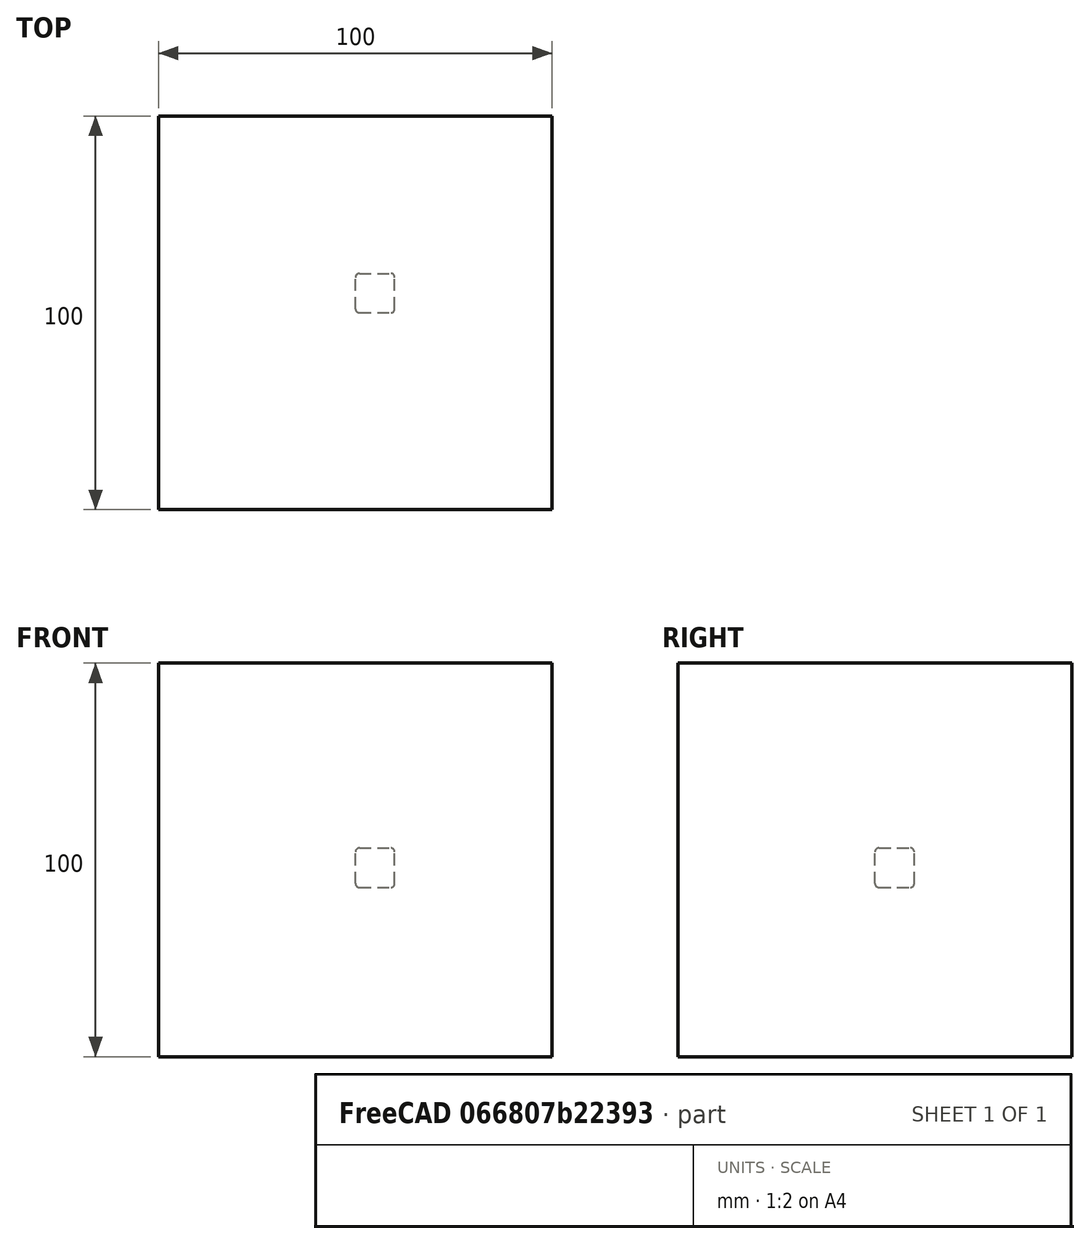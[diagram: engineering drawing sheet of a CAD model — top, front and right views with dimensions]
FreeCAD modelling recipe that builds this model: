
FCSTD DOCUMENT  (FreeCAD 0.22R36391 (Git))
Label: fillet
License: All rights reserved
objects: App::DocumentObjectGroupPython×1251, App::Part×2, Part::FeaturePython×1, Part::Box×1, Part::Fillet×1
note: 3 computed .brp shape members not serialized (recipe doc carries the construction recipe); baked Part::Feature solids carry a one-line shape summary decoded from their .brp

FEATURE [App::DocumentObjectGroupPython] HALFPI  # scripted group (container) (typed FeaturePython)
  name = HALFPI
  value = pi/2.
FEATURE [App::DocumentObjectGroupPython] PI  # scripted group (container) (typed FeaturePython)
  name = PI
  value = 1.*pi
FEATURE [App::DocumentObjectGroupPython] TWOPI  # scripted group (container) (typed FeaturePython)
  name = TWOPI
  value = 2.*pi
FEATURE [App::DocumentObjectGroupPython] Constants  # scripted group (container) (typed FeaturePython)
  Group = -> [HALFPI,PI,TWOPI]
FEATURE [App::DocumentObjectGroupPython] Variables  # scripted group (container) (typed FeaturePython)
FEATURE [App::DocumentObjectGroupPython] Quantities  # scripted group (container) (typed FeaturePython)
FEATURE [App::DocumentObjectGroupPython] Isotopes  # scripted group (container) (typed FeaturePython)
FEATURE [App::DocumentObjectGroupPython] Elements  # scripted group (container) (typed FeaturePython)
FEATURE [App::DocumentObjectGroupPython] Matrix  # scripted group (container) (typed FeaturePython)
FEATURE [App::DocumentObjectGroupPython] Surfaces  # scripted group (container) (typed FeaturePython)
FEATURE [App::DocumentObjectGroupPython] Opticals  # scripted group (container) (typed FeaturePython)
  Group = -> [Matrix,Surfaces]
FEATURE [App::DocumentObjectGroupPython] G4Isotopes  # scripted group (container) (typed FeaturePython)
FEATURE [App::DocumentObjectGroupPython] H_element  # scripted group (container) (typed FeaturePython)
  Z = 1
  atom_value = 1.008
  formula = H
  name = H_element
FEATURE [App::DocumentObjectGroupPython] He_element  # scripted group (container) (typed FeaturePython)
  Z = 2
  atom_value = 4.0026
  formula = He
  name = He_element
FEATURE [App::DocumentObjectGroupPython] Li_element  # scripted group (container) (typed FeaturePython)
  Z = 3
  atom_value = 6.94
  formula = Li
  name = Li_element
FEATURE [App::DocumentObjectGroupPython] Be_element  # scripted group (container) (typed FeaturePython)
  Z = 4
  atom_value = 9.01218
  formula = Be
  name = Be_element
FEATURE [App::DocumentObjectGroupPython] B_element  # scripted group (container) (typed FeaturePython)
  Z = 5
  atom_value = 10.81
  formula = B
  name = B_element
FEATURE [App::DocumentObjectGroupPython] C_element  # scripted group (container) (typed FeaturePython)
  Z = 6
  atom_value = 12.011
  formula = C
  name = C_element
FEATURE [App::DocumentObjectGroupPython] N_element  # scripted group (container) (typed FeaturePython)
  Z = 7
  atom_value = 14.007
  formula = N
  name = N_element
FEATURE [App::DocumentObjectGroupPython] O_element  # scripted group (container) (typed FeaturePython)
  Z = 8
  atom_value = 15.999
  formula = O
  name = O_element
FEATURE [App::DocumentObjectGroupPython] F_element  # scripted group (container) (typed FeaturePython)
  Z = 9
  atom_value = 18.9984
  formula = F
  name = F_element
FEATURE [App::DocumentObjectGroupPython] Ne_element  # scripted group (container) (typed FeaturePython)
  Z = 10
  atom_value = 20.1797
  formula = Ne
  name = Ne_element
FEATURE [App::DocumentObjectGroupPython] Na_element  # scripted group (container) (typed FeaturePython)
  Z = 11
  atom_value = 22.9898
  formula = Na
  name = Na_element
FEATURE [App::DocumentObjectGroupPython] Mg_element  # scripted group (container) (typed FeaturePython)
  Z = 12
  atom_value = 24.305
  formula = Mg
  name = Mg_element
FEATURE [App::DocumentObjectGroupPython] Al_element  # scripted group (container) (typed FeaturePython)
  Z = 13
  atom_value = 26.9815
  formula = Al
  name = Al_element
FEATURE [App::DocumentObjectGroupPython] Si_element  # scripted group (container) (typed FeaturePython)
  Z = 14
  atom_value = 28.085
  formula = Si
  name = Si_element
FEATURE [App::DocumentObjectGroupPython] P_element  # scripted group (container) (typed FeaturePython)
  Z = 15
  atom_value = 30.9738
  formula = P
  name = P_element
FEATURE [App::DocumentObjectGroupPython] S_element  # scripted group (container) (typed FeaturePython)
  Z = 16
  atom_value = 32.06
  formula = S
  name = S_element
FEATURE [App::DocumentObjectGroupPython] Cl_element  # scripted group (container) (typed FeaturePython)
  Z = 17
  atom_value = 35.45
  formula = Cl
  name = Cl_element
FEATURE [App::DocumentObjectGroupPython] Ar_element  # scripted group (container) (typed FeaturePython)
  Z = 18
  atom_value = 39.95
  formula = Ar
  name = Ar_element
FEATURE [App::DocumentObjectGroupPython] K_element  # scripted group (container) (typed FeaturePython)
  Z = 19
  atom_value = 39.0983
  formula = K
  name = K_element
FEATURE [App::DocumentObjectGroupPython] Ca_element  # scripted group (container) (typed FeaturePython)
  Z = 20
  atom_value = 40.078
  formula = Ca
  name = Ca_element
FEATURE [App::DocumentObjectGroupPython] Sc_element  # scripted group (container) (typed FeaturePython)
  Z = 21
  atom_value = 44.9559
  formula = Sc
  name = Sc_element
FEATURE [App::DocumentObjectGroupPython] Ti_element  # scripted group (container) (typed FeaturePython)
  Z = 22
  atom_value = 47.867
  formula = Ti
  name = Ti_element
FEATURE [App::DocumentObjectGroupPython] V_element  # scripted group (container) (typed FeaturePython)
  Z = 23
  atom_value = 50.9415
  formula = V
  name = V_element
FEATURE [App::DocumentObjectGroupPython] Cr_element  # scripted group (container) (typed FeaturePython)
  Z = 24
  atom_value = 51.9961
  formula = Cr
  name = Cr_element
FEATURE [App::DocumentObjectGroupPython] Mn_element  # scripted group (container) (typed FeaturePython)
  Z = 25
  atom_value = 54.938
  formula = Mn
  name = Mn_element
FEATURE [App::DocumentObjectGroupPython] Fe_element  # scripted group (container) (typed FeaturePython)
  Z = 26
  atom_value = 55.845
  formula = Fe
  name = Fe_element
FEATURE [App::DocumentObjectGroupPython] Co_element  # scripted group (container) (typed FeaturePython)
  Z = 27
  atom_value = 58.9332
  formula = Co
  name = Co_element
FEATURE [App::DocumentObjectGroupPython] Ni_element  # scripted group (container) (typed FeaturePython)
  Z = 28
  atom_value = 58.6934
  formula = Ni
  name = Ni_element
FEATURE [App::DocumentObjectGroupPython] Cu_element  # scripted group (container) (typed FeaturePython)
  Z = 29
  atom_value = 63.546
  formula = Cu
  name = Cu_element
FEATURE [App::DocumentObjectGroupPython] Zn_element  # scripted group (container) (typed FeaturePython)
  Z = 30
  atom_value = 65.38
  formula = Zn
  name = Zn_element
FEATURE [App::DocumentObjectGroupPython] Ga_element  # scripted group (container) (typed FeaturePython)
  Z = 31
  atom_value = 69.723
  formula = Ga
  name = Ga_element
FEATURE [App::DocumentObjectGroupPython] Ge_element  # scripted group (container) (typed FeaturePython)
  Z = 32
  atom_value = 72.63
  formula = Ge
  name = Ge_element
FEATURE [App::DocumentObjectGroupPython] As_element  # scripted group (container) (typed FeaturePython)
  Z = 33
  atom_value = 74.9216
  formula = As
  name = As_element
FEATURE [App::DocumentObjectGroupPython] Se_element  # scripted group (container) (typed FeaturePython)
  Z = 34
  atom_value = 78.971
  formula = Se
  name = Se_element
FEATURE [App::DocumentObjectGroupPython] Br_element  # scripted group (container) (typed FeaturePython)
  Z = 35
  atom_value = 79.904
  formula = Br
  name = Br_element
FEATURE [App::DocumentObjectGroupPython] Kr_element  # scripted group (container) (typed FeaturePython)
  Z = 36
  atom_value = 83.798
  formula = Kr
  name = Kr_element
FEATURE [App::DocumentObjectGroupPython] Rb_element  # scripted group (container) (typed FeaturePython)
  Z = 37
  atom_value = 85.4678
  formula = Rb
  name = Rb_element
FEATURE [App::DocumentObjectGroupPython] Sr_element  # scripted group (container) (typed FeaturePython)
  Z = 38
  atom_value = 87.62
  formula = Sr
  name = Sr_element
FEATURE [App::DocumentObjectGroupPython] Y_element  # scripted group (container) (typed FeaturePython)
  Z = 39
  atom_value = 88.9058
  formula = Y
  name = Y_element
FEATURE [App::DocumentObjectGroupPython] Zr_element  # scripted group (container) (typed FeaturePython)
  Z = 40
  atom_value = 91.224
  formula = Zr
  name = Zr_element
FEATURE [App::DocumentObjectGroupPython] Nb_element  # scripted group (container) (typed FeaturePython)
  Z = 41
  atom_value = 92.9064
  formula = Nb
  name = Nb_element
FEATURE [App::DocumentObjectGroupPython] Mo_element  # scripted group (container) (typed FeaturePython)
  Z = 42
  atom_value = 95.95
  formula = Mo
  name = Mo_element
FEATURE [App::DocumentObjectGroupPython] Tc_element  # scripted group (container) (typed FeaturePython)
  Z = 43
  atom_value = 97
  formula = Tc
  name = Tc_element
FEATURE [App::DocumentObjectGroupPython] Ru_element  # scripted group (container) (typed FeaturePython)
  Z = 44
  atom_value = 101.07
  formula = Ru
  name = Ru_element
FEATURE [App::DocumentObjectGroupPython] Rh_element  # scripted group (container) (typed FeaturePython)
  Z = 45
  atom_value = 102.905
  formula = Rh
  name = Rh_element
FEATURE [App::DocumentObjectGroupPython] Pd_element  # scripted group (container) (typed FeaturePython)
  Z = 46
  atom_value = 106.42
  formula = Pd
  name = Pd_element
FEATURE [App::DocumentObjectGroupPython] Ag_element  # scripted group (container) (typed FeaturePython)
  Z = 47
  atom_value = 107.868
  formula = Ag
  name = Ag_element
FEATURE [App::DocumentObjectGroupPython] Cd_element  # scripted group (container) (typed FeaturePython)
  Z = 48
  atom_value = 112.414
  formula = Cd
  name = Cd_element
FEATURE [App::DocumentObjectGroupPython] In_element  # scripted group (container) (typed FeaturePython)
  Z = 49
  atom_value = 114.818
  formula = In
  name = In_element
FEATURE [App::DocumentObjectGroupPython] Sn_element  # scripted group (container) (typed FeaturePython)
  Z = 50
  atom_value = 118.71
  formula = Sn
  name = Sn_element
FEATURE [App::DocumentObjectGroupPython] Sb_element  # scripted group (container) (typed FeaturePython)
  Z = 51
  atom_value = 121.76
  formula = Sb
  name = Sb_element
FEATURE [App::DocumentObjectGroupPython] Te_element  # scripted group (container) (typed FeaturePython)
  Z = 52
  atom_value = 127.6
  formula = Te
  name = Te_element
FEATURE [App::DocumentObjectGroupPython] I_element  # scripted group (container) (typed FeaturePython)
  Z = 53
  atom_value = 126.904
  formula = I
  name = I_element
FEATURE [App::DocumentObjectGroupPython] Xe_element  # scripted group (container) (typed FeaturePython)
  Z = 54
  atom_value = 131.293
  formula = Xe
  name = Xe_element
FEATURE [App::DocumentObjectGroupPython] Cs_element  # scripted group (container) (typed FeaturePython)
  Z = 55
  atom_value = 132.905
  formula = Cs
  name = Cs_element
FEATURE [App::DocumentObjectGroupPython] Ba_element  # scripted group (container) (typed FeaturePython)
  Z = 56
  atom_value = 137.327
  formula = Ba
  name = Ba_element
FEATURE [App::DocumentObjectGroupPython] La_element  # scripted group (container) (typed FeaturePython)
  Z = 57
  atom_value = 138.905
  formula = La
  name = La_element
FEATURE [App::DocumentObjectGroupPython] Ce_element  # scripted group (container) (typed FeaturePython)
  Z = 58
  atom_value = 140.116
  formula = Ce
  name = Ce_element
FEATURE [App::DocumentObjectGroupPython] Pr_element  # scripted group (container) (typed FeaturePython)
  Z = 59
  atom_value = 140.908
  formula = Pr
  name = Pr_element
FEATURE [App::DocumentObjectGroupPython] Nd_element  # scripted group (container) (typed FeaturePython)
  Z = 60
  atom_value = 144.242
  formula = Nd
  name = Nd_element
FEATURE [App::DocumentObjectGroupPython] Pm_element  # scripted group (container) (typed FeaturePython)
  Z = 61
  atom_value = 145
  formula = Pm
  name = Pm_element
FEATURE [App::DocumentObjectGroupPython] Sm_element  # scripted group (container) (typed FeaturePython)
  Z = 62
  atom_value = 150.36
  formula = Sm
  name = Sm_element
FEATURE [App::DocumentObjectGroupPython] Eu_element  # scripted group (container) (typed FeaturePython)
  Z = 63
  atom_value = 151.964
  formula = Eu
  name = Eu_element
FEATURE [App::DocumentObjectGroupPython] Gd_element  # scripted group (container) (typed FeaturePython)
  Z = 64
  atom_value = 157.25
  formula = Gd
  name = Gd_element
FEATURE [App::DocumentObjectGroupPython] Tb_element  # scripted group (container) (typed FeaturePython)
  Z = 65
  atom_value = 158.925
  formula = Tb
  name = Tb_element
FEATURE [App::DocumentObjectGroupPython] Dy_element  # scripted group (container) (typed FeaturePython)
  Z = 66
  atom_value = 162.5
  formula = Dy
  name = Dy_element
FEATURE [App::DocumentObjectGroupPython] Ho_element  # scripted group (container) (typed FeaturePython)
  Z = 67
  atom_value = 164.93
  formula = Ho
  name = Ho_element
FEATURE [App::DocumentObjectGroupPython] Er_element  # scripted group (container) (typed FeaturePython)
  Z = 68
  atom_value = 167.259
  formula = Er
  name = Er_element
FEATURE [App::DocumentObjectGroupPython] Tm_element  # scripted group (container) (typed FeaturePython)
  Z = 69
  atom_value = 168.934
  formula = Tm
  name = Tm_element
FEATURE [App::DocumentObjectGroupPython] Yb_element  # scripted group (container) (typed FeaturePython)
  Z = 70
  atom_value = 173.045
  formula = Yb
  name = Yb_element
FEATURE [App::DocumentObjectGroupPython] Lu_element  # scripted group (container) (typed FeaturePython)
  Z = 71
  atom_value = 174.967
  formula = Lu
  name = Lu_element
FEATURE [App::DocumentObjectGroupPython] Hf_element  # scripted group (container) (typed FeaturePython)
  Z = 72
  atom_value = 178.49
  formula = Hf
  name = Hf_element
FEATURE [App::DocumentObjectGroupPython] Ta_element  # scripted group (container) (typed FeaturePython)
  Z = 73
  atom_value = 180.948
  formula = Ta
  name = Ta_element
FEATURE [App::DocumentObjectGroupPython] W_element  # scripted group (container) (typed FeaturePython)
  Z = 74
  atom_value = 183.84
  formula = W
  name = W_element
FEATURE [App::DocumentObjectGroupPython] Re_element  # scripted group (container) (typed FeaturePython)
  Z = 75
  atom_value = 186.207
  formula = Re
  name = Re_element
FEATURE [App::DocumentObjectGroupPython] Os_element  # scripted group (container) (typed FeaturePython)
  Z = 76
  atom_value = 190.23
  formula = Os
  name = Os_element
FEATURE [App::DocumentObjectGroupPython] Ir_element  # scripted group (container) (typed FeaturePython)
  Z = 77
  atom_value = 192.217
  formula = Ir
  name = Ir_element
FEATURE [App::DocumentObjectGroupPython] Pt_element  # scripted group (container) (typed FeaturePython)
  Z = 78
  atom_value = 195.084
  formula = Pt
  name = Pt_element
FEATURE [App::DocumentObjectGroupPython] Au_element  # scripted group (container) (typed FeaturePython)
  Z = 79
  atom_value = 196.967
  formula = Au
  name = Au_element
FEATURE [App::DocumentObjectGroupPython] Hg_element  # scripted group (container) (typed FeaturePython)
  Z = 80
  atom_value = 200.592
  formula = Hg
  name = Hg_element
FEATURE [App::DocumentObjectGroupPython] Tl_element  # scripted group (container) (typed FeaturePython)
  Z = 81
  atom_value = 204.38
  formula = Tl
  name = Tl_element
FEATURE [App::DocumentObjectGroupPython] Pb_element  # scripted group (container) (typed FeaturePython)
  Z = 82
  atom_value = 207.2
  formula = Pb
  name = Pb_element
FEATURE [App::DocumentObjectGroupPython] Bi_element  # scripted group (container) (typed FeaturePython)
  Z = 83
  atom_value = 208.98
  formula = Bi
  name = Bi_element
FEATURE [App::DocumentObjectGroupPython] Po_element  # scripted group (container) (typed FeaturePython)
  Z = 84
  atom_value = 209
  formula = Po
  name = Po_element
FEATURE [App::DocumentObjectGroupPython] At_element  # scripted group (container) (typed FeaturePython)
  Z = 85
  atom_value = 210
  formula = At
  name = At_element
FEATURE [App::DocumentObjectGroupPython] Rn_element  # scripted group (container) (typed FeaturePython)
  Z = 86
  atom_value = 222
  formula = Rn
  name = Rn_element
FEATURE [App::DocumentObjectGroupPython] Fr_element  # scripted group (container) (typed FeaturePython)
  Z = 87
  atom_value = 223
  formula = Fr
  name = Fr_element
FEATURE [App::DocumentObjectGroupPython] Ra_element  # scripted group (container) (typed FeaturePython)
  Z = 88
  atom_value = 226
  formula = Ra
  name = Ra_element
FEATURE [App::DocumentObjectGroupPython] Ac_element  # scripted group (container) (typed FeaturePython)
  Z = 89
  atom_value = 227
  formula = Ac
  name = Ac_element
FEATURE [App::DocumentObjectGroupPython] Th_element  # scripted group (container) (typed FeaturePython)
  Z = 90
  atom_value = 232.038
  formula = Th
  name = Th_element
FEATURE [App::DocumentObjectGroupPython] Pa_element  # scripted group (container) (typed FeaturePython)
  Z = 91
  atom_value = 231.036
  formula = Pa
  name = Pa_element
FEATURE [App::DocumentObjectGroupPython] U_element  # scripted group (container) (typed FeaturePython)
  Z = 92
  atom_value = 238.029
  formula = U
  name = U_element
FEATURE [App::DocumentObjectGroupPython] Np_element  # scripted group (container) (typed FeaturePython)
  Z = 93
  atom_value = 237
  formula = Np
  name = Np_element
FEATURE [App::DocumentObjectGroupPython] Pu_element  # scripted group (container) (typed FeaturePython)
  Z = 94
  atom_value = 244
  formula = Pu
  name = Pu_element
FEATURE [App::DocumentObjectGroupPython] Am_element  # scripted group (container) (typed FeaturePython)
  Z = 95
  atom_value = 243
  formula = Am
  name = Am_element
FEATURE [App::DocumentObjectGroupPython] Cm_element  # scripted group (container) (typed FeaturePython)
  Z = 96
  atom_value = 247
  formula = Cm
  name = Cm_element
FEATURE [App::DocumentObjectGroupPython] Bk_element  # scripted group (container) (typed FeaturePython)
  Z = 97
  atom_value = 247
  formula = Bk
  name = Bk_element
FEATURE [App::DocumentObjectGroupPython] Cf_element  # scripted group (container) (typed FeaturePython)
  Z = 98
  atom_value = 251
  formula = Cf
  name = Cf_element
FEATURE [App::DocumentObjectGroupPython] G4Elements  # scripted group (container) (typed FeaturePython)
  Group = -> [H_element,He_element,Li_element,Be_element,B_element,C_element,N_element,O_element,F_element,Ne_element,Na_element,Mg_element,Al_element,Si_element,P_element,S_element,Cl_element,Ar_element,K_element,Ca_element,Sc_element,Ti_element,V_element,Cr_element,Mn_element,Fe_element,Co_element,Ni_element,Cu_element,Zn_element,Ga_element,Ge_element,As_element,Se_element,Br_element,Kr_element,Rb_element,+61 more]
FEATURE [App::DocumentObjectGroupPython] H_element001  label="H_element : 0.101"  # scripted group (container) (typed FeaturePython)
  n = 0.101327
FEATURE [App::DocumentObjectGroupPython] C_element001  label="C_element : 0.775"  # scripted group (container) (typed FeaturePython)
  n = 0.7755
FEATURE [App::DocumentObjectGroupPython] N_element001  label="N_element : 0.035"  # scripted group (container) (typed FeaturePython)
  n = 0.035057
FEATURE [App::DocumentObjectGroupPython] O_element001  label="O_element : 0.052"  # scripted group (container) (typed FeaturePython)
  n = 0.0523159
FEATURE [App::DocumentObjectGroupPython] F_element001  label="F_element : 0.017"  # scripted group (container) (typed FeaturePython)
  n = 0.017422
FEATURE [App::DocumentObjectGroupPython] Ca_element001  label="Ca_element : 0.018"  # scripted group (container) (typed FeaturePython)
  n = 0.018378
FEATURE [App::DocumentObjectGroupPython] G4_A_150_TISSUE  label="G4_A-150_TISSUE"  # scripted group (container) (typed FeaturePython)
  Dunit = g/cm3
  Dvalue = 1.127
  Group = -> [H_element001,C_element001,N_element001,O_element001,F_element001,Ca_element001]
  conduct = 2
  density = 1
  expand = 3
  formula = G4_A-150_TISSUE
  name = G4_A-150_TISSUE
  specific = 4
FEATURE [App::DocumentObjectGroupPython] C_element002  label="C_element : 3"  # scripted group (container) (typed FeaturePython)
  n = 3
  ref = C_element
FEATURE [App::DocumentObjectGroupPython] H_element002  label="H_element : 6"  # scripted group (container) (typed FeaturePython)
  n = 6
  ref = H_element
FEATURE [App::DocumentObjectGroupPython] O_element002  label="O_element : 1"  # scripted group (container) (typed FeaturePython)
  n = 1
  ref = O_element
FEATURE [App::DocumentObjectGroupPython] G4_ACETONE  # scripted group (container) (typed FeaturePython)
  Dunit = g/cm3
  Dvalue = 0.7899
  Group = -> [C_element002,H_element002,O_element002]
  conduct = 2
  density = 1
  expand = 3
  formula = G4_ACETONE
  name = G4_ACETONE
  specific = 4
FEATURE [App::DocumentObjectGroupPython] C_element003  label="C_element : 2"  # scripted group (container) (typed FeaturePython)
  n = 2
  ref = C_element
FEATURE [App::DocumentObjectGroupPython] H_element003  label="H_element : 2"  # scripted group (container) (typed FeaturePython)
  n = 2
  ref = H_element
FEATURE [App::DocumentObjectGroupPython] G4_ACETYLENE  # scripted group (container) (typed FeaturePython)
  Dunit = g/cm3
  Dvalue = 0.0010967
  Group = -> [C_element003,H_element003]
  conduct = 2
  density = 1
  expand = 3
  formula = G4_ACETYLENE
  name = G4_ACETYLENE
  specific = 4
FEATURE [App::DocumentObjectGroupPython] C_element004  label="C_element : 5"  # scripted group (container) (typed FeaturePython)
  n = 5
  ref = C_element
FEATURE [App::DocumentObjectGroupPython] H_element004  label="H_element : 5"  # scripted group (container) (typed FeaturePython)
  n = 5
  ref = H_element
FEATURE [App::DocumentObjectGroupPython] N_element002  label="N_element : 5"  # scripted group (container) (typed FeaturePython)
  n = 5
  ref = N_element
FEATURE [App::DocumentObjectGroupPython] G4_ADENINE  # scripted group (container) (typed FeaturePython)
  Dunit = g/cm3
  Dvalue = 1.6
  Group = -> [C_element004,H_element004,N_element002]
  conduct = 2
  density = 1
  expand = 3
  formula = G4_ADENINE
  name = G4_ADENINE
  specific = 4
FEATURE [App::DocumentObjectGroupPython] H_element005  label="H_element : 0.114"  # scripted group (container) (typed FeaturePython)
  n = 0.114
FEATURE [App::DocumentObjectGroupPython] C_element005  label="C_element : 0.598"  # scripted group (container) (typed FeaturePython)
  n = 0.598
FEATURE [App::DocumentObjectGroupPython] N_element003  label="N_element : 0.007"  # scripted group (container) (typed FeaturePython)
  n = 0.007
FEATURE [App::DocumentObjectGroupPython] O_element003  label="O_element : 0.278"  # scripted group (container) (typed FeaturePython)
  n = 0.278
FEATURE [App::DocumentObjectGroupPython] Na_element001  label="Na_element : 0.001"  # scripted group (container) (typed FeaturePython)
  n = 0.001
FEATURE [App::DocumentObjectGroupPython] S_element001  label="S_element : 0.001"  # scripted group (container) (typed FeaturePython)
  n = 0.001
FEATURE [App::DocumentObjectGroupPython] Cl_element001  label="Cl_element : 0.001"  # scripted group (container) (typed FeaturePython)
  n = 0.001
FEATURE [App::DocumentObjectGroupPython] G4_ADIPOSE_TISSUE_ICRP  # scripted group (container) (typed FeaturePython)
  Dunit = g/cm3
  Dvalue = 0.95
  Group = -> [H_element005,C_element005,N_element003,O_element003,Na_element001,S_element001,Cl_element001]
  conduct = 2
  density = 1
  expand = 3
  formula = G4_ADIPOSE_TISSUE_ICRP
  name = G4_ADIPOSE_TISSUE_ICRP
  specific = 4
FEATURE [App::DocumentObjectGroupPython] C_element006  label="C_element : 0.000"  # scripted group (container) (typed FeaturePython)
  n = 0.000124
FEATURE [App::DocumentObjectGroupPython] N_element004  label="N_element : 0.755"  # scripted group (container) (typed FeaturePython)
  n = 0.755268
FEATURE [App::DocumentObjectGroupPython] O_element004  label="O_element : 0.232"  # scripted group (container) (typed FeaturePython)
  n = 0.231781
FEATURE [App::DocumentObjectGroupPython] Ar_element001  label="Ar_element : 0.013"  # scripted group (container) (typed FeaturePython)
  n = 0.012827
FEATURE [App::DocumentObjectGroupPython] G4_AIR  # scripted group (container) (typed FeaturePython)
  Dunit = g/cm3
  Dvalue = 0.00120479
  Group = -> [C_element006,N_element004,O_element004,Ar_element001]
  conduct = 2
  density = 1
  expand = 3
  formula = G4_AIR
  name = G4_AIR
  specific = 4
FEATURE [App::DocumentObjectGroupPython] C_element007  label="C_element : 006"  # scripted group (container) (typed FeaturePython)
  n = 3
  ref = C_element
FEATURE [App::DocumentObjectGroupPython] H_element006  label="H_element : 7"  # scripted group (container) (typed FeaturePython)
  n = 7
  ref = H_element
FEATURE [App::DocumentObjectGroupPython] N_element005  label="N_element : 1"  # scripted group (container) (typed FeaturePython)
  n = 1
  ref = N_element
FEATURE [App::DocumentObjectGroupPython] O_element005  label="O_element : 2"  # scripted group (container) (typed FeaturePython)
  n = 2
  ref = O_element
FEATURE [App::DocumentObjectGroupPython] G4_ALANINE  # scripted group (container) (typed FeaturePython)
  Dunit = g/cm3
  Dvalue = 1.42
  Group = -> [C_element007,H_element006,N_element005,O_element005]
  conduct = 2
  density = 1
  expand = 3
  formula = G4_ALANINE
  name = G4_ALANINE
  specific = 4
FEATURE [App::DocumentObjectGroupPython] Al_element001  label="Al_element : 2"  # scripted group (container) (typed FeaturePython)
  n = 2
  ref = Al_element
FEATURE [App::DocumentObjectGroupPython] O_element006  label="O_element : 3"  # scripted group (container) (typed FeaturePython)
  n = 3
  ref = O_element
FEATURE [App::DocumentObjectGroupPython] G4_ALUMINUM_OXIDE  # scripted group (container) (typed FeaturePython)
  Dunit = g/cm3
  Dvalue = 3.97
  Group = -> [Al_element001,O_element006]
  conduct = 2
  density = 1
  expand = 3
  formula = G4_ALUMINUM_OXIDE
  name = G4_ALUMINUM_OXIDE
  specific = 4
FEATURE [App::DocumentObjectGroupPython] H_element007  label="H_element : 0.106"  # scripted group (container) (typed FeaturePython)
  n = 0.10593
FEATURE [App::DocumentObjectGroupPython] C_element008  label="C_element : 0.789"  # scripted group (container) (typed FeaturePython)
  n = 0.788974
FEATURE [App::DocumentObjectGroupPython] O_element007  label="O_element : 0.105"  # scripted group (container) (typed FeaturePython)
  n = 0.105096
FEATURE [App::DocumentObjectGroupPython] G4_AMBER  # scripted group (container) (typed FeaturePython)
  Dunit = g/cm3
  Dvalue = 1.1
  Group = -> [H_element007,C_element008,O_element007]
  conduct = 2
  density = 1
  expand = 3
  formula = G4_AMBER
  name = G4_AMBER
  specific = 4
FEATURE [App::DocumentObjectGroupPython] N_element006  label="N_element : 006"  # scripted group (container) (typed FeaturePython)
  n = 1
  ref = N_element
FEATURE [App::DocumentObjectGroupPython] H_element008  label="H_element : 3"  # scripted group (container) (typed FeaturePython)
  n = 3
  ref = H_element
FEATURE [App::DocumentObjectGroupPython] G4_AMMONIA  # scripted group (container) (typed FeaturePython)
  Dunit = g/cm3
  Dvalue = 0.000826019
  Group = -> [N_element006,H_element008]
  conduct = 2
  density = 1
  expand = 3
  formula = G4_AMMONIA
  name = G4_AMMONIA
  specific = 4
FEATURE [App::DocumentObjectGroupPython] C_element009  label="C_element : 6"  # scripted group (container) (typed FeaturePython)
  n = 6
  ref = C_element
FEATURE [App::DocumentObjectGroupPython] H_element009  label="H_element : 008"  # scripted group (container) (typed FeaturePython)
  n = 7
  ref = H_element
FEATURE [App::DocumentObjectGroupPython] N_element007  label="N_element : 007"  # scripted group (container) (typed FeaturePython)
  n = 1
  ref = N_element
FEATURE [App::DocumentObjectGroupPython] G4_ANILINE  # scripted group (container) (typed FeaturePython)
  Dunit = g/cm3
  Dvalue = 1.0235
  Group = -> [C_element009,H_element009,N_element007]
  conduct = 2
  density = 1
  expand = 3
  formula = G4_ANILINE
  name = G4_ANILINE
  specific = 4
FEATURE [App::DocumentObjectGroupPython] C_element010  label="C_element : 14"  # scripted group (container) (typed FeaturePython)
  n = 14
  ref = C_element
FEATURE [App::DocumentObjectGroupPython] H_element010  label="H_element : 10"  # scripted group (container) (typed FeaturePython)
  n = 10
  ref = H_element
FEATURE [App::DocumentObjectGroupPython] G4_ANTHRACENE  # scripted group (container) (typed FeaturePython)
  Dunit = g/cm3
  Dvalue = 1.283
  Group = -> [C_element010,H_element010]
  conduct = 2
  density = 1
  expand = 3
  formula = G4_ANTHRACENE
  name = G4_ANTHRACENE
  specific = 4
FEATURE [App::DocumentObjectGroupPython] H_element011  label="H_element : 0.065"  # scripted group (container) (typed FeaturePython)
  n = 0.0654709
FEATURE [App::DocumentObjectGroupPython] C_element011  label="C_element : 0.537"  # scripted group (container) (typed FeaturePython)
  n = 0.536944
FEATURE [App::DocumentObjectGroupPython] N_element008  label="N_element : 0.021"  # scripted group (container) (typed FeaturePython)
  n = 0.0215
FEATURE [App::DocumentObjectGroupPython] O_element008  label="O_element : 0.032"  # scripted group (container) (typed FeaturePython)
  n = 0.032085
FEATURE [App::DocumentObjectGroupPython] F_element002  label="F_element : 0.167"  # scripted group (container) (typed FeaturePython)
  n = 0.167411
FEATURE [App::DocumentObjectGroupPython] Ca_element002  label="Ca_element : 0.177"  # scripted group (container) (typed FeaturePython)
  n = 0.176589
FEATURE [App::DocumentObjectGroupPython] G4_B_100_BONE  label="G4_B-100_BONE"  # scripted group (container) (typed FeaturePython)
  Dunit = g/cm3
  Dvalue = 1.45
  Group = -> [H_element011,C_element011,N_element008,O_element008,F_element002,Ca_element002]
  conduct = 2
  density = 1
  expand = 3
  formula = G4_B-100_BONE
  name = G4_B-100_BONE
  specific = 4
FEATURE [App::DocumentObjectGroupPython] H_element012  label="H_element : 0.057"  # scripted group (container) (typed FeaturePython)
  n = 0.057441
FEATURE [App::DocumentObjectGroupPython] C_element012  label="C_element : 0.790"  # scripted group (container) (typed FeaturePython)
  n = 0.774591
FEATURE [App::DocumentObjectGroupPython] O_element009  label="O_element : 0.168"  # scripted group (container) (typed FeaturePython)
  n = 0.167968
FEATURE [App::DocumentObjectGroupPython] G4_BAKELITE  # scripted group (container) (typed FeaturePython)
  Dunit = g/cm3
  Dvalue = 1.25
  Group = -> [H_element012,C_element012,O_element009]
  conduct = 2
  density = 1
  expand = 3
  formula = G4_BAKELITE
  name = G4_BAKELITE
  specific = 4
FEATURE [App::DocumentObjectGroupPython] Ba_element001  label="Ba_element : 1"  # scripted group (container) (typed FeaturePython)
  n = 1
  ref = Ba_element
FEATURE [App::DocumentObjectGroupPython] F_element003  label="F_element : 2"  # scripted group (container) (typed FeaturePython)
  n = 2
  ref = F_element
FEATURE [App::DocumentObjectGroupPython] G4_BARIUM_FLUORIDE  # scripted group (container) (typed FeaturePython)
  Dunit = g/cm3
  Dvalue = 4.89
  Group = -> [Ba_element001,F_element003]
  conduct = 2
  density = 1
  expand = 3
  formula = G4_BARIUM_FLUORIDE
  name = G4_BARIUM_FLUORIDE
  specific = 4
FEATURE [App::DocumentObjectGroupPython] Ba_element002  label="Ba_element : 002"  # scripted group (container) (typed FeaturePython)
  n = 1
  ref = Ba_element
FEATURE [App::DocumentObjectGroupPython] S_element002  label="S_element : 1"  # scripted group (container) (typed FeaturePython)
  n = 1
  ref = S_element
FEATURE [App::DocumentObjectGroupPython] O_element010  label="O_element : 4"  # scripted group (container) (typed FeaturePython)
  n = 4
  ref = O_element
FEATURE [App::DocumentObjectGroupPython] G4_BARIUM_SULFATE  # scripted group (container) (typed FeaturePython)
  Dunit = g/cm3
  Dvalue = 4.5
  Group = -> [Ba_element002,S_element002,O_element010]
  conduct = 2
  density = 1
  expand = 3
  formula = G4_BARIUM_SULFATE
  name = G4_BARIUM_SULFATE
  specific = 4
FEATURE [App::DocumentObjectGroupPython] C_element013  label="C_element : 007"  # scripted group (container) (typed FeaturePython)
  n = 6
  ref = C_element
FEATURE [App::DocumentObjectGroupPython] H_element013  label="H_element : 009"  # scripted group (container) (typed FeaturePython)
  n = 6
  ref = H_element
FEATURE [App::DocumentObjectGroupPython] G4_BENZENE  # scripted group (container) (typed FeaturePython)
  Dunit = g/cm3
  Dvalue = 0.87865
  Group = -> [C_element013,H_element013]
  conduct = 2
  density = 1
  expand = 3
  formula = G4_BENZENE
  name = G4_BENZENE
  specific = 4
FEATURE [App::DocumentObjectGroupPython] Be_element001  label="Be_element : 1"  # scripted group (container) (typed FeaturePython)
  n = 1
  ref = Be_element
FEATURE [App::DocumentObjectGroupPython] O_element011  label="O_element : 005"  # scripted group (container) (typed FeaturePython)
  n = 1
  ref = O_element
FEATURE [App::DocumentObjectGroupPython] G4_BERYLLIUM_OXIDE  # scripted group (container) (typed FeaturePython)
  Dunit = g/cm3
  Dvalue = 3.01
  Group = -> [Be_element001,O_element011]
  conduct = 2
  density = 1
  expand = 3
  formula = G4_BERYLLIUM_OXIDE
  name = G4_BERYLLIUM_OXIDE
  specific = 4
FEATURE [App::DocumentObjectGroupPython] Bi_element001  label="Bi_element : 4"  # scripted group (container) (typed FeaturePython)
  n = 4
  ref = Bi_element
FEATURE [App::DocumentObjectGroupPython] Ge_element001  label="Ge_element : 3"  # scripted group (container) (typed FeaturePython)
  n = 3
  ref = Ge_element
FEATURE [App::DocumentObjectGroupPython] O_element012  label="O_element : 12"  # scripted group (container) (typed FeaturePython)
  n = 12
  ref = O_element
FEATURE [App::DocumentObjectGroupPython] G4_BGO  # scripted group (container) (typed FeaturePython)
  Dunit = g/cm3
  Dvalue = 7.13
  Group = -> [Bi_element001,Ge_element001,O_element012]
  conduct = 2
  density = 1
  expand = 3
  formula = G4_BGO
  name = G4_BGO
  specific = 4
FEATURE [App::DocumentObjectGroupPython] H_element014  label="H_element : 0.102"  # scripted group (container) (typed FeaturePython)
  n = 0.102
FEATURE [App::DocumentObjectGroupPython] C_element014  label="C_element : 0.110"  # scripted group (container) (typed FeaturePython)
  n = 0.11
FEATURE [App::DocumentObjectGroupPython] N_element009  label="N_element : 0.033"  # scripted group (container) (typed FeaturePython)
  n = 0.033
FEATURE [App::DocumentObjectGroupPython] O_element013  label="O_element : 0.745"  # scripted group (container) (typed FeaturePython)
  n = 0.745
FEATURE [App::DocumentObjectGroupPython] Na_element002  label="Na_element : 0.002"  # scripted group (container) (typed FeaturePython)
  n = 0.001
FEATURE [App::DocumentObjectGroupPython] P_element001  label="P_element : 0.001"  # scripted group (container) (typed FeaturePython)
  n = 0.001
FEATURE [App::DocumentObjectGroupPython] S_element003  label="S_element : 0.002"  # scripted group (container) (typed FeaturePython)
  n = 0.002
FEATURE [App::DocumentObjectGroupPython] Cl_element002  label="Cl_element : 0.003"  # scripted group (container) (typed FeaturePython)
  n = 0.003
FEATURE [App::DocumentObjectGroupPython] K_element001  label="K_element : 0.002"  # scripted group (container) (typed FeaturePython)
  n = 0.002
FEATURE [App::DocumentObjectGroupPython] Fe_element001  label="Fe_element : 0.001"  # scripted group (container) (typed FeaturePython)
  n = 0.001
FEATURE [App::DocumentObjectGroupPython] G4_BLOOD_ICRP  # scripted group (container) (typed FeaturePython)
  Dunit = g/cm3
  Dvalue = 1.06
  Group = -> [H_element014,C_element014,N_element009,O_element013,Na_element002,P_element001,S_element003,Cl_element002,K_element001,Fe_element001]
  conduct = 2
  density = 1
  expand = 3
  formula = G4_BLOOD_ICRP
  name = G4_BLOOD_ICRP
  specific = 4
FEATURE [App::DocumentObjectGroupPython] H_element015  label="H_element : 0.064"  # scripted group (container) (typed FeaturePython)
  n = 0.064
FEATURE [App::DocumentObjectGroupPython] C_element015  label="C_element : 0.278"  # scripted group (container) (typed FeaturePython)
  n = 0.278
FEATURE [App::DocumentObjectGroupPython] N_element010  label="N_element : 0.027"  # scripted group (container) (typed FeaturePython)
  n = 0.027
FEATURE [App::DocumentObjectGroupPython] O_element014  label="O_element : 0.410"  # scripted group (container) (typed FeaturePython)
  n = 0.41
FEATURE [App::DocumentObjectGroupPython] Mg_element001  label="Mg_element : 0.002"  # scripted group (container) (typed FeaturePython)
  n = 0.002
FEATURE [App::DocumentObjectGroupPython] P_element002  label="P_element : 0.070"  # scripted group (container) (typed FeaturePython)
  n = 0.07
FEATURE [App::DocumentObjectGroupPython] S_element004  label="S_element : 0.003"  # scripted group (container) (typed FeaturePython)
  n = 0.002
FEATURE [App::DocumentObjectGroupPython] Ca_element003  label="Ca_element : 0.147"  # scripted group (container) (typed FeaturePython)
  n = 0.147
FEATURE [App::DocumentObjectGroupPython] G4_BONE_COMPACT_ICRU  # scripted group (container) (typed FeaturePython)
  Dunit = g/cm3
  Dvalue = 1.85
  Group = -> [H_element015,C_element015,N_element010,O_element014,Mg_element001,P_element002,S_element004,Ca_element003]
  conduct = 2
  density = 1
  expand = 3
  formula = G4_BONE_COMPACT_ICRU
  name = G4_BONE_COMPACT_ICRU
  specific = 4
FEATURE [App::DocumentObjectGroupPython] H_element016  label="H_element : 0.034"  # scripted group (container) (typed FeaturePython)
  n = 0.034
FEATURE [App::DocumentObjectGroupPython] C_element016  label="C_element : 0.155"  # scripted group (container) (typed FeaturePython)
  n = 0.155
FEATURE [App::DocumentObjectGroupPython] N_element011  label="N_element : 0.042"  # scripted group (container) (typed FeaturePython)
  n = 0.042
FEATURE [App::DocumentObjectGroupPython] O_element015  label="O_element : 0.435"  # scripted group (container) (typed FeaturePython)
  n = 0.435
FEATURE [App::DocumentObjectGroupPython] Na_element003  label="Na_element : 0.003"  # scripted group (container) (typed FeaturePython)
  n = 0.001
FEATURE [App::DocumentObjectGroupPython] Mg_element002  label="Mg_element : 0.003"  # scripted group (container) (typed FeaturePython)
  n = 0.002
FEATURE [App::DocumentObjectGroupPython] P_element003  label="P_element : 0.103"  # scripted group (container) (typed FeaturePython)
  n = 0.103
FEATURE [App::DocumentObjectGroupPython] S_element005  label="S_element : 0.004"  # scripted group (container) (typed FeaturePython)
  n = 0.003
FEATURE [App::DocumentObjectGroupPython] Ca_element004  label="Ca_element : 0.225"  # scripted group (container) (typed FeaturePython)
  n = 0.225
FEATURE [App::DocumentObjectGroupPython] G4_BONE_CORTICAL_ICRP  # scripted group (container) (typed FeaturePython)
  Dunit = g/cm3
  Dvalue = 1.92
  Group = -> [H_element016,C_element016,N_element011,O_element015,Na_element003,Mg_element002,P_element003,S_element005,Ca_element004]
  conduct = 2
  density = 1
  expand = 3
  formula = G4_BONE_CORTICAL_ICRP
  name = G4_BONE_CORTICAL_ICRP
  specific = 4
FEATURE [App::DocumentObjectGroupPython] B_element001  label="B_element : 4"  # scripted group (container) (typed FeaturePython)
  n = 4
  ref = B_element
FEATURE [App::DocumentObjectGroupPython] C_element017  label="C_element : 1"  # scripted group (container) (typed FeaturePython)
  n = 1
  ref = C_element
FEATURE [App::DocumentObjectGroupPython] G4_BORON_CARBIDE  # scripted group (container) (typed FeaturePython)
  Dunit = g/cm3
  Dvalue = 2.52
  Group = -> [B_element001,C_element017]
  conduct = 2
  density = 1
  expand = 3
  formula = G4_BORON_CARBIDE
  name = G4_BORON_CARBIDE
  specific = 4
FEATURE [App::DocumentObjectGroupPython] B_element002  label="B_element : 2"  # scripted group (container) (typed FeaturePython)
  n = 2
  ref = B_element
FEATURE [App::DocumentObjectGroupPython] O_element016  label="O_element : 006"  # scripted group (container) (typed FeaturePython)
  n = 3
  ref = O_element
FEATURE [App::DocumentObjectGroupPython] G4_BORON_OXIDE  # scripted group (container) (typed FeaturePython)
  Dunit = g/cm3
  Dvalue = 1.812
  Group = -> [B_element002,O_element016]
  conduct = 2
  density = 1
  expand = 3
  formula = G4_BORON_OXIDE
  name = G4_BORON_OXIDE
  specific = 4
FEATURE [App::DocumentObjectGroupPython] H_element017  label="H_element : 0.107"  # scripted group (container) (typed FeaturePython)
  n = 0.107
FEATURE [App::DocumentObjectGroupPython] C_element018  label="C_element : 0.145"  # scripted group (container) (typed FeaturePython)
  n = 0.145
FEATURE [App::DocumentObjectGroupPython] N_element012  label="N_element : 0.022"  # scripted group (container) (typed FeaturePython)
  n = 0.022
FEATURE [App::DocumentObjectGroupPython] O_element017  label="O_element : 0.712"  # scripted group (container) (typed FeaturePython)
  n = 0.712
FEATURE [App::DocumentObjectGroupPython] Na_element004  label="Na_element : 0.004"  # scripted group (container) (typed FeaturePython)
  n = 0.002
FEATURE [App::DocumentObjectGroupPython] P_element004  label="P_element : 0.004"  # scripted group (container) (typed FeaturePython)
  n = 0.004
FEATURE [App::DocumentObjectGroupPython] S_element006  label="S_element : 0.005"  # scripted group (container) (typed FeaturePython)
  n = 0.002
FEATURE [App::DocumentObjectGroupPython] Cl_element003  label="Cl_element : 0.004"  # scripted group (container) (typed FeaturePython)
  n = 0.003
FEATURE [App::DocumentObjectGroupPython] K_element002  label="K_element : 0.003"  # scripted group (container) (typed FeaturePython)
  n = 0.003
FEATURE [App::DocumentObjectGroupPython] G4_BRAIN_ICRP  # scripted group (container) (typed FeaturePython)
  Dunit = g/cm3
  Dvalue = 1.04
  Group = -> [H_element017,C_element018,N_element012,O_element017,Na_element004,P_element004,S_element006,Cl_element003,K_element002]
  conduct = 2
  density = 1
  expand = 3
  formula = G4_BRAIN_ICRP
  name = G4_BRAIN_ICRP
  specific = 4
FEATURE [App::DocumentObjectGroupPython] C_element019  label="C_element : 4"  # scripted group (container) (typed FeaturePython)
  n = 4
  ref = C_element
FEATURE [App::DocumentObjectGroupPython] H_element018  label="H_element : 010"  # scripted group (container) (typed FeaturePython)
  n = 10
  ref = H_element
FEATURE [App::DocumentObjectGroupPython] G4_BUTANE  # scripted group (container) (typed FeaturePython)
  Dunit = g/cm3
  Dvalue = 0.00249343
  Group = -> [C_element019,H_element018]
  conduct = 2
  density = 1
  expand = 3
  formula = G4_BUTANE
  name = G4_BUTANE
  specific = 4
FEATURE [App::DocumentObjectGroupPython] C_element020  label="C_element : 008"  # scripted group (container) (typed FeaturePython)
  n = 4
  ref = C_element
FEATURE [App::DocumentObjectGroupPython] H_element019  label="H_element : 011"  # scripted group (container) (typed FeaturePython)
  n = 10
  ref = H_element
FEATURE [App::DocumentObjectGroupPython] O_element018  label="O_element : 007"  # scripted group (container) (typed FeaturePython)
  n = 1
  ref = O_element
FEATURE [App::DocumentObjectGroupPython] G4_N_BUTYL_ALCOHOL  label="G4_N-BUTYL_ALCOHOL"  # scripted group (container) (typed FeaturePython)
  Dunit = g/cm3
  Dvalue = 0.8098
  Group = -> [C_element020,H_element019,O_element018]
  conduct = 2
  density = 1
  expand = 3
  formula = G4_N-BUTYL_ALCOHOL
  name = G4_N-BUTYL_ALCOHOL
  specific = 4
FEATURE [App::DocumentObjectGroupPython] H_element020  label="H_element : 0.025"  # scripted group (container) (typed FeaturePython)
  n = 0.02468
FEATURE [App::DocumentObjectGroupPython] C_element021  label="C_element : 0.502"  # scripted group (container) (typed FeaturePython)
  n = 0.501611
FEATURE [App::DocumentObjectGroupPython] O_element019  label="O_element : 0.005"  # scripted group (container) (typed FeaturePython)
  n = 0.004527
FEATURE [App::DocumentObjectGroupPython] F_element004  label="F_element : 0.465"  # scripted group (container) (typed FeaturePython)
  n = 0.465209
FEATURE [App::DocumentObjectGroupPython] Si_element001  label="Si_element : 0.004"  # scripted group (container) (typed FeaturePython)
  n = 0.003973
FEATURE [App::DocumentObjectGroupPython] G4_C_552  label="G4_C-552"  # scripted group (container) (typed FeaturePython)
  Dunit = g/cm3
  Dvalue = 1.76
  Group = -> [H_element020,C_element021,O_element019,F_element004,Si_element001]
  conduct = 2
  density = 1
  expand = 3
  formula = G4_C-552
  name = G4_C-552
  specific = 4
FEATURE [App::DocumentObjectGroupPython] Cd_element001  label="Cd_element : 1"  # scripted group (container) (typed FeaturePython)
  n = 1
  ref = Cd_element
FEATURE [App::DocumentObjectGroupPython] Te_element001  label="Te_element : 1"  # scripted group (container) (typed FeaturePython)
  n = 1
  ref = Te_element
FEATURE [App::DocumentObjectGroupPython] G4_CADMIUM_TELLURIDE  # scripted group (container) (typed FeaturePython)
  Dunit = g/cm3
  Dvalue = 6.2
  Group = -> [Cd_element001,Te_element001]
  conduct = 2
  density = 1
  expand = 3
  formula = G4_CADMIUM_TELLURIDE
  name = G4_CADMIUM_TELLURIDE
  specific = 4
FEATURE [App::DocumentObjectGroupPython] Cd_element002  label="Cd_element : 002"  # scripted group (container) (typed FeaturePython)
  n = 1
  ref = Cd_element
FEATURE [App::DocumentObjectGroupPython] W_element001  label="W_element : 1"  # scripted group (container) (typed FeaturePython)
  n = 1
  ref = W_element
FEATURE [App::DocumentObjectGroupPython] O_element020  label="O_element : 008"  # scripted group (container) (typed FeaturePython)
  n = 4
  ref = O_element
FEATURE [App::DocumentObjectGroupPython] G4_CADMIUM_TUNGSTATE  # scripted group (container) (typed FeaturePython)
  Dunit = g/cm3
  Dvalue = 7.9
  Group = -> [Cd_element002,W_element001,O_element020]
  conduct = 2
  density = 1
  expand = 3
  formula = G4_CADMIUM_TUNGSTATE
  name = G4_CADMIUM_TUNGSTATE
  specific = 4
FEATURE [App::DocumentObjectGroupPython] Ca_element005  label="Ca_element : 1"  # scripted group (container) (typed FeaturePython)
  n = 1
  ref = Ca_element
FEATURE [App::DocumentObjectGroupPython] C_element022  label="C_element : 009"  # scripted group (container) (typed FeaturePython)
  n = 1
  ref = C_element
FEATURE [App::DocumentObjectGroupPython] O_element021  label="O_element : 009"  # scripted group (container) (typed FeaturePython)
  n = 3
  ref = O_element
FEATURE [App::DocumentObjectGroupPython] G4_CALCIUM_CARBONATE  # scripted group (container) (typed FeaturePython)
  Dunit = g/cm3
  Dvalue = 2.8
  Group = -> [Ca_element005,C_element022,O_element021]
  conduct = 2
  density = 1
  expand = 3
  formula = G4_CALCIUM_CARBONATE
  name = G4_CALCIUM_CARBONATE
  specific = 4
FEATURE [App::DocumentObjectGroupPython] Ca_element006  label="Ca_element : 002"  # scripted group (container) (typed FeaturePython)
  n = 1
  ref = Ca_element
FEATURE [App::DocumentObjectGroupPython] F_element005  label="F_element : 003"  # scripted group (container) (typed FeaturePython)
  n = 2
  ref = F_element
FEATURE [App::DocumentObjectGroupPython] G4_CALCIUM_FLUORIDE  # scripted group (container) (typed FeaturePython)
  Dunit = g/cm3
  Dvalue = 3.18
  Group = -> [Ca_element006,F_element005]
  conduct = 2
  density = 1
  expand = 3
  formula = G4_CALCIUM_FLUORIDE
  name = G4_CALCIUM_FLUORIDE
  specific = 4
FEATURE [App::DocumentObjectGroupPython] Ca_element007  label="Ca_element : 003"  # scripted group (container) (typed FeaturePython)
  n = 1
  ref = Ca_element
FEATURE [App::DocumentObjectGroupPython] O_element022  label="O_element : 010"  # scripted group (container) (typed FeaturePython)
  n = 1
  ref = O_element
FEATURE [App::DocumentObjectGroupPython] G4_CALCIUM_OXIDE  # scripted group (container) (typed FeaturePython)
  Dunit = g/cm3
  Dvalue = 3.3
  Group = -> [Ca_element007,O_element022]
  conduct = 2
  density = 1
  expand = 3
  formula = G4_CALCIUM_OXIDE
  name = G4_CALCIUM_OXIDE
  specific = 4
FEATURE [App::DocumentObjectGroupPython] Ca_element008  label="Ca_element : 004"  # scripted group (container) (typed FeaturePython)
  n = 1
  ref = Ca_element
FEATURE [App::DocumentObjectGroupPython] S_element007  label="S_element : 002"  # scripted group (container) (typed FeaturePython)
  n = 1
  ref = S_element
FEATURE [App::DocumentObjectGroupPython] O_element023  label="O_element : 011"  # scripted group (container) (typed FeaturePython)
  n = 4
  ref = O_element
FEATURE [App::DocumentObjectGroupPython] G4_CALCIUM_SULFATE  # scripted group (container) (typed FeaturePython)
  Dunit = g/cm3
  Dvalue = 2.96
  Group = -> [Ca_element008,S_element007,O_element023]
  conduct = 2
  density = 1
  expand = 3
  formula = G4_CALCIUM_SULFATE
  name = G4_CALCIUM_SULFATE
  specific = 4
FEATURE [App::DocumentObjectGroupPython] Ca_element009  label="Ca_element : 005"  # scripted group (container) (typed FeaturePython)
  n = 1
  ref = Ca_element
FEATURE [App::DocumentObjectGroupPython] W_element002  label="W_element : 002"  # scripted group (container) (typed FeaturePython)
  n = 1
  ref = W_element
FEATURE [App::DocumentObjectGroupPython] O_element024  label="O_element : 012"  # scripted group (container) (typed FeaturePython)
  n = 4
  ref = O_element
FEATURE [App::DocumentObjectGroupPython] G4_CALCIUM_TUNGSTATE  # scripted group (container) (typed FeaturePython)
  Dunit = g/cm3
  Dvalue = 6.062
  Group = -> [Ca_element009,W_element002,O_element024]
  conduct = 2
  density = 1
  expand = 3
  formula = G4_CALCIUM_TUNGSTATE
  name = G4_CALCIUM_TUNGSTATE
  specific = 4
FEATURE [App::DocumentObjectGroupPython] C_element023  label="C_element : 010"  # scripted group (container) (typed FeaturePython)
  n = 1
  ref = C_element
FEATURE [App::DocumentObjectGroupPython] O_element025  label="O_element : 013"  # scripted group (container) (typed FeaturePython)
  n = 2
  ref = O_element
FEATURE [App::DocumentObjectGroupPython] G4_CARBON_DIOXIDE  # scripted group (container) (typed FeaturePython)
  Dunit = g/cm3
  Dvalue = 0.00184212
  Group = -> [C_element023,O_element025]
  conduct = 2
  density = 1
  expand = 3
  formula = G4_CARBON_DIOXIDE
  name = G4_CARBON_DIOXIDE
  specific = 4
FEATURE [App::DocumentObjectGroupPython] C_element024  label="C_element : 011"  # scripted group (container) (typed FeaturePython)
  n = 1
  ref = C_element
FEATURE [App::DocumentObjectGroupPython] Cl_element004  label="Cl_element : 4"  # scripted group (container) (typed FeaturePython)
  n = 4
  ref = Cl_element
FEATURE [App::DocumentObjectGroupPython] G4_CARBON_TETRACHLORIDE  # scripted group (container) (typed FeaturePython)
  Dunit = g/cm3
  Dvalue = 1.594
  Group = -> [C_element024,Cl_element004]
  conduct = 2
  density = 1
  expand = 3
  formula = G4_CARBON_TETRACHLORIDE
  name = G4_CARBON_TETRACHLORIDE
  specific = 4
FEATURE [App::DocumentObjectGroupPython] C_element025  label="C_element : 012"  # scripted group (container) (typed FeaturePython)
  n = 6
  ref = C_element
FEATURE [App::DocumentObjectGroupPython] H_element021  label="H_element : 012"  # scripted group (container) (typed FeaturePython)
  n = 10
  ref = H_element
FEATURE [App::DocumentObjectGroupPython] O_element026  label="O_element : 5"  # scripted group (container) (typed FeaturePython)
  n = 5
  ref = O_element
FEATURE [App::DocumentObjectGroupPython] G4_CELLULOSE_CELLOPHANE  # scripted group (container) (typed FeaturePython)
  Dunit = g/cm3
  Dvalue = 1.42
  Group = -> [C_element025,H_element021,O_element026]
  conduct = 2
  density = 1
  expand = 3
  formula = G4_CELLULOSE_CELLOPHANE
  name = G4_CELLULOSE_CELLOPHANE
  specific = 4
FEATURE [App::DocumentObjectGroupPython] H_element022  label="H_element : 0.067"  # scripted group (container) (typed FeaturePython)
  n = 0.067125
FEATURE [App::DocumentObjectGroupPython] C_element026  label="C_element : 0.545"  # scripted group (container) (typed FeaturePython)
  n = 0.545403
FEATURE [App::DocumentObjectGroupPython] O_element027  label="O_element : 0.387"  # scripted group (container) (typed FeaturePython)
  n = 0.387472
FEATURE [App::DocumentObjectGroupPython] G4_CELLULOSE_BUTYRATE  # scripted group (container) (typed FeaturePython)
  Dunit = g/cm3
  Dvalue = 1.2
  Group = -> [H_element022,C_element026,O_element027]
  conduct = 2
  density = 1
  expand = 3
  formula = G4_CELLULOSE_BUTYRATE
  name = G4_CELLULOSE_BUTYRATE
  specific = 4
FEATURE [App::DocumentObjectGroupPython] H_element023  label="H_element : 0.029"  # scripted group (container) (typed FeaturePython)
  n = 0.029216
FEATURE [App::DocumentObjectGroupPython] C_element027  label="C_element : 0.271"  # scripted group (container) (typed FeaturePython)
  n = 0.271296
FEATURE [App::DocumentObjectGroupPython] N_element013  label="N_element : 0.121"  # scripted group (container) (typed FeaturePython)
  n = 0.121276
FEATURE [App::DocumentObjectGroupPython] O_element028  label="O_element : 0.578"  # scripted group (container) (typed FeaturePython)
  n = 0.578212
FEATURE [App::DocumentObjectGroupPython] G4_CELLULOSE_NITRATE  # scripted group (container) (typed FeaturePython)
  Dunit = g/cm3
  Dvalue = 1.49
  Group = -> [H_element023,C_element027,N_element013,O_element028]
  conduct = 2
  density = 1
  expand = 3
  formula = G4_CELLULOSE_NITRATE
  name = G4_CELLULOSE_NITRATE
  specific = 4
FEATURE [App::DocumentObjectGroupPython] H_element024  label="H_element : 0.108"  # scripted group (container) (typed FeaturePython)
  n = 0.107596
FEATURE [App::DocumentObjectGroupPython] N_element014  label="N_element : 0.001"  # scripted group (container) (typed FeaturePython)
  n = 0.0008
FEATURE [App::DocumentObjectGroupPython] O_element029  label="O_element : 0.875"  # scripted group (container) (typed FeaturePython)
  n = 0.874976
FEATURE [App::DocumentObjectGroupPython] S_element008  label="S_element : 0.015"  # scripted group (container) (typed FeaturePython)
  n = 0.014627
FEATURE [App::DocumentObjectGroupPython] Ce_element001  label="Ce_element : 0.002"  # scripted group (container) (typed FeaturePython)
  n = 0.002001
FEATURE [App::DocumentObjectGroupPython] G4_CERIC_SULFATE  # scripted group (container) (typed FeaturePython)
  Dunit = g/cm3
  Dvalue = 1.03
  Group = -> [H_element024,N_element014,O_element029,S_element008,Ce_element001]
  conduct = 2
  density = 1
  expand = 3
  formula = G4_CERIC_SULFATE
  name = G4_CERIC_SULFATE
  specific = 4
FEATURE [App::DocumentObjectGroupPython] Cs_element001  label="Cs_element : 1"  # scripted group (container) (typed FeaturePython)
  n = 1
  ref = Cs_element
FEATURE [App::DocumentObjectGroupPython] F_element006  label="F_element : 1"  # scripted group (container) (typed FeaturePython)
  n = 1
  ref = F_element
FEATURE [App::DocumentObjectGroupPython] G4_CESIUM_FLUORIDE  # scripted group (container) (typed FeaturePython)
  Dunit = g/cm3
  Dvalue = 4.115
  Group = -> [Cs_element001,F_element006]
  conduct = 2
  density = 1
  expand = 3
  formula = G4_CESIUM_FLUORIDE
  name = G4_CESIUM_FLUORIDE
  specific = 4
FEATURE [App::DocumentObjectGroupPython] Cs_element002  label="Cs_element : 002"  # scripted group (container) (typed FeaturePython)
  n = 1
  ref = Cs_element
FEATURE [App::DocumentObjectGroupPython] I_element001  label="I_element : 1"  # scripted group (container) (typed FeaturePython)
  n = 1
  ref = I_element
FEATURE [App::DocumentObjectGroupPython] G4_CESIUM_IODIDE  # scripted group (container) (typed FeaturePython)
  Dunit = g/cm3
  Dvalue = 4.51
  Group = -> [Cs_element002,I_element001]
  conduct = 2
  density = 1
  expand = 3
  formula = G4_CESIUM_IODIDE
  name = G4_CESIUM_IODIDE
  specific = 4
FEATURE [App::DocumentObjectGroupPython] C_element028  label="C_element : 013"  # scripted group (container) (typed FeaturePython)
  n = 6
  ref = C_element
FEATURE [App::DocumentObjectGroupPython] H_element025  label="H_element : 013"  # scripted group (container) (typed FeaturePython)
  n = 5
  ref = H_element
FEATURE [App::DocumentObjectGroupPython] Cl_element005  label="Cl_element : 1"  # scripted group (container) (typed FeaturePython)
  n = 1
  ref = Cl_element
FEATURE [App::DocumentObjectGroupPython] G4_CHLOROBENZENE  # scripted group (container) (typed FeaturePython)
  Dunit = g/cm3
  Dvalue = 1.1058
  Group = -> [C_element028,H_element025,Cl_element005]
  conduct = 2
  density = 1
  expand = 3
  formula = G4_CHLOROBENZENE
  name = G4_CHLOROBENZENE
  specific = 4
FEATURE [App::DocumentObjectGroupPython] C_element029  label="C_element : 014"  # scripted group (container) (typed FeaturePython)
  n = 1
  ref = C_element
FEATURE [App::DocumentObjectGroupPython] H_element026  label="H_element : 1"  # scripted group (container) (typed FeaturePython)
  n = 1
  ref = H_element
FEATURE [App::DocumentObjectGroupPython] Cl_element006  label="Cl_element : 3"  # scripted group (container) (typed FeaturePython)
  n = 3
  ref = Cl_element
FEATURE [App::DocumentObjectGroupPython] G4_CHLOROFORM  # scripted group (container) (typed FeaturePython)
  Dunit = g/cm3
  Dvalue = 1.4832
  Group = -> [C_element029,H_element026,Cl_element006]
  conduct = 2
  density = 1
  expand = 3
  formula = G4_CHLOROFORM
  name = G4_CHLOROFORM
  specific = 4
FEATURE [App::DocumentObjectGroupPython] H_element027  label="H_element : 0.010"  # scripted group (container) (typed FeaturePython)
  n = 0.01
FEATURE [App::DocumentObjectGroupPython] C_element030  label="C_element : 0.001"  # scripted group (container) (typed FeaturePython)
  n = 0.001
FEATURE [App::DocumentObjectGroupPython] O_element030  label="O_element : 0.529"  # scripted group (container) (typed FeaturePython)
  n = 0.529107
FEATURE [App::DocumentObjectGroupPython] Na_element005  label="Na_element : 0.016"  # scripted group (container) (typed FeaturePython)
  n = 0.016
FEATURE [App::DocumentObjectGroupPython] Mg_element003  label="Mg_element : 0.004"  # scripted group (container) (typed FeaturePython)
  n = 0.002
FEATURE [App::DocumentObjectGroupPython] Al_element002  label="Al_element : 0.034"  # scripted group (container) (typed FeaturePython)
  n = 0.033872
FEATURE [App::DocumentObjectGroupPython] Si_element002  label="Si_element : 0.337"  # scripted group (container) (typed FeaturePython)
  n = 0.337021
FEATURE [App::DocumentObjectGroupPython] K_element003  label="K_element : 0.013"  # scripted group (container) (typed FeaturePython)
  n = 0.013
FEATURE [App::DocumentObjectGroupPython] Ca_element010  label="Ca_element : 0.044"  # scripted group (container) (typed FeaturePython)
  n = 0.044
FEATURE [App::DocumentObjectGroupPython] Fe_element002  label="Fe_element : 0.014"  # scripted group (container) (typed FeaturePython)
  n = 0.014
FEATURE [App::DocumentObjectGroupPython] G4_CONCRETE  # scripted group (container) (typed FeaturePython)
  Dunit = g/cm3
  Dvalue = 2.3
  Group = -> [H_element027,C_element030,O_element030,Na_element005,Mg_element003,Al_element002,Si_element002,K_element003,Ca_element010,Fe_element002]
  conduct = 2
  density = 1
  expand = 3
  formula = G4_CONCRETE
  name = G4_CONCRETE
  specific = 4
FEATURE [App::DocumentObjectGroupPython] C_element031  label="C_element : 015"  # scripted group (container) (typed FeaturePython)
  n = 6
  ref = C_element
FEATURE [App::DocumentObjectGroupPython] H_element028  label="H_element : 12"  # scripted group (container) (typed FeaturePython)
  n = 12
  ref = H_element
FEATURE [App::DocumentObjectGroupPython] G4_CYCLOHEXANE  # scripted group (container) (typed FeaturePython)
  Dunit = g/cm3
  Dvalue = 0.779
  Group = -> [C_element031,H_element028]
  conduct = 2
  density = 1
  expand = 3
  formula = G4_CYCLOHEXANE
  name = G4_CYCLOHEXANE
  specific = 4
FEATURE [App::DocumentObjectGroupPython] C_element032  label="C_element : 016"  # scripted group (container) (typed FeaturePython)
  n = 6
  ref = C_element
FEATURE [App::DocumentObjectGroupPython] H_element029  label="H_element : 4"  # scripted group (container) (typed FeaturePython)
  n = 4
  ref = H_element
FEATURE [App::DocumentObjectGroupPython] Cl_element007  label="Cl_element : 2"  # scripted group (container) (typed FeaturePython)
  n = 2
  ref = Cl_element
FEATURE [App::DocumentObjectGroupPython] G4_1_2_DICHLOROBENZENE  label="G4_1.2-DICHLOROBENZENE"  # scripted group (container) (typed FeaturePython)
  Dunit = g/cm3
  Dvalue = 1.3048
  Group = -> [C_element032,H_element029,Cl_element007]
  conduct = 2
  density = 1
  expand = 3
  formula = G4_1.2-DICHLOROBENZENE
  name = G4_1.2-DICHLOROBENZENE
  specific = 4
FEATURE [App::DocumentObjectGroupPython] C_element033  label="C_element : 017"  # scripted group (container) (typed FeaturePython)
  n = 4
  ref = C_element
FEATURE [App::DocumentObjectGroupPython] H_element030  label="H_element : 8"  # scripted group (container) (typed FeaturePython)
  n = 8
  ref = H_element
FEATURE [App::DocumentObjectGroupPython] O_element031  label="O_element : 014"  # scripted group (container) (typed FeaturePython)
  n = 1
  ref = O_element
FEATURE [App::DocumentObjectGroupPython] Cl_element008  label="Cl_element : 005"  # scripted group (container) (typed FeaturePython)
  n = 2
  ref = Cl_element
FEATURE [App::DocumentObjectGroupPython] G4_DICHLORODIETHYL_ETHER  # scripted group (container) (typed FeaturePython)
  Dunit = g/cm3
  Dvalue = 1.2199
  Group = -> [C_element033,H_element030,O_element031,Cl_element008]
  conduct = 2
  density = 1
  expand = 3
  formula = G4_DICHLORODIETHYL_ETHER
  name = G4_DICHLORODIETHYL_ETHER
  specific = 4
FEATURE [App::DocumentObjectGroupPython] C_element034  label="C_element : 018"  # scripted group (container) (typed FeaturePython)
  n = 2
  ref = C_element
FEATURE [App::DocumentObjectGroupPython] H_element031  label="H_element : 014"  # scripted group (container) (typed FeaturePython)
  n = 4
  ref = H_element
FEATURE [App::DocumentObjectGroupPython] Cl_element009  label="Cl_element : 006"  # scripted group (container) (typed FeaturePython)
  n = 2
  ref = Cl_element
FEATURE [App::DocumentObjectGroupPython] G4_1_2_DICHLOROETHANE  label="G4_1.2-DICHLOROETHANE"  # scripted group (container) (typed FeaturePython)
  Dunit = g/cm3
  Dvalue = 1.2351
  Group = -> [C_element034,H_element031,Cl_element009]
  conduct = 2
  density = 1
  expand = 3
  formula = G4_1.2-DICHLOROETHANE
  name = G4_1.2-DICHLOROETHANE
  specific = 4
FEATURE [App::DocumentObjectGroupPython] C_element035  label="C_element : 019"  # scripted group (container) (typed FeaturePython)
  n = 4
  ref = C_element
FEATURE [App::DocumentObjectGroupPython] H_element032  label="H_element : 015"  # scripted group (container) (typed FeaturePython)
  n = 10
  ref = H_element
FEATURE [App::DocumentObjectGroupPython] O_element032  label="O_element : 015"  # scripted group (container) (typed FeaturePython)
  n = 1
  ref = O_element
FEATURE [App::DocumentObjectGroupPython] G4_DIETHYL_ETHER  # scripted group (container) (typed FeaturePython)
  Dunit = g/cm3
  Dvalue = 0.71378
  Group = -> [C_element035,H_element032,O_element032]
  conduct = 2
  density = 1
  expand = 3
  formula = G4_DIETHYL_ETHER
  name = G4_DIETHYL_ETHER
  specific = 4
FEATURE [App::DocumentObjectGroupPython] C_element036  label="C_element : 020"  # scripted group (container) (typed FeaturePython)
  n = 3
  ref = C_element
FEATURE [App::DocumentObjectGroupPython] H_element033  label="H_element : 016"  # scripted group (container) (typed FeaturePython)
  n = 7
  ref = H_element
FEATURE [App::DocumentObjectGroupPython] N_element015  label="N_element : 008"  # scripted group (container) (typed FeaturePython)
  n = 1
  ref = N_element
FEATURE [App::DocumentObjectGroupPython] O_element033  label="O_element : 016"  # scripted group (container) (typed FeaturePython)
  n = 1
  ref = O_element
FEATURE [App::DocumentObjectGroupPython] G4_N_N_DIMETHYL_FORMAMIDE  label="G4_N.N-DIMETHYL_FORMAMIDE"  # scripted group (container) (typed FeaturePython)
  Dunit = g/cm3
  Dvalue = 0.9487
  Group = -> [C_element036,H_element033,N_element015,O_element033]
  conduct = 2
  density = 1
  expand = 3
  formula = G4_N.N-DIMETHYL_FORMAMIDE
  name = G4_N.N-DIMETHYL_FORMAMIDE
  specific = 4
FEATURE [App::DocumentObjectGroupPython] C_element037  label="C_element : 021"  # scripted group (container) (typed FeaturePython)
  n = 2
  ref = C_element
FEATURE [App::DocumentObjectGroupPython] H_element034  label="H_element : 017"  # scripted group (container) (typed FeaturePython)
  n = 6
  ref = H_element
FEATURE [App::DocumentObjectGroupPython] O_element034  label="O_element : 017"  # scripted group (container) (typed FeaturePython)
  n = 1
  ref = O_element
FEATURE [App::DocumentObjectGroupPython] S_element009  label="S_element : 003"  # scripted group (container) (typed FeaturePython)
  n = 1
  ref = S_element
FEATURE [App::DocumentObjectGroupPython] G4_DIMETHYL_SULFOXIDE  # scripted group (container) (typed FeaturePython)
  Dunit = g/cm3
  Dvalue = 1.1014
  Group = -> [C_element037,H_element034,O_element034,S_element009]
  conduct = 2
  density = 1
  expand = 3
  formula = G4_DIMETHYL_SULFOXIDE
  name = G4_DIMETHYL_SULFOXIDE
  specific = 4
FEATURE [App::DocumentObjectGroupPython] C_element038  label="C_element : 022"  # scripted group (container) (typed FeaturePython)
  n = 2
  ref = C_element
FEATURE [App::DocumentObjectGroupPython] H_element035  label="H_element : 018"  # scripted group (container) (typed FeaturePython)
  n = 6
  ref = H_element
FEATURE [App::DocumentObjectGroupPython] G4_ETHANE  # scripted group (container) (typed FeaturePython)
  Dunit = g/cm3
  Dvalue = 0.00125324
  Group = -> [C_element038,H_element035]
  conduct = 2
  density = 1
  expand = 3
  formula = G4_ETHANE
  name = G4_ETHANE
  specific = 4
FEATURE [App::DocumentObjectGroupPython] C_element039  label="C_element : 023"  # scripted group (container) (typed FeaturePython)
  n = 2
  ref = C_element
FEATURE [App::DocumentObjectGroupPython] H_element036  label="H_element : 019"  # scripted group (container) (typed FeaturePython)
  n = 6
  ref = H_element
FEATURE [App::DocumentObjectGroupPython] O_element035  label="O_element : 018"  # scripted group (container) (typed FeaturePython)
  n = 1
  ref = O_element
FEATURE [App::DocumentObjectGroupPython] G4_ETHYL_ALCOHOL  # scripted group (container) (typed FeaturePython)
  Dunit = g/cm3
  Dvalue = 0.7893
  Group = -> [C_element039,H_element036,O_element035]
  conduct = 2
  density = 1
  expand = 3
  formula = G4_ETHYL_ALCOHOL
  name = G4_ETHYL_ALCOHOL
  specific = 4
FEATURE [App::DocumentObjectGroupPython] H_element037  label="H_element : 0.090"  # scripted group (container) (typed FeaturePython)
  n = 0.090027
FEATURE [App::DocumentObjectGroupPython] C_element040  label="C_element : 0.585"  # scripted group (container) (typed FeaturePython)
  n = 0.585182
FEATURE [App::DocumentObjectGroupPython] O_element036  label="O_element : 0.325"  # scripted group (container) (typed FeaturePython)
  n = 0.324791
FEATURE [App::DocumentObjectGroupPython] G4_ETHYL_CELLULOSE  # scripted group (container) (typed FeaturePython)
  Dunit = g/cm3
  Dvalue = 1.13
  Group = -> [H_element037,C_element040,O_element036]
  conduct = 2
  density = 1
  expand = 3
  formula = G4_ETHYL_CELLULOSE
  name = G4_ETHYL_CELLULOSE
  specific = 4
FEATURE [App::DocumentObjectGroupPython] C_element041  label="C_element : 024"  # scripted group (container) (typed FeaturePython)
  n = 2
  ref = C_element
FEATURE [App::DocumentObjectGroupPython] H_element038  label="H_element : 020"  # scripted group (container) (typed FeaturePython)
  n = 4
  ref = H_element
FEATURE [App::DocumentObjectGroupPython] G4_ETHYLENE  # scripted group (container) (typed FeaturePython)
  Dunit = g/cm3
  Dvalue = 0.00117497
  Group = -> [C_element041,H_element038]
  conduct = 2
  density = 1
  expand = 3
  formula = G4_ETHYLENE
  name = G4_ETHYLENE
  specific = 4
FEATURE [App::DocumentObjectGroupPython] H_element039  label="H_element : 0.096"  # scripted group (container) (typed FeaturePython)
  n = 0.096
FEATURE [App::DocumentObjectGroupPython] C_element042  label="C_element : 0.195"  # scripted group (container) (typed FeaturePython)
  n = 0.195
FEATURE [App::DocumentObjectGroupPython] N_element016  label="N_element : 0.057"  # scripted group (container) (typed FeaturePython)
  n = 0.057
FEATURE [App::DocumentObjectGroupPython] O_element037  label="O_element : 0.646"  # scripted group (container) (typed FeaturePython)
  n = 0.646
FEATURE [App::DocumentObjectGroupPython] Na_element006  label="Na_element : 0.017"  # scripted group (container) (typed FeaturePython)
  n = 0.001
FEATURE [App::DocumentObjectGroupPython] P_element005  label="P_element : 0.104"  # scripted group (container) (typed FeaturePython)
  n = 0.001
FEATURE [App::DocumentObjectGroupPython] S_element010  label="S_element : 0.016"  # scripted group (container) (typed FeaturePython)
  n = 0.003
FEATURE [App::DocumentObjectGroupPython] Cl_element010  label="Cl_element : 0.005"  # scripted group (container) (typed FeaturePython)
  n = 0.001
FEATURE [App::DocumentObjectGroupPython] G4_EYE_LENS_ICRP  # scripted group (container) (typed FeaturePython)
  Dunit = g/cm3
  Dvalue = 1.07
  Group = -> [H_element039,C_element042,N_element016,O_element037,Na_element006,P_element005,S_element010,Cl_element010]
  conduct = 2
  density = 1
  expand = 3
  formula = G4_EYE_LENS_ICRP
  name = G4_EYE_LENS_ICRP
  specific = 4
FEATURE [App::DocumentObjectGroupPython] Fe_element003  label="Fe_element : 2"  # scripted group (container) (typed FeaturePython)
  n = 2
  ref = Fe_element
FEATURE [App::DocumentObjectGroupPython] O_element038  label="O_element : 019"  # scripted group (container) (typed FeaturePython)
  n = 3
  ref = O_element
FEATURE [App::DocumentObjectGroupPython] G4_FERRIC_OXIDE  # scripted group (container) (typed FeaturePython)
  Dunit = g/cm3
  Dvalue = 5.2
  Group = -> [Fe_element003,O_element038]
  conduct = 2
  density = 1
  expand = 3
  formula = G4_FERRIC_OXIDE
  name = G4_FERRIC_OXIDE
  specific = 4
FEATURE [App::DocumentObjectGroupPython] Fe_element004  label="Fe_element : 1"  # scripted group (container) (typed FeaturePython)
  n = 1
  ref = Fe_element
FEATURE [App::DocumentObjectGroupPython] B_element003  label="B_element : 1"  # scripted group (container) (typed FeaturePython)
  n = 1
  ref = B_element
FEATURE [App::DocumentObjectGroupPython] G4_FERROBORIDE  # scripted group (container) (typed FeaturePython)
  Dunit = g/cm3
  Dvalue = 7.15
  Group = -> [Fe_element004,B_element003]
  conduct = 2
  density = 1
  expand = 3
  formula = G4_FERROBORIDE
  name = G4_FERROBORIDE
  specific = 4
FEATURE [App::DocumentObjectGroupPython] Fe_element005  label="Fe_element : 003"  # scripted group (container) (typed FeaturePython)
  n = 1
  ref = Fe_element
FEATURE [App::DocumentObjectGroupPython] O_element039  label="O_element : 020"  # scripted group (container) (typed FeaturePython)
  n = 1
  ref = O_element
FEATURE [App::DocumentObjectGroupPython] G4_FERROUS_OXIDE  # scripted group (container) (typed FeaturePython)
  Dunit = g/cm3
  Dvalue = 5.7
  Group = -> [Fe_element005,O_element039]
  conduct = 2
  density = 1
  expand = 3
  formula = G4_FERROUS_OXIDE
  name = G4_FERROUS_OXIDE
  specific = 4
FEATURE [App::DocumentObjectGroupPython] H_element040  label="H_element : 0.115"  # scripted group (container) (typed FeaturePython)
  n = 0.108259
FEATURE [App::DocumentObjectGroupPython] N_element017  label="N_element : 0.000"  # scripted group (container) (typed FeaturePython)
  n = 2.7e-05
FEATURE [App::DocumentObjectGroupPython] O_element040  label="O_element : 0.879"  # scripted group (container) (typed FeaturePython)
  n = 0.878636
FEATURE [App::DocumentObjectGroupPython] Na_element007  label="Na_element : 0.000"  # scripted group (container) (typed FeaturePython)
  n = 2.2e-05
FEATURE [App::DocumentObjectGroupPython] S_element011  label="S_element : 0.013"  # scripted group (container) (typed FeaturePython)
  n = 0.012968
FEATURE [App::DocumentObjectGroupPython] Cl_element011  label="Cl_element : 0.000"  # scripted group (container) (typed FeaturePython)
  n = 3.4e-05
FEATURE [App::DocumentObjectGroupPython] Fe_element006  label="Fe_element : 0.000"  # scripted group (container) (typed FeaturePython)
  n = 5.4e-05
FEATURE [App::DocumentObjectGroupPython] G4_FERROUS_SULFATE  # scripted group (container) (typed FeaturePython)
  Dunit = g/cm3
  Dvalue = 1.024
  Group = -> [H_element040,N_element017,O_element040,Na_element007,S_element011,Cl_element011,Fe_element006]
  conduct = 2
  density = 1
  expand = 3
  formula = G4_FERROUS_SULFATE
  name = G4_FERROUS_SULFATE
  specific = 4
FEATURE [App::DocumentObjectGroupPython] C_element043  label="C_element : 0.099"  # scripted group (container) (typed FeaturePython)
  n = 0.099335
FEATURE [App::DocumentObjectGroupPython] F_element007  label="F_element : 0.314"  # scripted group (container) (typed FeaturePython)
  n = 0.314247
FEATURE [App::DocumentObjectGroupPython] Cl_element012  label="Cl_element : 0.586"  # scripted group (container) (typed FeaturePython)
  n = 0.586418
FEATURE [App::DocumentObjectGroupPython] G4_FREON_12  label="G4_FREON-12"  # scripted group (container) (typed FeaturePython)
  Dunit = g/cm3
  Dvalue = 1.12
  Group = -> [C_element043,F_element007,Cl_element012]
  conduct = 2
  density = 1
  expand = 3
  formula = G4_FREON-12
  name = G4_FREON-12
  specific = 4
FEATURE [App::DocumentObjectGroupPython] C_element044  label="C_element : 0.057"  # scripted group (container) (typed FeaturePython)
  n = 0.057245
FEATURE [App::DocumentObjectGroupPython] F_element008  label="F_element : 0.181"  # scripted group (container) (typed FeaturePython)
  n = 0.181096
FEATURE [App::DocumentObjectGroupPython] Br_element001  label="Br_element : 0.762"  # scripted group (container) (typed FeaturePython)
  n = 0.761659
FEATURE [App::DocumentObjectGroupPython] G4_FREON_12B2  label="G4_FREON-12B2"  # scripted group (container) (typed FeaturePython)
  Dunit = g/cm3
  Dvalue = 1.8
  Group = -> [C_element044,F_element008,Br_element001]
  conduct = 2
  density = 1
  expand = 3
  formula = G4_FREON-12B2
  name = G4_FREON-12B2
  specific = 4
FEATURE [App::DocumentObjectGroupPython] C_element045  label="C_element : 0.115"  # scripted group (container) (typed FeaturePython)
  n = 0.114983
FEATURE [App::DocumentObjectGroupPython] F_element009  label="F_element : 0.546"  # scripted group (container) (typed FeaturePython)
  n = 0.545621
FEATURE [App::DocumentObjectGroupPython] Cl_element013  label="Cl_element : 0.339"  # scripted group (container) (typed FeaturePython)
  n = 0.339396
FEATURE [App::DocumentObjectGroupPython] G4_FREON_13  label="G4_FREON-13"  # scripted group (container) (typed FeaturePython)
  Dunit = g/cm3
  Dvalue = 0.95
  Group = -> [C_element045,F_element009,Cl_element013]
  conduct = 2
  density = 1
  expand = 3
  formula = G4_FREON-13
  name = G4_FREON-13
  specific = 4
FEATURE [App::DocumentObjectGroupPython] C_element046  label="C_element : 025"  # scripted group (container) (typed FeaturePython)
  n = 1
  ref = C_element
FEATURE [App::DocumentObjectGroupPython] F_element010  label="F_element : 3"  # scripted group (container) (typed FeaturePython)
  n = 3
  ref = F_element
FEATURE [App::DocumentObjectGroupPython] Br_element002  label="Br_element : 1"  # scripted group (container) (typed FeaturePython)
  n = 1
  ref = Br_element
FEATURE [App::DocumentObjectGroupPython] G4_FREON_13B1  label="G4_FREON-13B1"  # scripted group (container) (typed FeaturePython)
  Dunit = g/cm3
  Dvalue = 1.5
  Group = -> [C_element046,F_element010,Br_element002]
  conduct = 2
  density = 1
  expand = 3
  formula = G4_FREON-13B1
  name = G4_FREON-13B1
  specific = 4
FEATURE [App::DocumentObjectGroupPython] C_element047  label="C_element : 0.061"  # scripted group (container) (typed FeaturePython)
  n = 0.061309
FEATURE [App::DocumentObjectGroupPython] F_element011  label="F_element : 0.291"  # scripted group (container) (typed FeaturePython)
  n = 0.290924
FEATURE [App::DocumentObjectGroupPython] I_element002  label="I_element : 0.648"  # scripted group (container) (typed FeaturePython)
  n = 0.647767
FEATURE [App::DocumentObjectGroupPython] G4_FREON_13I1  label="G4_FREON-13I1"  # scripted group (container) (typed FeaturePython)
  Dunit = g/cm3
  Dvalue = 1.8
  Group = -> [C_element047,F_element011,I_element002]
  conduct = 2
  density = 1
  expand = 3
  formula = G4_FREON-13I1
  name = G4_FREON-13I1
  specific = 4
FEATURE [App::DocumentObjectGroupPython] Gd_element001  label="Gd_element : 2"  # scripted group (container) (typed FeaturePython)
  n = 2
  ref = Gd_element
FEATURE [App::DocumentObjectGroupPython] O_element041  label="O_element : 021"  # scripted group (container) (typed FeaturePython)
  n = 2
  ref = O_element
FEATURE [App::DocumentObjectGroupPython] S_element012  label="S_element : 004"  # scripted group (container) (typed FeaturePython)
  n = 1
  ref = S_element
FEATURE [App::DocumentObjectGroupPython] G4_GADOLINIUM_OXYSULFIDE  # scripted group (container) (typed FeaturePython)
  Dunit = g/cm3
  Dvalue = 7.44
  Group = -> [Gd_element001,O_element041,S_element012]
  conduct = 2
  density = 1
  expand = 3
  formula = G4_GADOLINIUM_OXYSULFIDE
  name = G4_GADOLINIUM_OXYSULFIDE
  specific = 4
FEATURE [App::DocumentObjectGroupPython] Ga_element001  label="Ga_element : 1"  # scripted group (container) (typed FeaturePython)
  n = 1
  ref = Ga_element
FEATURE [App::DocumentObjectGroupPython] As_element001  label="As_element : 1"  # scripted group (container) (typed FeaturePython)
  n = 1
  ref = As_element
FEATURE [App::DocumentObjectGroupPython] G4_GALLIUM_ARSENIDE  # scripted group (container) (typed FeaturePython)
  Dunit = g/cm3
  Dvalue = 5.31
  Group = -> [Ga_element001,As_element001]
  conduct = 2
  density = 1
  expand = 3
  formula = G4_GALLIUM_ARSENIDE
  name = G4_GALLIUM_ARSENIDE
  specific = 4
FEATURE [App::DocumentObjectGroupPython] H_element041  label="H_element : 0.081"  # scripted group (container) (typed FeaturePython)
  n = 0.08118
FEATURE [App::DocumentObjectGroupPython] C_element048  label="C_element : 0.416"  # scripted group (container) (typed FeaturePython)
  n = 0.41606
FEATURE [App::DocumentObjectGroupPython] N_element018  label="N_element : 0.111"  # scripted group (container) (typed FeaturePython)
  n = 0.11124
FEATURE [App::DocumentObjectGroupPython] O_element042  label="O_element : 0.381"  # scripted group (container) (typed FeaturePython)
  n = 0.38064
FEATURE [App::DocumentObjectGroupPython] S_element013  label="S_element : 0.011"  # scripted group (container) (typed FeaturePython)
  n = 0.01088
FEATURE [App::DocumentObjectGroupPython] G4_GEL_PHOTO_EMULSION  # scripted group (container) (typed FeaturePython)
  Dunit = g/cm3
  Dvalue = 1.2914
  Group = -> [H_element041,C_element048,N_element018,O_element042,S_element013]
  conduct = 2
  density = 1
  expand = 3
  formula = G4_GEL_PHOTO_EMULSION
  name = G4_GEL_PHOTO_EMULSION
  specific = 4
FEATURE [App::DocumentObjectGroupPython] B_element004  label="B_element : 0.040"  # scripted group (container) (typed FeaturePython)
  n = 0.0400639
FEATURE [App::DocumentObjectGroupPython] O_element043  label="O_element : 0.540"  # scripted group (container) (typed FeaturePython)
  n = 0.539561
FEATURE [App::DocumentObjectGroupPython] Na_element008  label="Na_element : 0.028"  # scripted group (container) (typed FeaturePython)
  n = 0.0281909
FEATURE [App::DocumentObjectGroupPython] Al_element003  label="Al_element : 0.012"  # scripted group (container) (typed FeaturePython)
  n = 0.011644
FEATURE [App::DocumentObjectGroupPython] Si_element003  label="Si_element : 0.377"  # scripted group (container) (typed FeaturePython)
  n = 0.377219
FEATURE [App::DocumentObjectGroupPython] K_element004  label="K_element : 0.014"  # scripted group (container) (typed FeaturePython)
  n = 0.00332099
FEATURE [App::DocumentObjectGroupPython] G4_Pyrex_Glass  # scripted group (container) (typed FeaturePython)
  Dunit = g/cm3
  Dvalue = 2.23
  Group = -> [B_element004,O_element043,Na_element008,Al_element003,Si_element003,K_element004]
  conduct = 2
  density = 1
  expand = 3
  formula = G4_Pyrex_Glass
  name = G4_Pyrex_Glass
  specific = 4
FEATURE [App::DocumentObjectGroupPython] O_element044  label="O_element : 0.156"  # scripted group (container) (typed FeaturePython)
  n = 0.156453
FEATURE [App::DocumentObjectGroupPython] Si_element004  label="Si_element : 0.081"  # scripted group (container) (typed FeaturePython)
  n = 0.080866
FEATURE [App::DocumentObjectGroupPython] Ti_element001  label="Ti_element : 0.008"  # scripted group (container) (typed FeaturePython)
  n = 0.008092
FEATURE [App::DocumentObjectGroupPython] As_element002  label="As_element : 0.003"  # scripted group (container) (typed FeaturePython)
  n = 0.002651
FEATURE [App::DocumentObjectGroupPython] Pb_element001  label="Pb_element : 0.752"  # scripted group (container) (typed FeaturePython)
  n = 0.751938
FEATURE [App::DocumentObjectGroupPython] G4_GLASS_LEAD  # scripted group (container) (typed FeaturePython)
  Dunit = g/cm3
  Dvalue = 6.22
  Group = -> [O_element044,Si_element004,Ti_element001,As_element002,Pb_element001]
  conduct = 2
  density = 1
  expand = 3
  formula = G4_GLASS_LEAD
  name = G4_GLASS_LEAD
  specific = 4
FEATURE [App::DocumentObjectGroupPython] O_element045  label="O_element : 0.460"  # scripted group (container) (typed FeaturePython)
  n = 0.4598
FEATURE [App::DocumentObjectGroupPython] Na_element009  label="Na_element : 0.096"  # scripted group (container) (typed FeaturePython)
  n = 0.0964411
FEATURE [App::DocumentObjectGroupPython] Si_element005  label="Si_element : 0.378"  # scripted group (container) (typed FeaturePython)
  n = 0.336553
FEATURE [App::DocumentObjectGroupPython] Ca_element011  label="Ca_element : 0.107"  # scripted group (container) (typed FeaturePython)
  n = 0.107205
FEATURE [App::DocumentObjectGroupPython] G4_GLASS_PLATE  # scripted group (container) (typed FeaturePython)
  Dunit = g/cm3
  Dvalue = 2.4
  Group = -> [O_element045,Na_element009,Si_element005,Ca_element011]
  conduct = 2
  density = 1
  expand = 3
  formula = G4_GLASS_PLATE
  name = G4_GLASS_PLATE
  specific = 4
FEATURE [App::DocumentObjectGroupPython] C_element049  label="C_element : 026"  # scripted group (container) (typed FeaturePython)
  n = 5
  ref = C_element
FEATURE [App::DocumentObjectGroupPython] H_element042  label="H_element : 021"  # scripted group (container) (typed FeaturePython)
  n = 10
  ref = H_element
FEATURE [App::DocumentObjectGroupPython] N_element019  label="N_element : 2"  # scripted group (container) (typed FeaturePython)
  n = 2
  ref = N_element
FEATURE [App::DocumentObjectGroupPython] O_element046  label="O_element : 022"  # scripted group (container) (typed FeaturePython)
  n = 3
  ref = O_element
FEATURE [App::DocumentObjectGroupPython] G4_GLUTAMINE  # scripted group (container) (typed FeaturePython)
  Dunit = g/cm3
  Dvalue = 1.46
  Group = -> [C_element049,H_element042,N_element019,O_element046]
  conduct = 2
  density = 1
  expand = 3
  formula = G4_GLUTAMINE
  name = G4_GLUTAMINE
  specific = 4
FEATURE [App::DocumentObjectGroupPython] C_element050  label="C_element : 027"  # scripted group (container) (typed FeaturePython)
  n = 3
  ref = C_element
FEATURE [App::DocumentObjectGroupPython] H_element043  label="H_element : 022"  # scripted group (container) (typed FeaturePython)
  n = 8
  ref = H_element
FEATURE [App::DocumentObjectGroupPython] O_element047  label="O_element : 023"  # scripted group (container) (typed FeaturePython)
  n = 3
  ref = O_element
FEATURE [App::DocumentObjectGroupPython] G4_GLYCEROL  # scripted group (container) (typed FeaturePython)
  Dunit = g/cm3
  Dvalue = 1.2613
  Group = -> [C_element050,H_element043,O_element047]
  conduct = 2
  density = 1
  expand = 3
  formula = G4_GLYCEROL
  name = G4_GLYCEROL
  specific = 4
FEATURE [App::DocumentObjectGroupPython] C_element051  label="C_element : 028"  # scripted group (container) (typed FeaturePython)
  n = 5
  ref = C_element
FEATURE [App::DocumentObjectGroupPython] H_element044  label="H_element : 023"  # scripted group (container) (typed FeaturePython)
  n = 5
  ref = H_element
FEATURE [App::DocumentObjectGroupPython] N_element020  label="N_element : 009"  # scripted group (container) (typed FeaturePython)
  n = 5
  ref = N_element
FEATURE [App::DocumentObjectGroupPython] O_element048  label="O_element : 024"  # scripted group (container) (typed FeaturePython)
  n = 1
  ref = O_element
FEATURE [App::DocumentObjectGroupPython] G4_GUANINE  # scripted group (container) (typed FeaturePython)
  Dunit = g/cm3
  Dvalue = 2.2
  Group = -> [C_element051,H_element044,N_element020,O_element048]
  conduct = 2
  density = 1
  expand = 3
  formula = G4_GUANINE
  name = G4_GUANINE
  specific = 4
FEATURE [App::DocumentObjectGroupPython] Ca_element012  label="Ca_element : 006"  # scripted group (container) (typed FeaturePython)
  n = 1
  ref = Ca_element
FEATURE [App::DocumentObjectGroupPython] S_element014  label="S_element : 005"  # scripted group (container) (typed FeaturePython)
  n = 1
  ref = S_element
FEATURE [App::DocumentObjectGroupPython] O_element049  label="O_element : 6"  # scripted group (container) (typed FeaturePython)
  n = 6
  ref = O_element
FEATURE [App::DocumentObjectGroupPython] H_element045  label="H_element : 024"  # scripted group (container) (typed FeaturePython)
  n = 4
  ref = H_element
FEATURE [App::DocumentObjectGroupPython] G4_GYPSUM  # scripted group (container) (typed FeaturePython)
  Dunit = g/cm3
  Dvalue = 2.32
  Group = -> [Ca_element012,S_element014,O_element049,H_element045]
  conduct = 2
  density = 1
  expand = 3
  formula = G4_GYPSUM
  name = G4_GYPSUM
  specific = 4
FEATURE [App::DocumentObjectGroupPython] C_element052  label="C_element : 7"  # scripted group (container) (typed FeaturePython)
  n = 7
  ref = C_element
FEATURE [App::DocumentObjectGroupPython] H_element046  label="H_element : 16"  # scripted group (container) (typed FeaturePython)
  n = 16
  ref = H_element
FEATURE [App::DocumentObjectGroupPython] G4_N_HEPTANE  label="G4_N-HEPTANE"  # scripted group (container) (typed FeaturePython)
  Dunit = g/cm3
  Dvalue = 0.68376
  Group = -> [C_element052,H_element046]
  conduct = 2
  density = 1
  expand = 3
  formula = G4_N-HEPTANE
  name = G4_N-HEPTANE
  specific = 4
FEATURE [App::DocumentObjectGroupPython] C_element053  label="C_element : 029"  # scripted group (container) (typed FeaturePython)
  n = 6
  ref = C_element
FEATURE [App::DocumentObjectGroupPython] H_element047  label="H_element : 14"  # scripted group (container) (typed FeaturePython)
  n = 14
  ref = H_element
FEATURE [App::DocumentObjectGroupPython] G4_N_HEXANE  label="G4_N-HEXANE"  # scripted group (container) (typed FeaturePython)
  Dunit = g/cm3
  Dvalue = 0.6603
  Group = -> [C_element053,H_element047]
  conduct = 2
  density = 1
  expand = 3
  formula = G4_N-HEXANE
  name = G4_N-HEXANE
  specific = 4
FEATURE [App::DocumentObjectGroupPython] C_element054  label="C_element : 22"  # scripted group (container) (typed FeaturePython)
  n = 22
  ref = C_element
FEATURE [App::DocumentObjectGroupPython] H_element048  label="H_element : 025"  # scripted group (container) (typed FeaturePython)
  n = 10
  ref = H_element
FEATURE [App::DocumentObjectGroupPython] N_element021  label="N_element : 010"  # scripted group (container) (typed FeaturePython)
  n = 2
  ref = N_element
FEATURE [App::DocumentObjectGroupPython] O_element050  label="O_element : 025"  # scripted group (container) (typed FeaturePython)
  n = 5
  ref = O_element
FEATURE [App::DocumentObjectGroupPython] G4_KAPTON  # scripted group (container) (typed FeaturePython)
  Dunit = g/cm3
  Dvalue = 1.42
  Group = -> [C_element054,H_element048,N_element021,O_element050]
  conduct = 2
  density = 1
  expand = 3
  formula = G4_KAPTON
  name = G4_KAPTON
  specific = 4
FEATURE [App::DocumentObjectGroupPython] La_element001  label="La_element : 1"  # scripted group (container) (typed FeaturePython)
  n = 1
  ref = La_element
FEATURE [App::DocumentObjectGroupPython] Br_element003  label="Br_element : 002"  # scripted group (container) (typed FeaturePython)
  n = 1
  ref = Br_element
FEATURE [App::DocumentObjectGroupPython] O_element051  label="O_element : 026"  # scripted group (container) (typed FeaturePython)
  n = 1
  ref = O_element
FEATURE [App::DocumentObjectGroupPython] G4_LANTHANUM_OXYBROMIDE  # scripted group (container) (typed FeaturePython)
  Dunit = g/cm3
  Dvalue = 6.28
  Group = -> [La_element001,Br_element003,O_element051]
  conduct = 2
  density = 1
  expand = 3
  formula = G4_LANTHANUM_OXYBROMIDE
  name = G4_LANTHANUM_OXYBROMIDE
  specific = 4
FEATURE [App::DocumentObjectGroupPython] La_element002  label="La_element : 2"  # scripted group (container) (typed FeaturePython)
  n = 2
  ref = La_element
FEATURE [App::DocumentObjectGroupPython] O_element052  label="O_element : 027"  # scripted group (container) (typed FeaturePython)
  n = 2
  ref = O_element
FEATURE [App::DocumentObjectGroupPython] S_element015  label="S_element : 006"  # scripted group (container) (typed FeaturePython)
  n = 1
  ref = S_element
FEATURE [App::DocumentObjectGroupPython] G4_LANTHANUM_OXYSULFIDE  # scripted group (container) (typed FeaturePython)
  Dunit = g/cm3
  Dvalue = 5.86
  Group = -> [La_element002,O_element052,S_element015]
  conduct = 2
  density = 1
  expand = 3
  formula = G4_LANTHANUM_OXYSULFIDE
  name = G4_LANTHANUM_OXYSULFIDE
  specific = 4
FEATURE [App::DocumentObjectGroupPython] O_element053  label="O_element : 0.072"  # scripted group (container) (typed FeaturePython)
  n = 0.071682
FEATURE [App::DocumentObjectGroupPython] Pb_element002  label="Pb_element : 0.928"  # scripted group (container) (typed FeaturePython)
  n = 0.928318
FEATURE [App::DocumentObjectGroupPython] G4_LEAD_OXIDE  # scripted group (container) (typed FeaturePython)
  Dunit = g/cm3
  Dvalue = 9.53
  Group = -> [O_element053,Pb_element002]
  conduct = 2
  density = 1
  expand = 3
  formula = G4_LEAD_OXIDE
  name = G4_LEAD_OXIDE
  specific = 4
FEATURE [App::DocumentObjectGroupPython] Li_element001  label="Li_element : 1"  # scripted group (container) (typed FeaturePython)
  n = 1
  ref = Li_element
FEATURE [App::DocumentObjectGroupPython] N_element022  label="N_element : 011"  # scripted group (container) (typed FeaturePython)
  n = 1
  ref = N_element
FEATURE [App::DocumentObjectGroupPython] H_element049  label="H_element : 026"  # scripted group (container) (typed FeaturePython)
  n = 2
  ref = H_element
FEATURE [App::DocumentObjectGroupPython] G4_LITHIUM_AMIDE  # scripted group (container) (typed FeaturePython)
  Dunit = g/cm3
  Dvalue = 1.178
  Group = -> [Li_element001,N_element022,H_element049]
  conduct = 2
  density = 1
  expand = 3
  formula = G4_LITHIUM_AMIDE
  name = G4_LITHIUM_AMIDE
  specific = 4
FEATURE [App::DocumentObjectGroupPython] Li_element002  label="Li_element : 2"  # scripted group (container) (typed FeaturePython)
  n = 2
  ref = Li_element
FEATURE [App::DocumentObjectGroupPython] C_element055  label="C_element : 030"  # scripted group (container) (typed FeaturePython)
  n = 1
  ref = C_element
FEATURE [App::DocumentObjectGroupPython] O_element054  label="O_element : 028"  # scripted group (container) (typed FeaturePython)
  n = 3
  ref = O_element
FEATURE [App::DocumentObjectGroupPython] G4_LITHIUM_CARBONATE  # scripted group (container) (typed FeaturePython)
  Dunit = g/cm3
  Dvalue = 2.11
  Group = -> [Li_element002,C_element055,O_element054]
  conduct = 2
  density = 1
  expand = 3
  formula = G4_LITHIUM_CARBONATE
  name = G4_LITHIUM_CARBONATE
  specific = 4
FEATURE [App::DocumentObjectGroupPython] Li_element003  label="Li_element : 003"  # scripted group (container) (typed FeaturePython)
  n = 1
  ref = Li_element
FEATURE [App::DocumentObjectGroupPython] F_element012  label="F_element : 004"  # scripted group (container) (typed FeaturePython)
  n = 1
  ref = F_element
FEATURE [App::DocumentObjectGroupPython] G4_LITHIUM_FLUORIDE  # scripted group (container) (typed FeaturePython)
  Dunit = g/cm3
  Dvalue = 2.635
  Group = -> [Li_element003,F_element012]
  conduct = 2
  density = 1
  expand = 3
  formula = G4_LITHIUM_FLUORIDE
  name = G4_LITHIUM_FLUORIDE
  specific = 4
FEATURE [App::DocumentObjectGroupPython] Li_element004  label="Li_element : 004"  # scripted group (container) (typed FeaturePython)
  n = 1
  ref = Li_element
FEATURE [App::DocumentObjectGroupPython] H_element050  label="H_element : 027"  # scripted group (container) (typed FeaturePython)
  n = 1
  ref = H_element
FEATURE [App::DocumentObjectGroupPython] G4_LITHIUM_HYDRIDE  # scripted group (container) (typed FeaturePython)
  Dunit = g/cm3
  Dvalue = 0.82
  Group = -> [Li_element004,H_element050]
  conduct = 2
  density = 1
  expand = 3
  formula = G4_LITHIUM_HYDRIDE
  name = G4_LITHIUM_HYDRIDE
  specific = 4
FEATURE [App::DocumentObjectGroupPython] Li_element005  label="Li_element : 005"  # scripted group (container) (typed FeaturePython)
  n = 1
  ref = Li_element
FEATURE [App::DocumentObjectGroupPython] I_element003  label="I_element : 002"  # scripted group (container) (typed FeaturePython)
  n = 1
  ref = I_element
FEATURE [App::DocumentObjectGroupPython] G4_LITHIUM_IODIDE  # scripted group (container) (typed FeaturePython)
  Dunit = g/cm3
  Dvalue = 3.494
  Group = -> [Li_element005,I_element003]
  conduct = 2
  density = 1
  expand = 3
  formula = G4_LITHIUM_IODIDE
  name = G4_LITHIUM_IODIDE
  specific = 4
FEATURE [App::DocumentObjectGroupPython] Li_element006  label="Li_element : 006"  # scripted group (container) (typed FeaturePython)
  n = 2
  ref = Li_element
FEATURE [App::DocumentObjectGroupPython] O_element055  label="O_element : 029"  # scripted group (container) (typed FeaturePython)
  n = 1
  ref = O_element
FEATURE [App::DocumentObjectGroupPython] G4_LITHIUM_OXIDE  # scripted group (container) (typed FeaturePython)
  Dunit = g/cm3
  Dvalue = 2.013
  Group = -> [Li_element006,O_element055]
  conduct = 2
  density = 1
  expand = 3
  formula = G4_LITHIUM_OXIDE
  name = G4_LITHIUM_OXIDE
  specific = 4
FEATURE [App::DocumentObjectGroupPython] Li_element007  label="Li_element : 007"  # scripted group (container) (typed FeaturePython)
  n = 2
  ref = Li_element
FEATURE [App::DocumentObjectGroupPython] B_element005  label="B_element : 005"  # scripted group (container) (typed FeaturePython)
  n = 4
  ref = B_element
FEATURE [App::DocumentObjectGroupPython] O_element056  label="O_element : 7"  # scripted group (container) (typed FeaturePython)
  n = 7
  ref = O_element
FEATURE [App::DocumentObjectGroupPython] G4_LITHIUM_TETRABORATE  # scripted group (container) (typed FeaturePython)
  Dunit = g/cm3
  Dvalue = 2.44
  Group = -> [Li_element007,B_element005,O_element056]
  conduct = 2
  density = 1
  expand = 3
  formula = G4_LITHIUM_TETRABORATE
  name = G4_LITHIUM_TETRABORATE
  specific = 4
FEATURE [App::DocumentObjectGroupPython] H_element051  label="H_element : 0.105"  # scripted group (container) (typed FeaturePython)
  n = 0.105
FEATURE [App::DocumentObjectGroupPython] C_element056  label="C_element : 0.083"  # scripted group (container) (typed FeaturePython)
  n = 0.083
FEATURE [App::DocumentObjectGroupPython] N_element023  label="N_element : 0.023"  # scripted group (container) (typed FeaturePython)
  n = 0.023
FEATURE [App::DocumentObjectGroupPython] O_element057  label="O_element : 0.779"  # scripted group (container) (typed FeaturePython)
  n = 0.779
FEATURE [App::DocumentObjectGroupPython] Na_element010  label="Na_element : 0.097"  # scripted group (container) (typed FeaturePython)
  n = 0.002
FEATURE [App::DocumentObjectGroupPython] P_element006  label="P_element : 0.105"  # scripted group (container) (typed FeaturePython)
  n = 0.001
FEATURE [App::DocumentObjectGroupPython] S_element016  label="S_element : 0.017"  # scripted group (container) (typed FeaturePython)
  n = 0.002
FEATURE [App::DocumentObjectGroupPython] Cl_element014  label="Cl_element : 0.587"  # scripted group (container) (typed FeaturePython)
  n = 0.003
FEATURE [App::DocumentObjectGroupPython] K_element005  label="K_element : 0.015"  # scripted group (container) (typed FeaturePython)
  n = 0.002
FEATURE [App::DocumentObjectGroupPython] G4_LUNG_ICRP  # scripted group (container) (typed FeaturePython)
  Dunit = g/cm3
  Dvalue = 1.04
  Group = -> [H_element051,C_element056,N_element023,O_element057,Na_element010,P_element006,S_element016,Cl_element014,K_element005]
  conduct = 2
  density = 1
  expand = 3
  formula = G4_LUNG_ICRP
  name = G4_LUNG_ICRP
  specific = 4
FEATURE [App::DocumentObjectGroupPython] H_element052  label="H_element : 0.116"  # scripted group (container) (typed FeaturePython)
  n = 0.114318
FEATURE [App::DocumentObjectGroupPython] C_element057  label="C_element : 0.656"  # scripted group (container) (typed FeaturePython)
  n = 0.655824
FEATURE [App::DocumentObjectGroupPython] O_element058  label="O_element : 0.092"  # scripted group (container) (typed FeaturePython)
  n = 0.0921831
FEATURE [App::DocumentObjectGroupPython] Mg_element004  label="Mg_element : 0.135"  # scripted group (container) (typed FeaturePython)
  n = 0.134792
FEATURE [App::DocumentObjectGroupPython] Ca_element013  label="Ca_element : 0.003"  # scripted group (container) (typed FeaturePython)
  n = 0.002883
FEATURE [App::DocumentObjectGroupPython] G4_M3_WAX  # scripted group (container) (typed FeaturePython)
  Dunit = g/cm3
  Dvalue = 1.05
  Group = -> [H_element052,C_element057,O_element058,Mg_element004,Ca_element013]
  conduct = 2
  density = 1
  expand = 3
  formula = G4_M3_WAX
  name = G4_M3_WAX
  specific = 4
FEATURE [App::DocumentObjectGroupPython] Mg_element005  label="Mg_element : 1"  # scripted group (container) (typed FeaturePython)
  n = 1
  ref = Mg_element
FEATURE [App::DocumentObjectGroupPython] C_element058  label="C_element : 031"  # scripted group (container) (typed FeaturePython)
  n = 1
  ref = C_element
FEATURE [App::DocumentObjectGroupPython] O_element059  label="O_element : 030"  # scripted group (container) (typed FeaturePython)
  n = 3
  ref = O_element
FEATURE [App::DocumentObjectGroupPython] G4_MAGNESIUM_CARBONATE  # scripted group (container) (typed FeaturePython)
  Dunit = g/cm3
  Dvalue = 2.958
  Group = -> [Mg_element005,C_element058,O_element059]
  conduct = 2
  density = 1
  expand = 3
  formula = G4_MAGNESIUM_CARBONATE
  name = G4_MAGNESIUM_CARBONATE
  specific = 4
FEATURE [App::DocumentObjectGroupPython] Mg_element006  label="Mg_element : 002"  # scripted group (container) (typed FeaturePython)
  n = 1
  ref = Mg_element
FEATURE [App::DocumentObjectGroupPython] F_element013  label="F_element : 005"  # scripted group (container) (typed FeaturePython)
  n = 2
  ref = F_element
FEATURE [App::DocumentObjectGroupPython] G4_MAGNESIUM_FLUORIDE  # scripted group (container) (typed FeaturePython)
  Dunit = g/cm3
  Dvalue = 3
  Group = -> [Mg_element006,F_element013]
  conduct = 2
  density = 1
  expand = 3
  formula = G4_MAGNESIUM_FLUORIDE
  name = G4_MAGNESIUM_FLUORIDE
  specific = 4
FEATURE [App::DocumentObjectGroupPython] Mg_element007  label="Mg_element : 003"  # scripted group (container) (typed FeaturePython)
  n = 1
  ref = Mg_element
FEATURE [App::DocumentObjectGroupPython] O_element060  label="O_element : 031"  # scripted group (container) (typed FeaturePython)
  n = 1
  ref = O_element
FEATURE [App::DocumentObjectGroupPython] G4_MAGNESIUM_OXIDE  # scripted group (container) (typed FeaturePython)
  Dunit = g/cm3
  Dvalue = 3.58
  Group = -> [Mg_element007,O_element060]
  conduct = 2
  density = 1
  expand = 3
  formula = G4_MAGNESIUM_OXIDE
  name = G4_MAGNESIUM_OXIDE
  specific = 4
FEATURE [App::DocumentObjectGroupPython] Mg_element008  label="Mg_element : 004"  # scripted group (container) (typed FeaturePython)
  n = 1
  ref = Mg_element
FEATURE [App::DocumentObjectGroupPython] B_element006  label="B_element : 006"  # scripted group (container) (typed FeaturePython)
  n = 4
  ref = B_element
FEATURE [App::DocumentObjectGroupPython] O_element061  label="O_element : 032"  # scripted group (container) (typed FeaturePython)
  n = 7
  ref = O_element
FEATURE [App::DocumentObjectGroupPython] G4_MAGNESIUM_TETRABORATE  # scripted group (container) (typed FeaturePython)
  Dunit = g/cm3
  Dvalue = 2.53
  Group = -> [Mg_element008,B_element006,O_element061]
  conduct = 2
  density = 1
  expand = 3
  formula = G4_MAGNESIUM_TETRABORATE
  name = G4_MAGNESIUM_TETRABORATE
  specific = 4
FEATURE [App::DocumentObjectGroupPython] Hg_element001  label="Hg_element : 1"  # scripted group (container) (typed FeaturePython)
  n = 1
  ref = Hg_element
FEATURE [App::DocumentObjectGroupPython] I_element004  label="I_element : 2"  # scripted group (container) (typed FeaturePython)
  n = 2
  ref = I_element
FEATURE [App::DocumentObjectGroupPython] G4_MERCURIC_IODIDE  # scripted group (container) (typed FeaturePython)
  Dunit = g/cm3
  Dvalue = 6.36
  Group = -> [Hg_element001,I_element004]
  conduct = 2
  density = 1
  expand = 3
  formula = G4_MERCURIC_IODIDE
  name = G4_MERCURIC_IODIDE
  specific = 4
FEATURE [App::DocumentObjectGroupPython] C_element059  label="C_element : 032"  # scripted group (container) (typed FeaturePython)
  n = 1
  ref = C_element
FEATURE [App::DocumentObjectGroupPython] H_element053  label="H_element : 028"  # scripted group (container) (typed FeaturePython)
  n = 4
  ref = H_element
FEATURE [App::DocumentObjectGroupPython] G4_METHANE  # scripted group (container) (typed FeaturePython)
  Dunit = g/cm3
  Dvalue = 0.000667151
  Group = -> [C_element059,H_element053]
  conduct = 2
  density = 1
  expand = 3
  formula = G4_METHANE
  name = G4_METHANE
  specific = 4
FEATURE [App::DocumentObjectGroupPython] C_element060  label="C_element : 033"  # scripted group (container) (typed FeaturePython)
  n = 1
  ref = C_element
FEATURE [App::DocumentObjectGroupPython] H_element054  label="H_element : 029"  # scripted group (container) (typed FeaturePython)
  n = 4
  ref = H_element
FEATURE [App::DocumentObjectGroupPython] O_element062  label="O_element : 033"  # scripted group (container) (typed FeaturePython)
  n = 1
  ref = O_element
FEATURE [App::DocumentObjectGroupPython] G4_METHANOL  # scripted group (container) (typed FeaturePython)
  Dunit = g/cm3
  Dvalue = 0.7914
  Group = -> [C_element060,H_element054,O_element062]
  conduct = 2
  density = 1
  expand = 3
  formula = G4_METHANOL
  name = G4_METHANOL
  specific = 4
FEATURE [App::DocumentObjectGroupPython] H_element055  label="H_element : 0.134"  # scripted group (container) (typed FeaturePython)
  n = 0.13404
FEATURE [App::DocumentObjectGroupPython] C_element061  label="C_element : 0.778"  # scripted group (container) (typed FeaturePython)
  n = 0.77796
FEATURE [App::DocumentObjectGroupPython] O_element063  label="O_element : 0.035"  # scripted group (container) (typed FeaturePython)
  n = 0.03502
FEATURE [App::DocumentObjectGroupPython] Mg_element009  label="Mg_element : 0.039"  # scripted group (container) (typed FeaturePython)
  n = 0.038594
FEATURE [App::DocumentObjectGroupPython] Ti_element002  label="Ti_element : 0.014"  # scripted group (container) (typed FeaturePython)
  n = 0.014386
FEATURE [App::DocumentObjectGroupPython] G4_MIX_D_WAX  # scripted group (container) (typed FeaturePython)
  Dunit = g/cm3
  Dvalue = 0.99
  Group = -> [H_element055,C_element061,O_element063,Mg_element009,Ti_element002]
  conduct = 2
  density = 1
  expand = 3
  formula = G4_MIX_D_WAX
  name = G4_MIX_D_WAX
  specific = 4
FEATURE [App::DocumentObjectGroupPython] H_element056  label="H_element : 0.135"  # scripted group (container) (typed FeaturePython)
  n = 0.081192
FEATURE [App::DocumentObjectGroupPython] C_element062  label="C_element : 0.583"  # scripted group (container) (typed FeaturePython)
  n = 0.583442
FEATURE [App::DocumentObjectGroupPython] N_element024  label="N_element : 0.018"  # scripted group (container) (typed FeaturePython)
  n = 0.017798
FEATURE [App::DocumentObjectGroupPython] O_element064  label="O_element : 0.186"  # scripted group (container) (typed FeaturePython)
  n = 0.186381
FEATURE [App::DocumentObjectGroupPython] Mg_element010  label="Mg_element : 0.130"  # scripted group (container) (typed FeaturePython)
  n = 0.130287
FEATURE [App::DocumentObjectGroupPython] Cl_element015  label="Cl_element : 0.588"  # scripted group (container) (typed FeaturePython)
  n = 0.0009
FEATURE [App::DocumentObjectGroupPython] G4_MS20_TISSUE  # scripted group (container) (typed FeaturePython)
  Dunit = g/cm3
  Dvalue = 1
  Group = -> [H_element056,C_element062,N_element024,O_element064,Mg_element010,Cl_element015]
  conduct = 2
  density = 1
  expand = 3
  formula = G4_MS20_TISSUE
  name = G4_MS20_TISSUE
  specific = 4
FEATURE [App::DocumentObjectGroupPython] H_element057  label="H_element : 0.136"  # scripted group (container) (typed FeaturePython)
  n = 0.102
FEATURE [App::DocumentObjectGroupPython] C_element063  label="C_element : 0.143"  # scripted group (container) (typed FeaturePython)
  n = 0.143
FEATURE [App::DocumentObjectGroupPython] N_element025  label="N_element : 0.034"  # scripted group (container) (typed FeaturePython)
  n = 0.034
FEATURE [App::DocumentObjectGroupPython] O_element065  label="O_element : 0.710"  # scripted group (container) (typed FeaturePython)
  n = 0.71
FEATURE [App::DocumentObjectGroupPython] Na_element011  label="Na_element : 0.098"  # scripted group (container) (typed FeaturePython)
  n = 0.001
FEATURE [App::DocumentObjectGroupPython] P_element007  label="P_element : 0.002"  # scripted group (container) (typed FeaturePython)
  n = 0.002
FEATURE [App::DocumentObjectGroupPython] S_element017  label="S_element : 0.018"  # scripted group (container) (typed FeaturePython)
  n = 0.003
FEATURE [App::DocumentObjectGroupPython] Cl_element016  label="Cl_element : 0.589"  # scripted group (container) (typed FeaturePython)
  n = 0.001
FEATURE [App::DocumentObjectGroupPython] K_element006  label="K_element : 0.004"  # scripted group (container) (typed FeaturePython)
  n = 0.004
FEATURE [App::DocumentObjectGroupPython] G4_MUSCLE_SKELETAL_ICRP  # scripted group (container) (typed FeaturePython)
  Dunit = g/cm3
  Dvalue = 1.05
  Group = -> [H_element057,C_element063,N_element025,O_element065,Na_element011,P_element007,S_element017,Cl_element016,K_element006]
  conduct = 2
  density = 1
  expand = 3
  formula = G4_MUSCLE_SKELETAL_ICRP
  name = G4_MUSCLE_SKELETAL_ICRP
  specific = 4
FEATURE [App::DocumentObjectGroupPython] H_element058  label="H_element : 0.137"  # scripted group (container) (typed FeaturePython)
  n = 0.102102
FEATURE [App::DocumentObjectGroupPython] C_element064  label="C_element : 0.123"  # scripted group (container) (typed FeaturePython)
  n = 0.123123
FEATURE [App::DocumentObjectGroupPython] N_element026  label="N_element : 0.756"  # scripted group (container) (typed FeaturePython)
  n = 0.035035
FEATURE [App::DocumentObjectGroupPython] O_element066  label="O_element : 0.730"  # scripted group (container) (typed FeaturePython)
  n = 0.72973
FEATURE [App::DocumentObjectGroupPython] Na_element012  label="Na_element : 0.099"  # scripted group (container) (typed FeaturePython)
  n = 0.001001
FEATURE [App::DocumentObjectGroupPython] P_element008  label="P_element : 0.106"  # scripted group (container) (typed FeaturePython)
  n = 0.002002
FEATURE [App::DocumentObjectGroupPython] S_element018  label="S_element : 0.019"  # scripted group (container) (typed FeaturePython)
  n = 0.004004
FEATURE [App::DocumentObjectGroupPython] K_element007  label="K_element : 0.016"  # scripted group (container) (typed FeaturePython)
  n = 0.003003
FEATURE [App::DocumentObjectGroupPython] G4_MUSCLE_STRIATED_ICRU  # scripted group (container) (typed FeaturePython)
  Dunit = g/cm3
  Dvalue = 1.04
  Group = -> [H_element058,C_element064,N_element026,O_element066,Na_element012,P_element008,S_element018,K_element007]
  conduct = 2
  density = 1
  expand = 3
  formula = G4_MUSCLE_STRIATED_ICRU
  name = G4_MUSCLE_STRIATED_ICRU
  specific = 4
FEATURE [App::DocumentObjectGroupPython] H_element059  label="H_element : 0.098"  # scripted group (container) (typed FeaturePython)
  n = 0.0982341
FEATURE [App::DocumentObjectGroupPython] C_element065  label="C_element : 0.156"  # scripted group (container) (typed FeaturePython)
  n = 0.156214
FEATURE [App::DocumentObjectGroupPython] N_element027  label="N_element : 0.757"  # scripted group (container) (typed FeaturePython)
  n = 0.035451
FEATURE [App::DocumentObjectGroupPython] O_element067  label="O_element : 0.880"  # scripted group (container) (typed FeaturePython)
  n = 0.710101
FEATURE [App::DocumentObjectGroupPython] G4_MUSCLE_WITH_SUCROSE  # scripted group (container) (typed FeaturePython)
  Dunit = g/cm3
  Dvalue = 1.11
  Group = -> [H_element059,C_element065,N_element027,O_element067]
  conduct = 2
  density = 1
  expand = 3
  formula = G4_MUSCLE_WITH_SUCROSE
  name = G4_MUSCLE_WITH_SUCROSE
  specific = 4
FEATURE [App::DocumentObjectGroupPython] H_element060  label="H_element : 0.138"  # scripted group (container) (typed FeaturePython)
  n = 0.101969
FEATURE [App::DocumentObjectGroupPython] C_element066  label="C_element : 0.120"  # scripted group (container) (typed FeaturePython)
  n = 0.120058
FEATURE [App::DocumentObjectGroupPython] N_element028  label="N_element : 0.758"  # scripted group (container) (typed FeaturePython)
  n = 0.035451
FEATURE [App::DocumentObjectGroupPython] O_element068  label="O_element : 0.743"  # scripted group (container) (typed FeaturePython)
  n = 0.742522
FEATURE [App::DocumentObjectGroupPython] G4_MUSCLE_WITHOUT_SUCROSE  # scripted group (container) (typed FeaturePython)
  Dunit = g/cm3
  Dvalue = 1.07
  Group = -> [H_element060,C_element066,N_element028,O_element068]
  conduct = 2
  density = 1
  expand = 3
  formula = G4_MUSCLE_WITHOUT_SUCROSE
  name = G4_MUSCLE_WITHOUT_SUCROSE
  specific = 4
FEATURE [App::DocumentObjectGroupPython] C_element067  label="C_element : 10"  # scripted group (container) (typed FeaturePython)
  n = 10
  ref = C_element
FEATURE [App::DocumentObjectGroupPython] H_element061  label="H_element : 030"  # scripted group (container) (typed FeaturePython)
  n = 8
  ref = H_element
FEATURE [App::DocumentObjectGroupPython] G4_NAPHTHALENE  # scripted group (container) (typed FeaturePython)
  Dunit = g/cm3
  Dvalue = 1.145
  Group = -> [C_element067,H_element061]
  conduct = 2
  density = 1
  expand = 3
  formula = G4_NAPHTHALENE
  name = G4_NAPHTHALENE
  specific = 4
FEATURE [App::DocumentObjectGroupPython] C_element068  label="C_element : 034"  # scripted group (container) (typed FeaturePython)
  n = 6
  ref = C_element
FEATURE [App::DocumentObjectGroupPython] H_element062  label="H_element : 031"  # scripted group (container) (typed FeaturePython)
  n = 5
  ref = H_element
FEATURE [App::DocumentObjectGroupPython] N_element029  label="N_element : 012"  # scripted group (container) (typed FeaturePython)
  n = 1
  ref = N_element
FEATURE [App::DocumentObjectGroupPython] O_element069  label="O_element : 034"  # scripted group (container) (typed FeaturePython)
  n = 2
  ref = O_element
FEATURE [App::DocumentObjectGroupPython] G4_NITROBENZENE  # scripted group (container) (typed FeaturePython)
  Dunit = g/cm3
  Dvalue = 1.19867
  Group = -> [C_element068,H_element062,N_element029,O_element069]
  conduct = 2
  density = 1
  expand = 3
  formula = G4_NITROBENZENE
  name = G4_NITROBENZENE
  specific = 4
FEATURE [App::DocumentObjectGroupPython] N_element030  label="N_element : 013"  # scripted group (container) (typed FeaturePython)
  n = 2
  ref = N_element
FEATURE [App::DocumentObjectGroupPython] O_element070  label="O_element : 035"  # scripted group (container) (typed FeaturePython)
  n = 1
  ref = O_element
FEATURE [App::DocumentObjectGroupPython] G4_NITROUS_OXIDE  # scripted group (container) (typed FeaturePython)
  Dunit = g/cm3
  Dvalue = 0.00183094
  Group = -> [N_element030,O_element070]
  conduct = 2
  density = 1
  expand = 3
  formula = G4_NITROUS_OXIDE
  name = G4_NITROUS_OXIDE
  specific = 4
FEATURE [App::DocumentObjectGroupPython] H_element063  label="H_element : 0.104"  # scripted group (container) (typed FeaturePython)
  n = 0.103509
FEATURE [App::DocumentObjectGroupPython] C_element069  label="C_element : 0.648"  # scripted group (container) (typed FeaturePython)
  n = 0.648416
FEATURE [App::DocumentObjectGroupPython] N_element031  label="N_element : 0.100"  # scripted group (container) (typed FeaturePython)
  n = 0.0995361
FEATURE [App::DocumentObjectGroupPython] O_element071  label="O_element : 0.149"  # scripted group (container) (typed FeaturePython)
  n = 0.148539
FEATURE [App::DocumentObjectGroupPython] G4_NYLON_8062  label="G4_NYLON-8062"  # scripted group (container) (typed FeaturePython)
  Dunit = g/cm3
  Dvalue = 1.08
  Group = -> [H_element063,C_element069,N_element031,O_element071]
  conduct = 2
  density = 1
  expand = 3
  formula = G4_NYLON-8062
  name = G4_NYLON-8062
  specific = 4
FEATURE [App::DocumentObjectGroupPython] C_element070  label="C_element : 035"  # scripted group (container) (typed FeaturePython)
  n = 6
  ref = C_element
FEATURE [App::DocumentObjectGroupPython] H_element064  label="H_element : 11"  # scripted group (container) (typed FeaturePython)
  n = 11
  ref = H_element
FEATURE [App::DocumentObjectGroupPython] N_element032  label="N_element : 014"  # scripted group (container) (typed FeaturePython)
  n = 1
  ref = N_element
FEATURE [App::DocumentObjectGroupPython] O_element072  label="O_element : 036"  # scripted group (container) (typed FeaturePython)
  n = 1
  ref = O_element
FEATURE [App::DocumentObjectGroupPython] G4_NYLON_6_6  label="G4_NYLON-6-6"  # scripted group (container) (typed FeaturePython)
  Dunit = g/cm3
  Dvalue = 1.14
  Group = -> [C_element070,H_element064,N_element032,O_element072]
  conduct = 2
  density = 1
  expand = 3
  formula = G4_NYLON-6-6
  name = G4_NYLON-6-6
  specific = 4
FEATURE [App::DocumentObjectGroupPython] H_element065  label="H_element : 0.139"  # scripted group (container) (typed FeaturePython)
  n = 0.107062
FEATURE [App::DocumentObjectGroupPython] C_element071  label="C_element : 0.680"  # scripted group (container) (typed FeaturePython)
  n = 0.680449
FEATURE [App::DocumentObjectGroupPython] N_element033  label="N_element : 0.099"  # scripted group (container) (typed FeaturePython)
  n = 0.099189
FEATURE [App::DocumentObjectGroupPython] O_element073  label="O_element : 0.113"  # scripted group (container) (typed FeaturePython)
  n = 0.1133
FEATURE [App::DocumentObjectGroupPython] G4_NYLON_6_10  label="G4_NYLON-6-10"  # scripted group (container) (typed FeaturePython)
  Dunit = g/cm3
  Dvalue = 1.14
  Group = -> [H_element065,C_element071,N_element033,O_element073]
  conduct = 2
  density = 1
  expand = 3
  formula = G4_NYLON-6-10
  name = G4_NYLON-6-10
  specific = 4
FEATURE [App::DocumentObjectGroupPython] H_element066  label="H_element : 0.140"  # scripted group (container) (typed FeaturePython)
  n = 0.115476
FEATURE [App::DocumentObjectGroupPython] C_element072  label="C_element : 0.721"  # scripted group (container) (typed FeaturePython)
  n = 0.720818
FEATURE [App::DocumentObjectGroupPython] N_element034  label="N_element : 0.076"  # scripted group (container) (typed FeaturePython)
  n = 0.0764169
FEATURE [App::DocumentObjectGroupPython] O_element074  label="O_element : 0.087"  # scripted group (container) (typed FeaturePython)
  n = 0.0872889
FEATURE [App::DocumentObjectGroupPython] G4_NYLON_11_RILSAN  label="G4_NYLON-11_RILSAN"  # scripted group (container) (typed FeaturePython)
  Dunit = g/cm3
  Dvalue = 1.425
  Group = -> [H_element066,C_element072,N_element034,O_element074]
  conduct = 2
  density = 1
  expand = 3
  formula = G4_NYLON-11_RILSAN
  name = G4_NYLON-11_RILSAN
  specific = 4
FEATURE [App::DocumentObjectGroupPython] C_element073  label="C_element : 8"  # scripted group (container) (typed FeaturePython)
  n = 8
  ref = C_element
FEATURE [App::DocumentObjectGroupPython] H_element067  label="H_element : 18"  # scripted group (container) (typed FeaturePython)
  n = 18
  ref = H_element
FEATURE [App::DocumentObjectGroupPython] G4_OCTANE  # scripted group (container) (typed FeaturePython)
  Dunit = g/cm3
  Dvalue = 0.7026
  Group = -> [C_element073,H_element067]
  conduct = 2
  density = 1
  expand = 3
  formula = G4_OCTANE
  name = G4_OCTANE
  specific = 4
FEATURE [App::DocumentObjectGroupPython] C_element074  label="C_element : 25"  # scripted group (container) (typed FeaturePython)
  n = 25
  ref = C_element
FEATURE [App::DocumentObjectGroupPython] H_element068  label="H_element : 52"  # scripted group (container) (typed FeaturePython)
  n = 52
  ref = H_element
FEATURE [App::DocumentObjectGroupPython] G4_PARAFFIN  # scripted group (container) (typed FeaturePython)
  Dunit = g/cm3
  Dvalue = 0.93
  Group = -> [C_element074,H_element068]
  conduct = 2
  density = 1
  expand = 3
  formula = G4_PARAFFIN
  name = G4_PARAFFIN
  specific = 4
FEATURE [App::DocumentObjectGroupPython] C_element075  label="C_element : 036"  # scripted group (container) (typed FeaturePython)
  n = 5
  ref = C_element
FEATURE [App::DocumentObjectGroupPython] H_element069  label="H_element : 032"  # scripted group (container) (typed FeaturePython)
  n = 12
  ref = H_element
FEATURE [App::DocumentObjectGroupPython] G4_N_PENTANE  label="G4_N-PENTANE"  # scripted group (container) (typed FeaturePython)
  Dunit = g/cm3
  Dvalue = 0.6262
  Group = -> [C_element075,H_element069]
  conduct = 2
  density = 1
  expand = 3
  formula = G4_N-PENTANE
  name = G4_N-PENTANE
  specific = 4
FEATURE [App::DocumentObjectGroupPython] H_element070  label="H_element : 0.014"  # scripted group (container) (typed FeaturePython)
  n = 0.0141
FEATURE [App::DocumentObjectGroupPython] C_element076  label="C_element : 0.072"  # scripted group (container) (typed FeaturePython)
  n = 0.072261
FEATURE [App::DocumentObjectGroupPython] N_element035  label="N_element : 0.019"  # scripted group (container) (typed FeaturePython)
  n = 0.01932
FEATURE [App::DocumentObjectGroupPython] O_element075  label="O_element : 0.066"  # scripted group (container) (typed FeaturePython)
  n = 0.066101
FEATURE [App::DocumentObjectGroupPython] S_element019  label="S_element : 0.020"  # scripted group (container) (typed FeaturePython)
  n = 0.00189
FEATURE [App::DocumentObjectGroupPython] Br_element004  label="Br_element : 0.349"  # scripted group (container) (typed FeaturePython)
  n = 0.349103
FEATURE [App::DocumentObjectGroupPython] Ag_element001  label="Ag_element : 0.474"  # scripted group (container) (typed FeaturePython)
  n = 0.474105
FEATURE [App::DocumentObjectGroupPython] I_element005  label="I_element : 0.003"  # scripted group (container) (typed FeaturePython)
  n = 0.00312
FEATURE [App::DocumentObjectGroupPython] G4_PHOTO_EMULSION  # scripted group (container) (typed FeaturePython)
  Dunit = g/cm3
  Dvalue = 3.815
  Group = -> [H_element070,C_element076,N_element035,O_element075,S_element019,Br_element004,Ag_element001,I_element005]
  conduct = 2
  density = 1
  expand = 3
  formula = G4_PHOTO_EMULSION
  name = G4_PHOTO_EMULSION
  specific = 4
FEATURE [App::DocumentObjectGroupPython] C_element077  label="C_element : 9"  # scripted group (container) (typed FeaturePython)
  n = 9
  ref = C_element
FEATURE [App::DocumentObjectGroupPython] H_element071  label="H_element : 033"  # scripted group (container) (typed FeaturePython)
  n = 10
  ref = H_element
FEATURE [App::DocumentObjectGroupPython] G4_PLASTIC_SC_VINYLTOLUENE  # scripted group (container) (typed FeaturePython)
  Dunit = g/cm3
  Dvalue = 1.032
  Group = -> [C_element077,H_element071]
  conduct = 2
  density = 1
  expand = 3
  formula = G4_PLASTIC_SC_VINYLTOLUENE
  name = G4_PLASTIC_SC_VINYLTOLUENE
  specific = 4
FEATURE [App::DocumentObjectGroupPython] Pu_element001  label="Pu_element : 1"  # scripted group (container) (typed FeaturePython)
  n = 1
  ref = Pu_element
FEATURE [App::DocumentObjectGroupPython] O_element076  label="O_element : 037"  # scripted group (container) (typed FeaturePython)
  n = 2
  ref = O_element
FEATURE [App::DocumentObjectGroupPython] G4_PLUTONIUM_DIOXIDE  # scripted group (container) (typed FeaturePython)
  Dunit = g/cm3
  Dvalue = 11.46
  Group = -> [Pu_element001,O_element076]
  conduct = 2
  density = 1
  expand = 3
  formula = G4_PLUTONIUM_DIOXIDE
  name = G4_PLUTONIUM_DIOXIDE
  specific = 4
FEATURE [App::DocumentObjectGroupPython] C_element078  label="C_element : 037"  # scripted group (container) (typed FeaturePython)
  n = 3
  ref = C_element
FEATURE [App::DocumentObjectGroupPython] H_element072  label="H_element : 034"  # scripted group (container) (typed FeaturePython)
  n = 3
  ref = H_element
FEATURE [App::DocumentObjectGroupPython] N_element036  label="N_element : 015"  # scripted group (container) (typed FeaturePython)
  n = 1
  ref = N_element
FEATURE [App::DocumentObjectGroupPython] G4_POLYACRYLONITRILE  # scripted group (container) (typed FeaturePython)
  Dunit = g/cm3
  Dvalue = 1.17
  Group = -> [C_element078,H_element072,N_element036]
  conduct = 2
  density = 1
  expand = 3
  formula = G4_POLYACRYLONITRILE
  name = G4_POLYACRYLONITRILE
  specific = 4
FEATURE [App::DocumentObjectGroupPython] C_element079  label="C_element : 16"  # scripted group (container) (typed FeaturePython)
  n = 16
  ref = C_element
FEATURE [App::DocumentObjectGroupPython] H_element073  label="H_element : 035"  # scripted group (container) (typed FeaturePython)
  n = 14
  ref = H_element
FEATURE [App::DocumentObjectGroupPython] O_element077  label="O_element : 038"  # scripted group (container) (typed FeaturePython)
  n = 3
  ref = O_element
FEATURE [App::DocumentObjectGroupPython] G4_POLYCARBONATE  # scripted group (container) (typed FeaturePython)
  Dunit = g/cm3
  Dvalue = 1.2
  Group = -> [C_element079,H_element073,O_element077]
  conduct = 2
  density = 1
  expand = 3
  formula = G4_POLYCARBONATE
  name = G4_POLYCARBONATE
  specific = 4
FEATURE [App::DocumentObjectGroupPython] C_element080  label="C_element : 038"  # scripted group (container) (typed FeaturePython)
  n = 8
  ref = C_element
FEATURE [App::DocumentObjectGroupPython] H_element074  label="H_element : 036"  # scripted group (container) (typed FeaturePython)
  n = 7
  ref = H_element
FEATURE [App::DocumentObjectGroupPython] Cl_element017  label="Cl_element : 007"  # scripted group (container) (typed FeaturePython)
  n = 1
  ref = Cl_element
FEATURE [App::DocumentObjectGroupPython] G4_POLYCHLOROSTYRENE  # scripted group (container) (typed FeaturePython)
  Dunit = g/cm3
  Dvalue = 1.3
  Group = -> [C_element080,H_element074,Cl_element017]
  conduct = 2
  density = 1
  expand = 3
  formula = G4_POLYCHLOROSTYRENE
  name = G4_POLYCHLOROSTYRENE
  specific = 4
FEATURE [App::DocumentObjectGroupPython] C_element081  label="C_element : 039"  # scripted group (container) (typed FeaturePython)
  n = 1
  ref = C_element
FEATURE [App::DocumentObjectGroupPython] H_element075  label="H_element : 037"  # scripted group (container) (typed FeaturePython)
  n = 2
  ref = H_element
FEATURE [App::DocumentObjectGroupPython] G4_POLYETHYLENE  # scripted group (container) (typed FeaturePython)
  Dunit = g/cm3
  Dvalue = 0.94
  Group = -> [C_element081,H_element075]
  conduct = 2
  density = 1
  expand = 3
  formula = G4_POLYETHYLENE
  name = G4_POLYETHYLENE
  specific = 4
FEATURE [App::DocumentObjectGroupPython] C_element082  label="C_element : 040"  # scripted group (container) (typed FeaturePython)
  n = 10
  ref = C_element
FEATURE [App::DocumentObjectGroupPython] H_element076  label="H_element : 038"  # scripted group (container) (typed FeaturePython)
  n = 8
  ref = H_element
FEATURE [App::DocumentObjectGroupPython] O_element078  label="O_element : 039"  # scripted group (container) (typed FeaturePython)
  n = 4
  ref = O_element
FEATURE [App::DocumentObjectGroupPython] G4_MYLAR  # scripted group (container) (typed FeaturePython)
  Dunit = g/cm3
  Dvalue = 1.4
  Group = -> [C_element082,H_element076,O_element078]
  conduct = 2
  density = 1
  expand = 3
  formula = G4_MYLAR
  name = G4_MYLAR
  specific = 4
FEATURE [App::DocumentObjectGroupPython] C_element083  label="C_element : 041"  # scripted group (container) (typed FeaturePython)
  n = 5
  ref = C_element
FEATURE [App::DocumentObjectGroupPython] H_element077  label="H_element : 039"  # scripted group (container) (typed FeaturePython)
  n = 8
  ref = H_element
FEATURE [App::DocumentObjectGroupPython] O_element079  label="O_element : 040"  # scripted group (container) (typed FeaturePython)
  n = 2
  ref = O_element
FEATURE [App::DocumentObjectGroupPython] G4_PLEXIGLASS  # scripted group (container) (typed FeaturePython)
  Dunit = g/cm3
  Dvalue = 1.19
  Group = -> [C_element083,H_element077,O_element079]
  conduct = 2
  density = 1
  expand = 3
  formula = G4_PLEXIGLASS
  name = G4_PLEXIGLASS
  specific = 4
FEATURE [App::DocumentObjectGroupPython] C_element084  label="C_element : 042"  # scripted group (container) (typed FeaturePython)
  n = 1
  ref = C_element
FEATURE [App::DocumentObjectGroupPython] H_element078  label="H_element : 040"  # scripted group (container) (typed FeaturePython)
  n = 2
  ref = H_element
FEATURE [App::DocumentObjectGroupPython] O_element080  label="O_element : 041"  # scripted group (container) (typed FeaturePython)
  n = 1
  ref = O_element
FEATURE [App::DocumentObjectGroupPython] G4_POLYOXYMETHYLENE  # scripted group (container) (typed FeaturePython)
  Dunit = g/cm3
  Dvalue = 1.425
  Group = -> [C_element084,H_element078,O_element080]
  conduct = 2
  density = 1
  expand = 3
  formula = G4_POLYOXYMETHYLENE
  name = G4_POLYOXYMETHYLENE
  specific = 4
FEATURE [App::DocumentObjectGroupPython] C_element085  label="C_element : 043"  # scripted group (container) (typed FeaturePython)
  n = 2
  ref = C_element
FEATURE [App::DocumentObjectGroupPython] H_element079  label="H_element : 041"  # scripted group (container) (typed FeaturePython)
  n = 4
  ref = H_element
FEATURE [App::DocumentObjectGroupPython] G4_POLYPROPYLENE  # scripted group (container) (typed FeaturePython)
  Dunit = g/cm3
  Dvalue = 0.9
  Group = -> [C_element085,H_element079]
  conduct = 2
  density = 1
  expand = 3
  formula = G4_POLYPROPYLENE
  name = G4_POLYPROPYLENE
  specific = 4
FEATURE [App::DocumentObjectGroupPython] C_element086  label="C_element : 044"  # scripted group (container) (typed FeaturePython)
  n = 8
  ref = C_element
FEATURE [App::DocumentObjectGroupPython] H_element080  label="H_element : 042"  # scripted group (container) (typed FeaturePython)
  n = 8
  ref = H_element
FEATURE [App::DocumentObjectGroupPython] G4_POLYSTYRENE  # scripted group (container) (typed FeaturePython)
  Dunit = g/cm3
  Dvalue = 1.06
  Group = -> [C_element086,H_element080]
  conduct = 2
  density = 1
  expand = 3
  formula = G4_POLYSTYRENE
  name = G4_POLYSTYRENE
  specific = 4
FEATURE [App::DocumentObjectGroupPython] C_element087  label="C_element : 045"  # scripted group (container) (typed FeaturePython)
  n = 2
  ref = C_element
FEATURE [App::DocumentObjectGroupPython] F_element014  label="F_element : 4"  # scripted group (container) (typed FeaturePython)
  n = 4
  ref = F_element
FEATURE [App::DocumentObjectGroupPython] G4_TEFLON  # scripted group (container) (typed FeaturePython)
  Dunit = g/cm3
  Dvalue = 2.2
  Group = -> [C_element087,F_element014]
  conduct = 2
  density = 1
  expand = 3
  formula = G4_TEFLON
  name = G4_TEFLON
  specific = 4
FEATURE [App::DocumentObjectGroupPython] C_element088  label="C_element : 046"  # scripted group (container) (typed FeaturePython)
  n = 2
  ref = C_element
FEATURE [App::DocumentObjectGroupPython] F_element015  label="F_element : 006"  # scripted group (container) (typed FeaturePython)
  n = 3
  ref = F_element
FEATURE [App::DocumentObjectGroupPython] Cl_element018  label="Cl_element : 008"  # scripted group (container) (typed FeaturePython)
  n = 1
  ref = Cl_element
FEATURE [App::DocumentObjectGroupPython] G4_POLYTRIFLUOROCHLOROETHYLENE  # scripted group (container) (typed FeaturePython)
  Dunit = g/cm3
  Dvalue = 2.1
  Group = -> [C_element088,F_element015,Cl_element018]
  conduct = 2
  density = 1
  expand = 3
  formula = G4_POLYTRIFLUOROCHLOROETHYLENE
  name = G4_POLYTRIFLUOROCHLOROETHYLENE
  specific = 4
FEATURE [App::DocumentObjectGroupPython] C_element089  label="C_element : 047"  # scripted group (container) (typed FeaturePython)
  n = 4
  ref = C_element
FEATURE [App::DocumentObjectGroupPython] H_element081  label="H_element : 043"  # scripted group (container) (typed FeaturePython)
  n = 6
  ref = H_element
FEATURE [App::DocumentObjectGroupPython] O_element081  label="O_element : 042"  # scripted group (container) (typed FeaturePython)
  n = 2
  ref = O_element
FEATURE [App::DocumentObjectGroupPython] G4_POLYVINYL_ACETATE  # scripted group (container) (typed FeaturePython)
  Dunit = g/cm3
  Dvalue = 1.19
  Group = -> [C_element089,H_element081,O_element081]
  conduct = 2
  density = 1
  expand = 3
  formula = G4_POLYVINYL_ACETATE
  name = G4_POLYVINYL_ACETATE
  specific = 4
FEATURE [App::DocumentObjectGroupPython] C_element090  label="C_element : 048"  # scripted group (container) (typed FeaturePython)
  n = 2
  ref = C_element
FEATURE [App::DocumentObjectGroupPython] H_element082  label="H_element : 044"  # scripted group (container) (typed FeaturePython)
  n = 4
  ref = H_element
FEATURE [App::DocumentObjectGroupPython] O_element082  label="O_element : 043"  # scripted group (container) (typed FeaturePython)
  n = 1
  ref = O_element
FEATURE [App::DocumentObjectGroupPython] G4_POLYVINYL_ALCOHOL  # scripted group (container) (typed FeaturePython)
  Dunit = g/cm3
  Dvalue = 1.3
  Group = -> [C_element090,H_element082,O_element082]
  conduct = 2
  density = 1
  expand = 3
  formula = G4_POLYVINYL_ALCOHOL
  name = G4_POLYVINYL_ALCOHOL
  specific = 4
FEATURE [App::DocumentObjectGroupPython] C_element091  label="C_element : 049"  # scripted group (container) (typed FeaturePython)
  n = 8
  ref = C_element
FEATURE [App::DocumentObjectGroupPython] H_element083  label="H_element : 045"  # scripted group (container) (typed FeaturePython)
  n = 14
  ref = H_element
FEATURE [App::DocumentObjectGroupPython] O_element083  label="O_element : 044"  # scripted group (container) (typed FeaturePython)
  n = 2
  ref = O_element
FEATURE [App::DocumentObjectGroupPython] G4_POLYVINYL_BUTYRAL  # scripted group (container) (typed FeaturePython)
  Dunit = g/cm3
  Dvalue = 1.12
  Group = -> [C_element091,H_element083,O_element083]
  conduct = 2
  density = 1
  expand = 3
  formula = G4_POLYVINYL_BUTYRAL
  name = G4_POLYVINYL_BUTYRAL
  specific = 4
FEATURE [App::DocumentObjectGroupPython] C_element092  label="C_element : 050"  # scripted group (container) (typed FeaturePython)
  n = 2
  ref = C_element
FEATURE [App::DocumentObjectGroupPython] H_element084  label="H_element : 046"  # scripted group (container) (typed FeaturePython)
  n = 3
  ref = H_element
FEATURE [App::DocumentObjectGroupPython] Cl_element019  label="Cl_element : 009"  # scripted group (container) (typed FeaturePython)
  n = 1
  ref = Cl_element
FEATURE [App::DocumentObjectGroupPython] G4_POLYVINYL_CHLORIDE  # scripted group (container) (typed FeaturePython)
  Dunit = g/cm3
  Dvalue = 1.3
  Group = -> [C_element092,H_element084,Cl_element019]
  conduct = 2
  density = 1
  expand = 3
  formula = G4_POLYVINYL_CHLORIDE
  name = G4_POLYVINYL_CHLORIDE
  specific = 4
FEATURE [App::DocumentObjectGroupPython] C_element093  label="C_element : 051"  # scripted group (container) (typed FeaturePython)
  n = 2
  ref = C_element
FEATURE [App::DocumentObjectGroupPython] H_element085  label="H_element : 047"  # scripted group (container) (typed FeaturePython)
  n = 2
  ref = H_element
FEATURE [App::DocumentObjectGroupPython] Cl_element020  label="Cl_element : 010"  # scripted group (container) (typed FeaturePython)
  n = 2
  ref = Cl_element
FEATURE [App::DocumentObjectGroupPython] G4_POLYVINYLIDENE_CHLORIDE  # scripted group (container) (typed FeaturePython)
  Dunit = g/cm3
  Dvalue = 1.7
  Group = -> [C_element093,H_element085,Cl_element020]
  conduct = 2
  density = 1
  expand = 3
  formula = G4_POLYVINYLIDENE_CHLORIDE
  name = G4_POLYVINYLIDENE_CHLORIDE
  specific = 4
FEATURE [App::DocumentObjectGroupPython] C_element094  label="C_element : 052"  # scripted group (container) (typed FeaturePython)
  n = 2
  ref = C_element
FEATURE [App::DocumentObjectGroupPython] H_element086  label="H_element : 048"  # scripted group (container) (typed FeaturePython)
  n = 2
  ref = H_element
FEATURE [App::DocumentObjectGroupPython] F_element016  label="F_element : 007"  # scripted group (container) (typed FeaturePython)
  n = 2
  ref = F_element
FEATURE [App::DocumentObjectGroupPython] G4_POLYVINYLIDENE_FLUORIDE  # scripted group (container) (typed FeaturePython)
  Dunit = g/cm3
  Dvalue = 1.76
  Group = -> [C_element094,H_element086,F_element016]
  conduct = 2
  density = 1
  expand = 3
  formula = G4_POLYVINYLIDENE_FLUORIDE
  name = G4_POLYVINYLIDENE_FLUORIDE
  specific = 4
FEATURE [App::DocumentObjectGroupPython] C_element095  label="C_element : 053"  # scripted group (container) (typed FeaturePython)
  n = 6
  ref = C_element
FEATURE [App::DocumentObjectGroupPython] H_element087  label="H_element : 9"  # scripted group (container) (typed FeaturePython)
  n = 9
  ref = H_element
FEATURE [App::DocumentObjectGroupPython] N_element037  label="N_element : 016"  # scripted group (container) (typed FeaturePython)
  n = 1
  ref = N_element
FEATURE [App::DocumentObjectGroupPython] O_element084  label="O_element : 045"  # scripted group (container) (typed FeaturePython)
  n = 1
  ref = O_element
FEATURE [App::DocumentObjectGroupPython] G4_POLYVINYL_PYRROLIDONE  # scripted group (container) (typed FeaturePython)
  Dunit = g/cm3
  Dvalue = 1.25
  Group = -> [C_element095,H_element087,N_element037,O_element084]
  conduct = 2
  density = 1
  expand = 3
  formula = G4_POLYVINYL_PYRROLIDONE
  name = G4_POLYVINYL_PYRROLIDONE
  specific = 4
FEATURE [App::DocumentObjectGroupPython] K_element008  label="K_element : 1"  # scripted group (container) (typed FeaturePython)
  n = 1
  ref = K_element
FEATURE [App::DocumentObjectGroupPython] I_element006  label="I_element : 003"  # scripted group (container) (typed FeaturePython)
  n = 1
  ref = I_element
FEATURE [App::DocumentObjectGroupPython] G4_POTASSIUM_IODIDE  # scripted group (container) (typed FeaturePython)
  Dunit = g/cm3
  Dvalue = 3.13
  Group = -> [K_element008,I_element006]
  conduct = 2
  density = 1
  expand = 3
  formula = G4_POTASSIUM_IODIDE
  name = G4_POTASSIUM_IODIDE
  specific = 4
FEATURE [App::DocumentObjectGroupPython] K_element009  label="K_element : 2"  # scripted group (container) (typed FeaturePython)
  n = 2
  ref = K_element
FEATURE [App::DocumentObjectGroupPython] O_element085  label="O_element : 046"  # scripted group (container) (typed FeaturePython)
  n = 1
  ref = O_element
FEATURE [App::DocumentObjectGroupPython] G4_POTASSIUM_OXIDE  # scripted group (container) (typed FeaturePython)
  Dunit = g/cm3
  Dvalue = 2.32
  Group = -> [K_element009,O_element085]
  conduct = 2
  density = 1
  expand = 3
  formula = G4_POTASSIUM_OXIDE
  name = G4_POTASSIUM_OXIDE
  specific = 4
FEATURE [App::DocumentObjectGroupPython] C_element096  label="C_element : 054"  # scripted group (container) (typed FeaturePython)
  n = 3
  ref = C_element
FEATURE [App::DocumentObjectGroupPython] H_element088  label="H_element : 049"  # scripted group (container) (typed FeaturePython)
  n = 8
  ref = H_element
FEATURE [App::DocumentObjectGroupPython] G4_PROPANE  # scripted group (container) (typed FeaturePython)
  Dunit = g/cm3
  Dvalue = 0.00187939
  Group = -> [C_element096,H_element088]
  conduct = 2
  density = 1
  expand = 3
  formula = G4_PROPANE
  name = G4_PROPANE
  specific = 4
FEATURE [App::DocumentObjectGroupPython] C_element097  label="C_element : 055"  # scripted group (container) (typed FeaturePython)
  n = 3
  ref = C_element
FEATURE [App::DocumentObjectGroupPython] H_element089  label="H_element : 050"  # scripted group (container) (typed FeaturePython)
  n = 8
  ref = H_element
FEATURE [App::DocumentObjectGroupPython] G4_lPROPANE  # scripted group (container) (typed FeaturePython)
  Dunit = g/cm3
  Dvalue = 0.43
  Group = -> [C_element097,H_element089]
  conduct = 2
  density = 1
  expand = 3
  formula = G4_lPROPANE
  name = G4_lPROPANE
  specific = 4
FEATURE [App::DocumentObjectGroupPython] C_element098  label="C_element : 056"  # scripted group (container) (typed FeaturePython)
  n = 3
  ref = C_element
FEATURE [App::DocumentObjectGroupPython] H_element090  label="H_element : 051"  # scripted group (container) (typed FeaturePython)
  n = 8
  ref = H_element
FEATURE [App::DocumentObjectGroupPython] O_element086  label="O_element : 047"  # scripted group (container) (typed FeaturePython)
  n = 1
  ref = O_element
FEATURE [App::DocumentObjectGroupPython] G4_N_PROPYL_ALCOHOL  label="G4_N-PROPYL_ALCOHOL"  # scripted group (container) (typed FeaturePython)
  Dunit = g/cm3
  Dvalue = 0.8035
  Group = -> [C_element098,H_element090,O_element086]
  conduct = 2
  density = 1
  expand = 3
  formula = G4_N-PROPYL_ALCOHOL
  name = G4_N-PROPYL_ALCOHOL
  specific = 4
FEATURE [App::DocumentObjectGroupPython] C_element099  label="C_element : 057"  # scripted group (container) (typed FeaturePython)
  n = 5
  ref = C_element
FEATURE [App::DocumentObjectGroupPython] H_element091  label="H_element : 052"  # scripted group (container) (typed FeaturePython)
  n = 5
  ref = H_element
FEATURE [App::DocumentObjectGroupPython] N_element038  label="N_element : 017"  # scripted group (container) (typed FeaturePython)
  n = 1
  ref = N_element
FEATURE [App::DocumentObjectGroupPython] G4_PYRIDINE  # scripted group (container) (typed FeaturePython)
  Dunit = g/cm3
  Dvalue = 0.9819
  Group = -> [C_element099,H_element091,N_element038]
  conduct = 2
  density = 1
  expand = 3
  formula = G4_PYRIDINE
  name = G4_PYRIDINE
  specific = 4
FEATURE [App::DocumentObjectGroupPython] H_element092  label="H_element : 0.144"  # scripted group (container) (typed FeaturePython)
  n = 0.143711
FEATURE [App::DocumentObjectGroupPython] C_element100  label="C_element : 0.856"  # scripted group (container) (typed FeaturePython)
  n = 0.856289
FEATURE [App::DocumentObjectGroupPython] G4_RUBBER_BUTYL  # scripted group (container) (typed FeaturePython)
  Dunit = g/cm3
  Dvalue = 0.92
  Group = -> [H_element092,C_element100]
  conduct = 2
  density = 1
  expand = 3
  formula = G4_RUBBER_BUTYL
  name = G4_RUBBER_BUTYL
  specific = 4
FEATURE [App::DocumentObjectGroupPython] H_element093  label="H_element : 0.118"  # scripted group (container) (typed FeaturePython)
  n = 0.118371
FEATURE [App::DocumentObjectGroupPython] C_element101  label="C_element : 0.882"  # scripted group (container) (typed FeaturePython)
  n = 0.881629
FEATURE [App::DocumentObjectGroupPython] G4_RUBBER_NATURAL  # scripted group (container) (typed FeaturePython)
  Dunit = g/cm3
  Dvalue = 0.92
  Group = -> [H_element093,C_element101]
  conduct = 2
  density = 1
  expand = 3
  formula = G4_RUBBER_NATURAL
  name = G4_RUBBER_NATURAL
  specific = 4
FEATURE [App::DocumentObjectGroupPython] H_element094  label="H_element : 0.145"  # scripted group (container) (typed FeaturePython)
  n = 0.05692
FEATURE [App::DocumentObjectGroupPython] C_element102  label="C_element : 0.543"  # scripted group (container) (typed FeaturePython)
  n = 0.542646
FEATURE [App::DocumentObjectGroupPython] Cl_element021  label="Cl_element : 0.400"  # scripted group (container) (typed FeaturePython)
  n = 0.400434
FEATURE [App::DocumentObjectGroupPython] G4_RUBBER_NEOPRENE  # scripted group (container) (typed FeaturePython)
  Dunit = g/cm3
  Dvalue = 1.23
  Group = -> [H_element094,C_element102,Cl_element021]
  conduct = 2
  density = 1
  expand = 3
  formula = G4_RUBBER_NEOPRENE
  name = G4_RUBBER_NEOPRENE
  specific = 4
FEATURE [App::DocumentObjectGroupPython] Si_element006  label="Si_element : 1"  # scripted group (container) (typed FeaturePython)
  n = 1
  ref = Si_element
FEATURE [App::DocumentObjectGroupPython] O_element087  label="O_element : 048"  # scripted group (container) (typed FeaturePython)
  n = 2
  ref = O_element
FEATURE [App::DocumentObjectGroupPython] G4_SILICON_DIOXIDE  # scripted group (container) (typed FeaturePython)
  Dunit = g/cm3
  Dvalue = 2.32
  Group = -> [Si_element006,O_element087]
  conduct = 2
  density = 1
  expand = 3
  formula = G4_SILICON_DIOXIDE
  name = G4_SILICON_DIOXIDE
  specific = 4
FEATURE [App::DocumentObjectGroupPython] Ag_element002  label="Ag_element : 1"  # scripted group (container) (typed FeaturePython)
  n = 1
  ref = Ag_element
FEATURE [App::DocumentObjectGroupPython] Br_element005  label="Br_element : 003"  # scripted group (container) (typed FeaturePython)
  n = 1
  ref = Br_element
FEATURE [App::DocumentObjectGroupPython] G4_SILVER_BROMIDE  # scripted group (container) (typed FeaturePython)
  Dunit = g/cm3
  Dvalue = 6.473
  Group = -> [Ag_element002,Br_element005]
  conduct = 2
  density = 1
  expand = 3
  formula = G4_SILVER_BROMIDE
  name = G4_SILVER_BROMIDE
  specific = 4
FEATURE [App::DocumentObjectGroupPython] Ag_element003  label="Ag_element : 002"  # scripted group (container) (typed FeaturePython)
  n = 1
  ref = Ag_element
FEATURE [App::DocumentObjectGroupPython] Cl_element022  label="Cl_element : 011"  # scripted group (container) (typed FeaturePython)
  n = 1
  ref = Cl_element
FEATURE [App::DocumentObjectGroupPython] G4_SILVER_CHLORIDE  # scripted group (container) (typed FeaturePython)
  Dunit = g/cm3
  Dvalue = 5.56
  Group = -> [Ag_element003,Cl_element022]
  conduct = 2
  density = 1
  expand = 3
  formula = G4_SILVER_CHLORIDE
  name = G4_SILVER_CHLORIDE
  specific = 4
FEATURE [App::DocumentObjectGroupPython] Br_element006  label="Br_element : 0.423"  # scripted group (container) (typed FeaturePython)
  n = 0.422895
FEATURE [App::DocumentObjectGroupPython] Ag_element004  label="Ag_element : 0.574"  # scripted group (container) (typed FeaturePython)
  n = 0.573748
FEATURE [App::DocumentObjectGroupPython] I_element007  label="I_element : 0.649"  # scripted group (container) (typed FeaturePython)
  n = 0.003357
FEATURE [App::DocumentObjectGroupPython] G4_SILVER_HALIDES  # scripted group (container) (typed FeaturePython)
  Dunit = g/cm3
  Dvalue = 6.47
  Group = -> [Br_element006,Ag_element004,I_element007]
  conduct = 2
  density = 1
  expand = 3
  formula = G4_SILVER_HALIDES
  name = G4_SILVER_HALIDES
  specific = 4
FEATURE [App::DocumentObjectGroupPython] Ag_element005  label="Ag_element : 003"  # scripted group (container) (typed FeaturePython)
  n = 1
  ref = Ag_element
FEATURE [App::DocumentObjectGroupPython] I_element008  label="I_element : 004"  # scripted group (container) (typed FeaturePython)
  n = 1
  ref = I_element
FEATURE [App::DocumentObjectGroupPython] G4_SILVER_IODIDE  # scripted group (container) (typed FeaturePython)
  Dunit = g/cm3
  Dvalue = 6.01
  Group = -> [Ag_element005,I_element008]
  conduct = 2
  density = 1
  expand = 3
  formula = G4_SILVER_IODIDE
  name = G4_SILVER_IODIDE
  specific = 4
FEATURE [App::DocumentObjectGroupPython] H_element095  label="H_element : 0.100"  # scripted group (container) (typed FeaturePython)
  n = 0.1
FEATURE [App::DocumentObjectGroupPython] C_element103  label="C_element : 0.204"  # scripted group (container) (typed FeaturePython)
  n = 0.204
FEATURE [App::DocumentObjectGroupPython] N_element039  label="N_element : 0.759"  # scripted group (container) (typed FeaturePython)
  n = 0.042
FEATURE [App::DocumentObjectGroupPython] O_element088  label="O_element : 0.645"  # scripted group (container) (typed FeaturePython)
  n = 0.645
FEATURE [App::DocumentObjectGroupPython] Na_element013  label="Na_element : 0.100"  # scripted group (container) (typed FeaturePython)
  n = 0.002
FEATURE [App::DocumentObjectGroupPython] P_element009  label="P_element : 0.107"  # scripted group (container) (typed FeaturePython)
  n = 0.001
FEATURE [App::DocumentObjectGroupPython] S_element020  label="S_element : 0.021"  # scripted group (container) (typed FeaturePython)
  n = 0.002
FEATURE [App::DocumentObjectGroupPython] Cl_element023  label="Cl_element : 0.590"  # scripted group (container) (typed FeaturePython)
  n = 0.003
FEATURE [App::DocumentObjectGroupPython] K_element010  label="K_element : 0.001"  # scripted group (container) (typed FeaturePython)
  n = 0.001
FEATURE [App::DocumentObjectGroupPython] G4_SKIN_ICRP  # scripted group (container) (typed FeaturePython)
  Dunit = g/cm3
  Dvalue = 1.09
  Group = -> [H_element095,C_element103,N_element039,O_element088,Na_element013,P_element009,S_element020,Cl_element023,K_element010]
  conduct = 2
  density = 1
  expand = 3
  formula = G4_SKIN_ICRP
  name = G4_SKIN_ICRP
  specific = 4
FEATURE [App::DocumentObjectGroupPython] Na_element014  label="Na_element : 2"  # scripted group (container) (typed FeaturePython)
  n = 2
  ref = Na_element
FEATURE [App::DocumentObjectGroupPython] C_element104  label="C_element : 058"  # scripted group (container) (typed FeaturePython)
  n = 1
  ref = C_element
FEATURE [App::DocumentObjectGroupPython] O_element089  label="O_element : 049"  # scripted group (container) (typed FeaturePython)
  n = 3
  ref = O_element
FEATURE [App::DocumentObjectGroupPython] G4_SODIUM_CARBONATE  # scripted group (container) (typed FeaturePython)
  Dunit = g/cm3
  Dvalue = 2.532
  Group = -> [Na_element014,C_element104,O_element089]
  conduct = 2
  density = 1
  expand = 3
  formula = G4_SODIUM_CARBONATE
  name = G4_SODIUM_CARBONATE
  specific = 4
FEATURE [App::DocumentObjectGroupPython] Na_element015  label="Na_element : 1"  # scripted group (container) (typed FeaturePython)
  n = 1
  ref = Na_element
FEATURE [App::DocumentObjectGroupPython] I_element009  label="I_element : 005"  # scripted group (container) (typed FeaturePython)
  n = 1
  ref = I_element
FEATURE [App::DocumentObjectGroupPython] G4_SODIUM_IODIDE  # scripted group (container) (typed FeaturePython)
  Dunit = g/cm3
  Dvalue = 3.667
  Group = -> [Na_element015,I_element009]
  conduct = 2
  density = 1
  expand = 3
  formula = G4_SODIUM_IODIDE
  name = G4_SODIUM_IODIDE
  specific = 4
FEATURE [App::DocumentObjectGroupPython] Na_element016  label="Na_element : 003"  # scripted group (container) (typed FeaturePython)
  n = 2
  ref = Na_element
FEATURE [App::DocumentObjectGroupPython] O_element090  label="O_element : 050"  # scripted group (container) (typed FeaturePython)
  n = 1
  ref = O_element
FEATURE [App::DocumentObjectGroupPython] G4_SODIUM_MONOXIDE  # scripted group (container) (typed FeaturePython)
  Dunit = g/cm3
  Dvalue = 2.27
  Group = -> [Na_element016,O_element090]
  conduct = 2
  density = 1
  expand = 3
  formula = G4_SODIUM_MONOXIDE
  name = G4_SODIUM_MONOXIDE
  specific = 4
FEATURE [App::DocumentObjectGroupPython] Na_element017  label="Na_element : 004"  # scripted group (container) (typed FeaturePython)
  n = 1
  ref = Na_element
FEATURE [App::DocumentObjectGroupPython] N_element040  label="N_element : 018"  # scripted group (container) (typed FeaturePython)
  n = 1
  ref = N_element
FEATURE [App::DocumentObjectGroupPython] O_element091  label="O_element : 051"  # scripted group (container) (typed FeaturePython)
  n = 3
  ref = O_element
FEATURE [App::DocumentObjectGroupPython] G4_SODIUM_NITRATE  # scripted group (container) (typed FeaturePython)
  Dunit = g/cm3
  Dvalue = 2.261
  Group = -> [Na_element017,N_element040,O_element091]
  conduct = 2
  density = 1
  expand = 3
  formula = G4_SODIUM_NITRATE
  name = G4_SODIUM_NITRATE
  specific = 4
FEATURE [App::DocumentObjectGroupPython] C_element105  label="C_element : 059"  # scripted group (container) (typed FeaturePython)
  n = 14
  ref = C_element
FEATURE [App::DocumentObjectGroupPython] H_element096  label="H_element : 053"  # scripted group (container) (typed FeaturePython)
  n = 12
  ref = H_element
FEATURE [App::DocumentObjectGroupPython] G4_STILBENE  # scripted group (container) (typed FeaturePython)
  Dunit = g/cm3
  Dvalue = 0.9707
  Group = -> [C_element105,H_element096]
  conduct = 2
  density = 1
  expand = 3
  formula = G4_STILBENE
  name = G4_STILBENE
  specific = 4
FEATURE [App::DocumentObjectGroupPython] C_element106  label="C_element : 12"  # scripted group (container) (typed FeaturePython)
  n = 12
  ref = C_element
FEATURE [App::DocumentObjectGroupPython] H_element097  label="H_element : 22"  # scripted group (container) (typed FeaturePython)
  n = 22
  ref = H_element
FEATURE [App::DocumentObjectGroupPython] O_element092  label="O_element : 11"  # scripted group (container) (typed FeaturePython)
  n = 11
  ref = O_element
FEATURE [App::DocumentObjectGroupPython] G4_SUCROSE  # scripted group (container) (typed FeaturePython)
  Dunit = g/cm3
  Dvalue = 1.5805
  Group = -> [C_element106,H_element097,O_element092]
  conduct = 2
  density = 1
  expand = 3
  formula = G4_SUCROSE
  name = G4_SUCROSE
  specific = 4
FEATURE [App::DocumentObjectGroupPython] C_element107  label="C_element : 18"  # scripted group (container) (typed FeaturePython)
  n = 18
  ref = C_element
FEATURE [App::DocumentObjectGroupPython] H_element098  label="H_element : 054"  # scripted group (container) (typed FeaturePython)
  n = 14
  ref = H_element
FEATURE [App::DocumentObjectGroupPython] G4_TERPHENYL  # scripted group (container) (typed FeaturePython)
  Dunit = g/cm3
  Dvalue = 1.24
  Group = -> [C_element107,H_element098]
  conduct = 2
  density = 1
  expand = 3
  formula = G4_TERPHENYL
  name = G4_TERPHENYL
  specific = 4
FEATURE [App::DocumentObjectGroupPython] H_element099  label="H_element : 0.146"  # scripted group (container) (typed FeaturePython)
  n = 0.106
FEATURE [App::DocumentObjectGroupPython] C_element108  label="C_element : 0.883"  # scripted group (container) (typed FeaturePython)
  n = 0.099
FEATURE [App::DocumentObjectGroupPython] N_element041  label="N_element : 0.020"  # scripted group (container) (typed FeaturePython)
  n = 0.02
FEATURE [App::DocumentObjectGroupPython] O_element093  label="O_element : 0.766"  # scripted group (container) (typed FeaturePython)
  n = 0.766
FEATURE [App::DocumentObjectGroupPython] Na_element018  label="Na_element : 0.101"  # scripted group (container) (typed FeaturePython)
  n = 0.002
FEATURE [App::DocumentObjectGroupPython] P_element010  label="P_element : 0.108"  # scripted group (container) (typed FeaturePython)
  n = 0.001
FEATURE [App::DocumentObjectGroupPython] S_element021  label="S_element : 0.022"  # scripted group (container) (typed FeaturePython)
  n = 0.002
FEATURE [App::DocumentObjectGroupPython] Cl_element024  label="Cl_element : 0.002"  # scripted group (container) (typed FeaturePython)
  n = 0.002
FEATURE [App::DocumentObjectGroupPython] K_element011  label="K_element : 0.017"  # scripted group (container) (typed FeaturePython)
  n = 0.002
FEATURE [App::DocumentObjectGroupPython] G4_TESTIS_ICRP  # scripted group (container) (typed FeaturePython)
  Dunit = g/cm3
  Dvalue = 1.04
  Group = -> [H_element099,C_element108,N_element041,O_element093,Na_element018,P_element010,S_element021,Cl_element024,K_element011]
  conduct = 2
  density = 1
  expand = 3
  formula = G4_TESTIS_ICRP
  name = G4_TESTIS_ICRP
  specific = 4
FEATURE [App::DocumentObjectGroupPython] C_element109  label="C_element : 060"  # scripted group (container) (typed FeaturePython)
  n = 2
  ref = C_element
FEATURE [App::DocumentObjectGroupPython] Cl_element025  label="Cl_element : 012"  # scripted group (container) (typed FeaturePython)
  n = 4
  ref = Cl_element
FEATURE [App::DocumentObjectGroupPython] G4_TETRACHLOROETHYLENE  # scripted group (container) (typed FeaturePython)
  Dunit = g/cm3
  Dvalue = 1.625
  Group = -> [C_element109,Cl_element025]
  conduct = 2
  density = 1
  expand = 3
  formula = G4_TETRACHLOROETHYLENE
  name = G4_TETRACHLOROETHYLENE
  specific = 4
FEATURE [App::DocumentObjectGroupPython] Tl_element001  label="Tl_element : 1"  # scripted group (container) (typed FeaturePython)
  n = 1
  ref = Tl_element
FEATURE [App::DocumentObjectGroupPython] Cl_element026  label="Cl_element : 013"  # scripted group (container) (typed FeaturePython)
  n = 1
  ref = Cl_element
FEATURE [App::DocumentObjectGroupPython] G4_THALLIUM_CHLORIDE  # scripted group (container) (typed FeaturePython)
  Dunit = g/cm3
  Dvalue = 7.004
  Group = -> [Tl_element001,Cl_element026]
  conduct = 2
  density = 1
  expand = 3
  formula = G4_THALLIUM_CHLORIDE
  name = G4_THALLIUM_CHLORIDE
  specific = 4
FEATURE [App::DocumentObjectGroupPython] H_element100  label="H_element : 0.147"  # scripted group (container) (typed FeaturePython)
  n = 0.105
FEATURE [App::DocumentObjectGroupPython] C_element110  label="C_element : 0.256"  # scripted group (container) (typed FeaturePython)
  n = 0.256
FEATURE [App::DocumentObjectGroupPython] N_element042  label="N_element : 0.760"  # scripted group (container) (typed FeaturePython)
  n = 0.027
FEATURE [App::DocumentObjectGroupPython] O_element094  label="O_element : 0.602"  # scripted group (container) (typed FeaturePython)
  n = 0.602
FEATURE [App::DocumentObjectGroupPython] Na_element019  label="Na_element : 0.102"  # scripted group (container) (typed FeaturePython)
  n = 0.001
FEATURE [App::DocumentObjectGroupPython] P_element011  label="P_element : 0.109"  # scripted group (container) (typed FeaturePython)
  n = 0.002
FEATURE [App::DocumentObjectGroupPython] S_element022  label="S_element : 0.023"  # scripted group (container) (typed FeaturePython)
  n = 0.003
FEATURE [App::DocumentObjectGroupPython] Cl_element027  label="Cl_element : 0.591"  # scripted group (container) (typed FeaturePython)
  n = 0.002
FEATURE [App::DocumentObjectGroupPython] K_element012  label="K_element : 0.018"  # scripted group (container) (typed FeaturePython)
  n = 0.002
FEATURE [App::DocumentObjectGroupPython] G4_TISSUE_SOFT_ICRP  # scripted group (container) (typed FeaturePython)
  Dunit = g/cm3
  Dvalue = 1.03
  Group = -> [H_element100,C_element110,N_element042,O_element094,Na_element019,P_element011,S_element022,Cl_element027,K_element012]
  conduct = 2
  density = 1
  expand = 3
  formula = G4_TISSUE_SOFT_ICRP
  name = G4_TISSUE_SOFT_ICRP
  specific = 4
FEATURE [App::DocumentObjectGroupPython] H_element101  label="H_element : 0.148"  # scripted group (container) (typed FeaturePython)
  n = 0.101
FEATURE [App::DocumentObjectGroupPython] C_element111  label="C_element : 0.111"  # scripted group (container) (typed FeaturePython)
  n = 0.111
FEATURE [App::DocumentObjectGroupPython] N_element043  label="N_element : 0.026"  # scripted group (container) (typed FeaturePython)
  n = 0.026
FEATURE [App::DocumentObjectGroupPython] O_element095  label="O_element : 0.762"  # scripted group (container) (typed FeaturePython)
  n = 0.762
FEATURE [App::DocumentObjectGroupPython] G4_TISSUE_SOFT_ICRU_4  label="G4_TISSUE_SOFT_ICRU-4"  # scripted group (container) (typed FeaturePython)
  Dunit = g/cm3
  Dvalue = 1
  Group = -> [H_element101,C_element111,N_element043,O_element095]
  conduct = 2
  density = 1
  expand = 3
  formula = G4_TISSUE_SOFT_ICRU-4
  name = G4_TISSUE_SOFT_ICRU-4
  specific = 4
FEATURE [App::DocumentObjectGroupPython] H_element102  label="H_element : 0.149"  # scripted group (container) (typed FeaturePython)
  n = 0.101869
FEATURE [App::DocumentObjectGroupPython] C_element112  label="C_element : 0.456"  # scripted group (container) (typed FeaturePython)
  n = 0.456179
FEATURE [App::DocumentObjectGroupPython] N_element044  label="N_element : 0.761"  # scripted group (container) (typed FeaturePython)
  n = 0.035172
FEATURE [App::DocumentObjectGroupPython] O_element096  label="O_element : 0.407"  # scripted group (container) (typed FeaturePython)
  n = 0.40678
FEATURE [App::DocumentObjectGroupPython] G4_TISSUE_METHANE  label="G4_TISSUE-METHANE"  # scripted group (container) (typed FeaturePython)
  Dunit = g/cm3
  Dvalue = 0.00106409
  Group = -> [H_element102,C_element112,N_element044,O_element096]
  conduct = 2
  density = 1
  expand = 3
  formula = G4_TISSUE-METHANE
  name = G4_TISSUE-METHANE
  specific = 4
FEATURE [App::DocumentObjectGroupPython] H_element103  label="H_element : 0.103"  # scripted group (container) (typed FeaturePython)
  n = 0.102672
FEATURE [App::DocumentObjectGroupPython] C_element113  label="C_element : 0.569"  # scripted group (container) (typed FeaturePython)
  n = 0.56894
FEATURE [App::DocumentObjectGroupPython] N_element045  label="N_element : 0.762"  # scripted group (container) (typed FeaturePython)
  n = 0.035022
FEATURE [App::DocumentObjectGroupPython] O_element097  label="O_element : 0.293"  # scripted group (container) (typed FeaturePython)
  n = 0.293366
FEATURE [App::DocumentObjectGroupPython] G4_TISSUE_PROPANE  label="G4_TISSUE-PROPANE"  # scripted group (container) (typed FeaturePython)
  Dunit = g/cm3
  Dvalue = 0.00182628
  Group = -> [H_element103,C_element113,N_element045,O_element097]
  conduct = 2
  density = 1
  expand = 3
  formula = G4_TISSUE-PROPANE
  name = G4_TISSUE-PROPANE
  specific = 4
FEATURE [App::DocumentObjectGroupPython] Ti_element003  label="Ti_element : 1"  # scripted group (container) (typed FeaturePython)
  n = 1
  ref = Ti_element
FEATURE [App::DocumentObjectGroupPython] O_element098  label="O_element : 052"  # scripted group (container) (typed FeaturePython)
  n = 2
  ref = O_element
FEATURE [App::DocumentObjectGroupPython] G4_TITANIUM_DIOXIDE  # scripted group (container) (typed FeaturePython)
  Dunit = g/cm3
  Dvalue = 4.26
  Group = -> [Ti_element003,O_element098]
  conduct = 2
  density = 1
  expand = 3
  formula = G4_TITANIUM_DIOXIDE
  name = G4_TITANIUM_DIOXIDE
  specific = 4
FEATURE [App::DocumentObjectGroupPython] C_element114  label="C_element : 061"  # scripted group (container) (typed FeaturePython)
  n = 7
  ref = C_element
FEATURE [App::DocumentObjectGroupPython] H_element104  label="H_element : 055"  # scripted group (container) (typed FeaturePython)
  n = 8
  ref = H_element
FEATURE [App::DocumentObjectGroupPython] G4_TOLUENE  # scripted group (container) (typed FeaturePython)
  Dunit = g/cm3
  Dvalue = 0.8669
  Group = -> [C_element114,H_element104]
  conduct = 2
  density = 1
  expand = 3
  formula = G4_TOLUENE
  name = G4_TOLUENE
  specific = 4
FEATURE [App::DocumentObjectGroupPython] C_element115  label="C_element : 062"  # scripted group (container) (typed FeaturePython)
  n = 2
  ref = C_element
FEATURE [App::DocumentObjectGroupPython] H_element105  label="H_element : 056"  # scripted group (container) (typed FeaturePython)
  n = 1
  ref = H_element
FEATURE [App::DocumentObjectGroupPython] Cl_element028  label="Cl_element : 014"  # scripted group (container) (typed FeaturePython)
  n = 3
  ref = Cl_element
FEATURE [App::DocumentObjectGroupPython] G4_TRICHLOROETHYLENE  # scripted group (container) (typed FeaturePython)
  Dunit = g/cm3
  Dvalue = 1.46
  Group = -> [C_element115,H_element105,Cl_element028]
  conduct = 2
  density = 1
  expand = 3
  formula = G4_TRICHLOROETHYLENE
  name = G4_TRICHLOROETHYLENE
  specific = 4
FEATURE [App::DocumentObjectGroupPython] C_element116  label="C_element : 063"  # scripted group (container) (typed FeaturePython)
  n = 6
  ref = C_element
FEATURE [App::DocumentObjectGroupPython] H_element106  label="H_element : 15"  # scripted group (container) (typed FeaturePython)
  n = 15
  ref = H_element
FEATURE [App::DocumentObjectGroupPython] O_element099  label="O_element : 053"  # scripted group (container) (typed FeaturePython)
  n = 4
  ref = O_element
FEATURE [App::DocumentObjectGroupPython] P_element012  label="P_element : 1"  # scripted group (container) (typed FeaturePython)
  n = 1
  ref = P_element
FEATURE [App::DocumentObjectGroupPython] G4_TRIETHYL_PHOSPHATE  # scripted group (container) (typed FeaturePython)
  Dunit = g/cm3
  Dvalue = 1.07
  Group = -> [C_element116,H_element106,O_element099,P_element012]
  conduct = 2
  density = 1
  expand = 3
  formula = G4_TRIETHYL_PHOSPHATE
  name = G4_TRIETHYL_PHOSPHATE
  specific = 4
FEATURE [App::DocumentObjectGroupPython] W_element003  label="W_element : 003"  # scripted group (container) (typed FeaturePython)
  n = 1
  ref = W_element
FEATURE [App::DocumentObjectGroupPython] F_element017  label="F_element : 6"  # scripted group (container) (typed FeaturePython)
  n = 6
  ref = F_element
FEATURE [App::DocumentObjectGroupPython] G4_TUNGSTEN_HEXAFLUORIDE  # scripted group (container) (typed FeaturePython)
  Dunit = g/cm3
  Dvalue = 2.4
  Group = -> [W_element003,F_element017]
  conduct = 2
  density = 1
  expand = 3
  formula = G4_TUNGSTEN_HEXAFLUORIDE
  name = G4_TUNGSTEN_HEXAFLUORIDE
  specific = 4
FEATURE [App::DocumentObjectGroupPython] U_element001  label="U_element : 1"  # scripted group (container) (typed FeaturePython)
  n = 1
  ref = U_element
FEATURE [App::DocumentObjectGroupPython] C_element117  label="C_element : 064"  # scripted group (container) (typed FeaturePython)
  n = 2
  ref = C_element
FEATURE [App::DocumentObjectGroupPython] G4_URANIUM_DICARBIDE  # scripted group (container) (typed FeaturePython)
  Dunit = g/cm3
  Dvalue = 11.28
  Group = -> [U_element001,C_element117]
  conduct = 2
  density = 1
  expand = 3
  formula = G4_URANIUM_DICARBIDE
  name = G4_URANIUM_DICARBIDE
  specific = 4
FEATURE [App::DocumentObjectGroupPython] U_element002  label="U_element : 002"  # scripted group (container) (typed FeaturePython)
  n = 1
  ref = U_element
FEATURE [App::DocumentObjectGroupPython] C_element118  label="C_element : 065"  # scripted group (container) (typed FeaturePython)
  n = 1
  ref = C_element
FEATURE [App::DocumentObjectGroupPython] G4_URANIUM_MONOCARBIDE  # scripted group (container) (typed FeaturePython)
  Dunit = g/cm3
  Dvalue = 13.63
  Group = -> [U_element002,C_element118]
  conduct = 2
  density = 1
  expand = 3
  formula = G4_URANIUM_MONOCARBIDE
  name = G4_URANIUM_MONOCARBIDE
  specific = 4
FEATURE [App::DocumentObjectGroupPython] U_element003  label="U_element : 003"  # scripted group (container) (typed FeaturePython)
  n = 1
  ref = U_element
FEATURE [App::DocumentObjectGroupPython] O_element100  label="O_element : 054"  # scripted group (container) (typed FeaturePython)
  n = 2
  ref = O_element
FEATURE [App::DocumentObjectGroupPython] G4_URANIUM_OXIDE  # scripted group (container) (typed FeaturePython)
  Dunit = g/cm3
  Dvalue = 10.96
  Group = -> [U_element003,O_element100]
  conduct = 2
  density = 1
  expand = 3
  formula = G4_URANIUM_OXIDE
  name = G4_URANIUM_OXIDE
  specific = 4
FEATURE [App::DocumentObjectGroupPython] C_element119  label="C_element : 066"  # scripted group (container) (typed FeaturePython)
  n = 1
  ref = C_element
FEATURE [App::DocumentObjectGroupPython] H_element107  label="H_element : 057"  # scripted group (container) (typed FeaturePython)
  n = 4
  ref = H_element
FEATURE [App::DocumentObjectGroupPython] N_element046  label="N_element : 019"  # scripted group (container) (typed FeaturePython)
  n = 2
  ref = N_element
FEATURE [App::DocumentObjectGroupPython] O_element101  label="O_element : 055"  # scripted group (container) (typed FeaturePython)
  n = 1
  ref = O_element
FEATURE [App::DocumentObjectGroupPython] G4_UREA  # scripted group (container) (typed FeaturePython)
  Dunit = g/cm3
  Dvalue = 1.323
  Group = -> [C_element119,H_element107,N_element046,O_element101]
  conduct = 2
  density = 1
  expand = 3
  formula = G4_UREA
  name = G4_UREA
  specific = 4
FEATURE [App::DocumentObjectGroupPython] C_element120  label="C_element : 067"  # scripted group (container) (typed FeaturePython)
  n = 5
  ref = C_element
FEATURE [App::DocumentObjectGroupPython] H_element108  label="H_element : 058"  # scripted group (container) (typed FeaturePython)
  n = 11
  ref = H_element
FEATURE [App::DocumentObjectGroupPython] N_element047  label="N_element : 020"  # scripted group (container) (typed FeaturePython)
  n = 1
  ref = N_element
FEATURE [App::DocumentObjectGroupPython] O_element102  label="O_element : 056"  # scripted group (container) (typed FeaturePython)
  n = 2
  ref = O_element
FEATURE [App::DocumentObjectGroupPython] G4_VALINE  # scripted group (container) (typed FeaturePython)
  Dunit = g/cm3
  Dvalue = 1.23
  Group = -> [C_element120,H_element108,N_element047,O_element102]
  conduct = 2
  density = 1
  expand = 3
  formula = G4_VALINE
  name = G4_VALINE
  specific = 4
FEATURE [App::DocumentObjectGroupPython] H_element109  label="H_element : 0.009"  # scripted group (container) (typed FeaturePython)
  n = 0.009417
FEATURE [App::DocumentObjectGroupPython] C_element121  label="C_element : 0.281"  # scripted group (container) (typed FeaturePython)
  n = 0.280555
FEATURE [App::DocumentObjectGroupPython] F_element018  label="F_element : 0.710"  # scripted group (container) (typed FeaturePython)
  n = 0.710028
FEATURE [App::DocumentObjectGroupPython] G4_VITON  # scripted group (container) (typed FeaturePython)
  Dunit = g/cm3
  Dvalue = 1.8
  Group = -> [H_element109,C_element121,F_element018]
  conduct = 2
  density = 1
  expand = 3
  formula = G4_VITON
  name = G4_VITON
  specific = 4
FEATURE [App::DocumentObjectGroupPython] H_element110  label="H_element : 059"  # scripted group (container) (typed FeaturePython)
  n = 2
  ref = H_element
FEATURE [App::DocumentObjectGroupPython] O_element103  label="O_element : 057"  # scripted group (container) (typed FeaturePython)
  n = 1
  ref = O_element
FEATURE [App::DocumentObjectGroupPython] G4_WATER  # scripted group (container) (typed FeaturePython)
  Dunit = g/cm3
  Dvalue = 1
  Group = -> [H_element110,O_element103]
  conduct = 2
  density = 1
  expand = 3
  formula = G4_WATER
  name = G4_WATER
  specific = 4
FEATURE [App::DocumentObjectGroupPython] H_element111  label="H_element : 060"  # scripted group (container) (typed FeaturePython)
  n = 2
  ref = H_element
FEATURE [App::DocumentObjectGroupPython] O_element104  label="O_element : 058"  # scripted group (container) (typed FeaturePython)
  n = 1
  ref = O_element
FEATURE [App::DocumentObjectGroupPython] G4_WATER_VAPOR  # scripted group (container) (typed FeaturePython)
  Dunit = g/cm3
  Dvalue = 0.000756182
  Group = -> [H_element111,O_element104]
  conduct = 2
  density = 1
  expand = 3
  formula = G4_WATER_VAPOR
  name = G4_WATER_VAPOR
  specific = 4
FEATURE [App::DocumentObjectGroupPython] C_element122  label="C_element : 068"  # scripted group (container) (typed FeaturePython)
  n = 8
  ref = C_element
FEATURE [App::DocumentObjectGroupPython] H_element112  label="H_element : 061"  # scripted group (container) (typed FeaturePython)
  n = 10
  ref = H_element
FEATURE [App::DocumentObjectGroupPython] G4_XYLENE  # scripted group (container) (typed FeaturePython)
  Dunit = g/cm3
  Dvalue = 0.87
  Group = -> [C_element122,H_element112]
  conduct = 2
  density = 1
  expand = 3
  formula = G4_XYLENE
  name = G4_XYLENE
  specific = 4
FEATURE [App::DocumentObjectGroupPython] C_element123  label="C_element : 069"  # scripted group (container) (typed FeaturePython)
  n = 1
  ref = C_element
FEATURE [App::DocumentObjectGroupPython] G4_GRAPHITE  # scripted group (container) (typed FeaturePython)
  Dunit = g/cm3
  Dvalue = 2.21
  Group = -> [C_element123]
  conduct = 2
  density = 1
  expand = 3
  formula = G4_GRAPHITE
  name = G4_GRAPHITE
  specific = 4
FEATURE [App::DocumentObjectGroupPython] NIST  # scripted group (container) (typed FeaturePython)
  Group = -> [G4_A_150_TISSUE,G4_ACETONE,G4_ACETYLENE,G4_ADENINE,G4_ADIPOSE_TISSUE_ICRP,G4_AIR,G4_ALANINE,G4_ALUMINUM_OXIDE,G4_AMBER,G4_AMMONIA,G4_ANILINE,G4_ANTHRACENE,G4_B_100_BONE,G4_BAKELITE,G4_BARIUM_FLUORIDE,G4_BARIUM_SULFATE,G4_BENZENE,G4_BERYLLIUM_OXIDE,G4_BGO,G4_BLOOD_ICRP,G4_BONE_COMPACT_ICRU,G4_BONE_CORTICAL_ICRP,G4_BORON_CARBIDE,G4_BORON_OXIDE,G4_BRAIN_ICRP,G4_BUTANE,G4_N_BUTYL_ALCOHOL,G4_C_552,+152 more]
FEATURE [App::DocumentObjectGroupPython] H_element113  label="H_element : 062"  # scripted group (container) (typed FeaturePython)
  n = 1
  ref = H_element
FEATURE [App::DocumentObjectGroupPython] G4_H  # scripted group (container) (typed FeaturePython)
  Dunit = g/cm3
  Dvalue = 8.3748e-05
  Group = -> [H_element113]
  conduct = 2
  density = 1
  expand = 3
  formula = H
  name = G4_H
  specific = 4
FEATURE [App::DocumentObjectGroupPython] He_element001  label="He_element : 1"  # scripted group (container) (typed FeaturePython)
  n = 1
  ref = He_element
FEATURE [App::DocumentObjectGroupPython] G4_He  # scripted group (container) (typed FeaturePython)
  Dunit = g/cm3
  Dvalue = 0.000166322
  Group = -> [He_element001]
  conduct = 2
  density = 1
  expand = 3
  formula = He
  name = G4_He
  specific = 4
FEATURE [App::DocumentObjectGroupPython] Li_element008  label="Li_element : 008"  # scripted group (container) (typed FeaturePython)
  n = 1
  ref = Li_element
FEATURE [App::DocumentObjectGroupPython] G4_Li  # scripted group (container) (typed FeaturePython)
  Dunit = g/cm3
  Dvalue = 0.534
  Group = -> [Li_element008]
  conduct = 2
  density = 1
  expand = 3
  formula = Li
  name = G4_Li
  specific = 4
FEATURE [App::DocumentObjectGroupPython] Be_element002  label="Be_element : 002"  # scripted group (container) (typed FeaturePython)
  n = 1
  ref = Be_element
FEATURE [App::DocumentObjectGroupPython] G4_Be  # scripted group (container) (typed FeaturePython)
  Dunit = g/cm3
  Dvalue = 1.848
  Group = -> [Be_element002]
  conduct = 2
  density = 1
  expand = 3
  formula = Be
  name = G4_Be
  specific = 4
FEATURE [App::DocumentObjectGroupPython] B_element007  label="B_element : 007"  # scripted group (container) (typed FeaturePython)
  n = 1
  ref = B_element
FEATURE [App::DocumentObjectGroupPython] G4_B  # scripted group (container) (typed FeaturePython)
  Dunit = g/cm3
  Dvalue = 2.37
  Group = -> [B_element007]
  conduct = 2
  density = 1
  expand = 3
  formula = B
  name = G4_B
  specific = 4
FEATURE [App::DocumentObjectGroupPython] C_element124  label="C_element : 070"  # scripted group (container) (typed FeaturePython)
  n = 1
  ref = C_element
FEATURE [App::DocumentObjectGroupPython] G4_C  # scripted group (container) (typed FeaturePython)
  Dunit = g/cm3
  Dvalue = 2
  Group = -> [C_element124]
  conduct = 2
  density = 1
  expand = 3
  formula = C
  name = G4_C
  specific = 4
FEATURE [App::DocumentObjectGroupPython] N_element048  label="N_element : 021"  # scripted group (container) (typed FeaturePython)
  n = 1
  ref = N_element
FEATURE [App::DocumentObjectGroupPython] G4_N  # scripted group (container) (typed FeaturePython)
  Dunit = g/cm3
  Dvalue = 0.0011652
  Group = -> [N_element048]
  conduct = 2
  density = 1
  expand = 3
  formula = N
  name = G4_N
  specific = 4
FEATURE [App::DocumentObjectGroupPython] O_element105  label="O_element : 059"  # scripted group (container) (typed FeaturePython)
  n = 1
  ref = O_element
FEATURE [App::DocumentObjectGroupPython] G4_O  # scripted group (container) (typed FeaturePython)
  Dunit = g/cm3
  Dvalue = 0.00133151
  Group = -> [O_element105]
  conduct = 2
  density = 1
  expand = 3
  formula = O
  name = G4_O
  specific = 4
FEATURE [App::DocumentObjectGroupPython] F_element019  label="F_element : 008"  # scripted group (container) (typed FeaturePython)
  n = 1
  ref = F_element
FEATURE [App::DocumentObjectGroupPython] G4_F  # scripted group (container) (typed FeaturePython)
  Dunit = g/cm3
  Dvalue = 0.00158029
  Group = -> [F_element019]
  conduct = 2
  density = 1
  expand = 3
  formula = F
  name = G4_F
  specific = 4
FEATURE [App::DocumentObjectGroupPython] Ne_element001  label="Ne_element : 1"  # scripted group (container) (typed FeaturePython)
  n = 1
  ref = Ne_element
FEATURE [App::DocumentObjectGroupPython] G4_Ne  # scripted group (container) (typed FeaturePython)
  Dunit = g/cm3
  Dvalue = 0.000838505
  Group = -> [Ne_element001]
  conduct = 2
  density = 1
  expand = 3
  formula = Ne
  name = G4_Ne
  specific = 4
FEATURE [App::DocumentObjectGroupPython] Na_element020  label="Na_element : 005"  # scripted group (container) (typed FeaturePython)
  n = 1
  ref = Na_element
FEATURE [App::DocumentObjectGroupPython] G4_Na  # scripted group (container) (typed FeaturePython)
  Dunit = g/cm3
  Dvalue = 0.971
  Group = -> [Na_element020]
  conduct = 2
  density = 1
  expand = 3
  formula = Na
  name = G4_Na
  specific = 4
FEATURE [App::DocumentObjectGroupPython] Mg_element011  label="Mg_element : 005"  # scripted group (container) (typed FeaturePython)
  n = 1
  ref = Mg_element
FEATURE [App::DocumentObjectGroupPython] G4_Mg  # scripted group (container) (typed FeaturePython)
  Dunit = g/cm3
  Dvalue = 1.74
  Group = -> [Mg_element011]
  conduct = 2
  density = 1
  expand = 3
  formula = Mg
  name = G4_Mg
  specific = 4
FEATURE [App::DocumentObjectGroupPython] Al_element004  label="Al_element : 1"  # scripted group (container) (typed FeaturePython)
  n = 1
  ref = Al_element
FEATURE [App::DocumentObjectGroupPython] G4_Al  # scripted group (container) (typed FeaturePython)
  Dunit = g/cm3
  Dvalue = 2.699
  Group = -> [Al_element004]
  conduct = 2
  density = 1
  expand = 3
  formula = Al
  name = G4_Al
  specific = 4
FEATURE [App::DocumentObjectGroupPython] Si_element007  label="Si_element : 002"  # scripted group (container) (typed FeaturePython)
  n = 1
  ref = Si_element
FEATURE [App::DocumentObjectGroupPython] G4_Si  # scripted group (container) (typed FeaturePython)
  Dunit = g/cm3
  Dvalue = 2.33
  Group = -> [Si_element007]
  conduct = 2
  density = 1
  expand = 3
  formula = Si
  name = G4_Si
  specific = 4
FEATURE [App::DocumentObjectGroupPython] P_element013  label="P_element : 002"  # scripted group (container) (typed FeaturePython)
  n = 1
  ref = P_element
FEATURE [App::DocumentObjectGroupPython] G4_P  # scripted group (container) (typed FeaturePython)
  Dunit = g/cm3
  Dvalue = 2.2
  Group = -> [P_element013]
  conduct = 2
  density = 1
  expand = 3
  formula = P
  name = G4_P
  specific = 4
FEATURE [App::DocumentObjectGroupPython] S_element023  label="S_element : 007"  # scripted group (container) (typed FeaturePython)
  n = 1
  ref = S_element
FEATURE [App::DocumentObjectGroupPython] G4_S  # scripted group (container) (typed FeaturePython)
  Dunit = g/cm3
  Dvalue = 2
  Group = -> [S_element023]
  conduct = 2
  density = 1
  expand = 3
  formula = S
  name = G4_S
  specific = 4
FEATURE [App::DocumentObjectGroupPython] Cl_element029  label="Cl_element : 015"  # scripted group (container) (typed FeaturePython)
  n = 1
  ref = Cl_element
FEATURE [App::DocumentObjectGroupPython] G4_Cl  # scripted group (container) (typed FeaturePython)
  Dunit = g/cm3
  Dvalue = 0.00299473
  Group = -> [Cl_element029]
  conduct = 2
  density = 1
  expand = 3
  formula = Cl
  name = G4_Cl
  specific = 4
FEATURE [App::DocumentObjectGroupPython] Ar_element002  label="Ar_element : 1"  # scripted group (container) (typed FeaturePython)
  n = 1
  ref = Ar_element
FEATURE [App::DocumentObjectGroupPython] G4_Ar  # scripted group (container) (typed FeaturePython)
  Dunit = g/cm3
  Dvalue = 0.00166201
  Group = -> [Ar_element002]
  conduct = 2
  density = 1
  expand = 3
  formula = Ar
  name = G4_Ar
  specific = 4
FEATURE [App::DocumentObjectGroupPython] K_element013  label="K_element : 003"  # scripted group (container) (typed FeaturePython)
  n = 1
  ref = K_element
FEATURE [App::DocumentObjectGroupPython] G4_K  # scripted group (container) (typed FeaturePython)
  Dunit = g/cm3
  Dvalue = 0.862
  Group = -> [K_element013]
  conduct = 2
  density = 1
  expand = 3
  formula = K
  name = G4_K
  specific = 4
FEATURE [App::DocumentObjectGroupPython] Ca_element014  label="Ca_element : 007"  # scripted group (container) (typed FeaturePython)
  n = 1
  ref = Ca_element
FEATURE [App::DocumentObjectGroupPython] G4_Ca  # scripted group (container) (typed FeaturePython)
  Dunit = g/cm3
  Dvalue = 1.55
  Group = -> [Ca_element014]
  conduct = 2
  density = 1
  expand = 3
  formula = Ca
  name = G4_Ca
  specific = 4
FEATURE [App::DocumentObjectGroupPython] Sc_element001  label="Sc_element : 1"  # scripted group (container) (typed FeaturePython)
  n = 1
  ref = Sc_element
FEATURE [App::DocumentObjectGroupPython] G4_Sc  # scripted group (container) (typed FeaturePython)
  Dunit = g/cm3
  Dvalue = 2.989
  Group = -> [Sc_element001]
  conduct = 2
  density = 1
  expand = 3
  formula = Sc
  name = G4_Sc
  specific = 4
FEATURE [App::DocumentObjectGroupPython] Ti_element004  label="Ti_element : 002"  # scripted group (container) (typed FeaturePython)
  n = 1
  ref = Ti_element
FEATURE [App::DocumentObjectGroupPython] G4_Ti  # scripted group (container) (typed FeaturePython)
  Dunit = g/cm3
  Dvalue = 4.54
  Group = -> [Ti_element004]
  conduct = 2
  density = 1
  expand = 3
  formula = Ti
  name = G4_Ti
  specific = 4
FEATURE [App::DocumentObjectGroupPython] V_element001  label="V_element : 1"  # scripted group (container) (typed FeaturePython)
  n = 1
  ref = V_element
FEATURE [App::DocumentObjectGroupPython] G4_V  # scripted group (container) (typed FeaturePython)
  Dunit = g/cm3
  Dvalue = 6.11
  Group = -> [V_element001]
  conduct = 2
  density = 1
  expand = 3
  formula = V
  name = G4_V
  specific = 4
FEATURE [App::DocumentObjectGroupPython] Cr_element001  label="Cr_element : 1"  # scripted group (container) (typed FeaturePython)
  n = 1
  ref = Cr_element
FEATURE [App::DocumentObjectGroupPython] G4_Cr  # scripted group (container) (typed FeaturePython)
  Dunit = g/cm3
  Dvalue = 7.18
  Group = -> [Cr_element001]
  conduct = 2
  density = 1
  expand = 3
  formula = Cr
  name = G4_Cr
  specific = 4
FEATURE [App::DocumentObjectGroupPython] Mn_element001  label="Mn_element : 1"  # scripted group (container) (typed FeaturePython)
  n = 1
  ref = Mn_element
FEATURE [App::DocumentObjectGroupPython] G4_Mn  # scripted group (container) (typed FeaturePython)
  Dunit = g/cm3
  Dvalue = 7.44
  Group = -> [Mn_element001]
  conduct = 2
  density = 1
  expand = 3
  formula = Mn
  name = G4_Mn
  specific = 4
FEATURE [App::DocumentObjectGroupPython] Fe_element007  label="Fe_element : 004"  # scripted group (container) (typed FeaturePython)
  n = 1
  ref = Fe_element
FEATURE [App::DocumentObjectGroupPython] G4_Fe  # scripted group (container) (typed FeaturePython)
  Dunit = g/cm3
  Dvalue = 7.874
  Group = -> [Fe_element007]
  conduct = 2
  density = 1
  expand = 3
  formula = Fe
  name = G4_Fe
  specific = 4
FEATURE [App::DocumentObjectGroupPython] Co_element001  label="Co_element : 1"  # scripted group (container) (typed FeaturePython)
  n = 1
  ref = Co_element
FEATURE [App::DocumentObjectGroupPython] G4_Co  # scripted group (container) (typed FeaturePython)
  Dunit = g/cm3
  Dvalue = 8.9
  Group = -> [Co_element001]
  conduct = 2
  density = 1
  expand = 3
  formula = Co
  name = G4_Co
  specific = 4
FEATURE [App::DocumentObjectGroupPython] Ni_element001  label="Ni_element : 1"  # scripted group (container) (typed FeaturePython)
  n = 1
  ref = Ni_element
FEATURE [App::DocumentObjectGroupPython] G4_Ni  # scripted group (container) (typed FeaturePython)
  Dunit = g/cm3
  Dvalue = 8.902
  Group = -> [Ni_element001]
  conduct = 2
  density = 1
  expand = 3
  formula = Ni
  name = G4_Ni
  specific = 4
FEATURE [App::DocumentObjectGroupPython] Cu_element001  label="Cu_element : 1"  # scripted group (container) (typed FeaturePython)
  n = 1
  ref = Cu_element
FEATURE [App::DocumentObjectGroupPython] G4_Cu  # scripted group (container) (typed FeaturePython)
  Dunit = g/cm3
  Dvalue = 8.96
  Group = -> [Cu_element001]
  conduct = 2
  density = 1
  expand = 3
  formula = Cu
  name = G4_Cu
  specific = 4
FEATURE [App::DocumentObjectGroupPython] Zn_element001  label="Zn_element : 1"  # scripted group (container) (typed FeaturePython)
  n = 1
  ref = Zn_element
FEATURE [App::DocumentObjectGroupPython] G4_Zn  # scripted group (container) (typed FeaturePython)
  Dunit = g/cm3
  Dvalue = 7.133
  Group = -> [Zn_element001]
  conduct = 2
  density = 1
  expand = 3
  formula = Zn
  name = G4_Zn
  specific = 4
FEATURE [App::DocumentObjectGroupPython] Ga_element002  label="Ga_element : 002"  # scripted group (container) (typed FeaturePython)
  n = 1
  ref = Ga_element
FEATURE [App::DocumentObjectGroupPython] G4_Ga  # scripted group (container) (typed FeaturePython)
  Dunit = g/cm3
  Dvalue = 5.904
  Group = -> [Ga_element002]
  conduct = 2
  density = 1
  expand = 3
  formula = Ga
  name = G4_Ga
  specific = 4
FEATURE [App::DocumentObjectGroupPython] Ge_element002  label="Ge_element : 1"  # scripted group (container) (typed FeaturePython)
  n = 1
  ref = Ge_element
FEATURE [App::DocumentObjectGroupPython] G4_Ge  # scripted group (container) (typed FeaturePython)
  Dunit = g/cm3
  Dvalue = 5.323
  Group = -> [Ge_element002]
  conduct = 2
  density = 1
  expand = 3
  formula = Ge
  name = G4_Ge
  specific = 4
FEATURE [App::DocumentObjectGroupPython] As_element003  label="As_element : 002"  # scripted group (container) (typed FeaturePython)
  n = 1
  ref = As_element
FEATURE [App::DocumentObjectGroupPython] G4_As  # scripted group (container) (typed FeaturePython)
  Dunit = g/cm3
  Dvalue = 5.73
  Group = -> [As_element003]
  conduct = 2
  density = 1
  expand = 3
  formula = As
  name = G4_As
  specific = 4
FEATURE [App::DocumentObjectGroupPython] Se_element001  label="Se_element : 1"  # scripted group (container) (typed FeaturePython)
  n = 1
  ref = Se_element
FEATURE [App::DocumentObjectGroupPython] G4_Se  # scripted group (container) (typed FeaturePython)
  Dunit = g/cm3
  Dvalue = 4.5
  Group = -> [Se_element001]
  conduct = 2
  density = 1
  expand = 3
  formula = Se
  name = G4_Se
  specific = 4
FEATURE [App::DocumentObjectGroupPython] Br_element007  label="Br_element : 004"  # scripted group (container) (typed FeaturePython)
  n = 1
  ref = Br_element
FEATURE [App::DocumentObjectGroupPython] G4_Br  # scripted group (container) (typed FeaturePython)
  Dunit = g/cm3
  Dvalue = 0.0070721
  Group = -> [Br_element007]
  conduct = 2
  density = 1
  expand = 3
  formula = Br
  name = G4_Br
  specific = 4
FEATURE [App::DocumentObjectGroupPython] Kr_element001  label="Kr_element : 1"  # scripted group (container) (typed FeaturePython)
  n = 1
  ref = Kr_element
FEATURE [App::DocumentObjectGroupPython] G4_Kr  # scripted group (container) (typed FeaturePython)
  Dunit = g/cm3
  Dvalue = 0.00347832
  Group = -> [Kr_element001]
  conduct = 2
  density = 1
  expand = 3
  formula = Kr
  name = G4_Kr
  specific = 4
FEATURE [App::DocumentObjectGroupPython] Rb_element001  label="Rb_element : 1"  # scripted group (container) (typed FeaturePython)
  n = 1
  ref = Rb_element
FEATURE [App::DocumentObjectGroupPython] G4_Rb  # scripted group (container) (typed FeaturePython)
  Dunit = g/cm3
  Dvalue = 1.532
  Group = -> [Rb_element001]
  conduct = 2
  density = 1
  expand = 3
  formula = Rb
  name = G4_Rb
  specific = 4
FEATURE [App::DocumentObjectGroupPython] Sr_element001  label="Sr_element : 1"  # scripted group (container) (typed FeaturePython)
  n = 1
  ref = Sr_element
FEATURE [App::DocumentObjectGroupPython] G4_Sr  # scripted group (container) (typed FeaturePython)
  Dunit = g/cm3
  Dvalue = 2.54
  Group = -> [Sr_element001]
  conduct = 2
  density = 1
  expand = 3
  formula = Sr
  name = G4_Sr
  specific = 4
FEATURE [App::DocumentObjectGroupPython] Y_element001  label="Y_element : 1"  # scripted group (container) (typed FeaturePython)
  n = 1
  ref = Y_element
FEATURE [App::DocumentObjectGroupPython] G4_Y  # scripted group (container) (typed FeaturePython)
  Dunit = g/cm3
  Dvalue = 4.469
  Group = -> [Y_element001]
  conduct = 2
  density = 1
  expand = 3
  formula = Y
  name = G4_Y
  specific = 4
FEATURE [App::DocumentObjectGroupPython] Zr_element001  label="Zr_element : 1"  # scripted group (container) (typed FeaturePython)
  n = 1
  ref = Zr_element
FEATURE [App::DocumentObjectGroupPython] G4_Zr  # scripted group (container) (typed FeaturePython)
  Dunit = g/cm3
  Dvalue = 6.506
  Group = -> [Zr_element001]
  conduct = 2
  density = 1
  expand = 3
  formula = Zr
  name = G4_Zr
  specific = 4
FEATURE [App::DocumentObjectGroupPython] Nb_element001  label="Nb_element : 1"  # scripted group (container) (typed FeaturePython)
  n = 1
  ref = Nb_element
FEATURE [App::DocumentObjectGroupPython] G4_Nb  # scripted group (container) (typed FeaturePython)
  Dunit = g/cm3
  Dvalue = 8.57
  Group = -> [Nb_element001]
  conduct = 2
  density = 1
  expand = 3
  formula = Nb
  name = G4_Nb
  specific = 4
FEATURE [App::DocumentObjectGroupPython] Mo_element001  label="Mo_element : 1"  # scripted group (container) (typed FeaturePython)
  n = 1
  ref = Mo_element
FEATURE [App::DocumentObjectGroupPython] G4_Mo  # scripted group (container) (typed FeaturePython)
  Dunit = g/cm3
  Dvalue = 10.22
  Group = -> [Mo_element001]
  conduct = 2
  density = 1
  expand = 3
  formula = Mo
  name = G4_Mo
  specific = 4
FEATURE [App::DocumentObjectGroupPython] Tc_element001  label="Tc_element : 1"  # scripted group (container) (typed FeaturePython)
  n = 1
  ref = Tc_element
FEATURE [App::DocumentObjectGroupPython] G4_Tc  # scripted group (container) (typed FeaturePython)
  Dunit = g/cm3
  Dvalue = 11.5
  Group = -> [Tc_element001]
  conduct = 2
  density = 1
  expand = 3
  formula = Tc
  name = G4_Tc
  specific = 4
FEATURE [App::DocumentObjectGroupPython] Ru_element001  label="Ru_element : 1"  # scripted group (container) (typed FeaturePython)
  n = 1
  ref = Ru_element
FEATURE [App::DocumentObjectGroupPython] G4_Ru  # scripted group (container) (typed FeaturePython)
  Dunit = g/cm3
  Dvalue = 12.41
  Group = -> [Ru_element001]
  conduct = 2
  density = 1
  expand = 3
  formula = Ru
  name = G4_Ru
  specific = 4
FEATURE [App::DocumentObjectGroupPython] Rh_element001  label="Rh_element : 1"  # scripted group (container) (typed FeaturePython)
  n = 1
  ref = Rh_element
FEATURE [App::DocumentObjectGroupPython] G4_Rh  # scripted group (container) (typed FeaturePython)
  Dunit = g/cm3
  Dvalue = 12.41
  Group = -> [Rh_element001]
  conduct = 2
  density = 1
  expand = 3
  formula = Rh
  name = G4_Rh
  specific = 4
FEATURE [App::DocumentObjectGroupPython] Pd_element001  label="Pd_element : 1"  # scripted group (container) (typed FeaturePython)
  n = 1
  ref = Pd_element
FEATURE [App::DocumentObjectGroupPython] G4_Pd  # scripted group (container) (typed FeaturePython)
  Dunit = g/cm3
  Dvalue = 12.02
  Group = -> [Pd_element001]
  conduct = 2
  density = 1
  expand = 3
  formula = Pd
  name = G4_Pd
  specific = 4
FEATURE [App::DocumentObjectGroupPython] Ag_element006  label="Ag_element : 004"  # scripted group (container) (typed FeaturePython)
  n = 1
  ref = Ag_element
FEATURE [App::DocumentObjectGroupPython] G4_Ag  # scripted group (container) (typed FeaturePython)
  Dunit = g/cm3
  Dvalue = 10.5
  Group = -> [Ag_element006]
  conduct = 2
  density = 1
  expand = 3
  formula = Ag
  name = G4_Ag
  specific = 4
FEATURE [App::DocumentObjectGroupPython] Cd_element003  label="Cd_element : 003"  # scripted group (container) (typed FeaturePython)
  n = 1
  ref = Cd_element
FEATURE [App::DocumentObjectGroupPython] G4_Cd  # scripted group (container) (typed FeaturePython)
  Dunit = g/cm3
  Dvalue = 8.65
  Group = -> [Cd_element003]
  conduct = 2
  density = 1
  expand = 3
  formula = Cd
  name = G4_Cd
  specific = 4
FEATURE [App::DocumentObjectGroupPython] In_element001  label="In_element : 1"  # scripted group (container) (typed FeaturePython)
  n = 1
  ref = In_element
FEATURE [App::DocumentObjectGroupPython] G4_In  # scripted group (container) (typed FeaturePython)
  Dunit = g/cm3
  Dvalue = 7.31
  Group = -> [In_element001]
  conduct = 2
  density = 1
  expand = 3
  formula = In
  name = G4_In
  specific = 4
FEATURE [App::DocumentObjectGroupPython] Sn_element001  label="Sn_element : 1"  # scripted group (container) (typed FeaturePython)
  n = 1
  ref = Sn_element
FEATURE [App::DocumentObjectGroupPython] G4_Sn  # scripted group (container) (typed FeaturePython)
  Dunit = g/cm3
  Dvalue = 7.31
  Group = -> [Sn_element001]
  conduct = 2
  density = 1
  expand = 3
  formula = Sn
  name = G4_Sn
  specific = 4
FEATURE [App::DocumentObjectGroupPython] Sb_element001  label="Sb_element : 1"  # scripted group (container) (typed FeaturePython)
  n = 1
  ref = Sb_element
FEATURE [App::DocumentObjectGroupPython] G4_Sb  # scripted group (container) (typed FeaturePython)
  Dunit = g/cm3
  Dvalue = 6.691
  Group = -> [Sb_element001]
  conduct = 2
  density = 1
  expand = 3
  formula = Sb
  name = G4_Sb
  specific = 4
FEATURE [App::DocumentObjectGroupPython] Te_element002  label="Te_element : 002"  # scripted group (container) (typed FeaturePython)
  n = 1
  ref = Te_element
FEATURE [App::DocumentObjectGroupPython] G4_Te  # scripted group (container) (typed FeaturePython)
  Dunit = g/cm3
  Dvalue = 6.24
  Group = -> [Te_element002]
  conduct = 2
  density = 1
  expand = 3
  formula = Te
  name = G4_Te
  specific = 4
FEATURE [App::DocumentObjectGroupPython] I_element010  label="I_element : 006"  # scripted group (container) (typed FeaturePython)
  n = 1
  ref = I_element
FEATURE [App::DocumentObjectGroupPython] G4_I  # scripted group (container) (typed FeaturePython)
  Dunit = g/cm3
  Dvalue = 4.93
  Group = -> [I_element010]
  conduct = 2
  density = 1
  expand = 3
  formula = I
  name = G4_I
  specific = 4
FEATURE [App::DocumentObjectGroupPython] Xe_element001  label="Xe_element : 1"  # scripted group (container) (typed FeaturePython)
  n = 1
  ref = Xe_element
FEATURE [App::DocumentObjectGroupPython] G4_Xe  # scripted group (container) (typed FeaturePython)
  Dunit = g/cm3
  Dvalue = 0.00548536
  Group = -> [Xe_element001]
  conduct = 2
  density = 1
  expand = 3
  formula = Xe
  name = G4_Xe
  specific = 4
FEATURE [App::DocumentObjectGroupPython] Cs_element003  label="Cs_element : 003"  # scripted group (container) (typed FeaturePython)
  n = 1
  ref = Cs_element
FEATURE [App::DocumentObjectGroupPython] G4_Cs  # scripted group (container) (typed FeaturePython)
  Dunit = g/cm3
  Dvalue = 1.873
  Group = -> [Cs_element003]
  conduct = 2
  density = 1
  expand = 3
  formula = Cs
  name = G4_Cs
  specific = 4
FEATURE [App::DocumentObjectGroupPython] Ba_element003  label="Ba_element : 003"  # scripted group (container) (typed FeaturePython)
  n = 1
  ref = Ba_element
FEATURE [App::DocumentObjectGroupPython] G4_Ba  # scripted group (container) (typed FeaturePython)
  Dunit = g/cm3
  Dvalue = 3.5
  Group = -> [Ba_element003]
  conduct = 2
  density = 1
  expand = 3
  formula = Ba
  name = G4_Ba
  specific = 4
FEATURE [App::DocumentObjectGroupPython] La_element003  label="La_element : 003"  # scripted group (container) (typed FeaturePython)
  n = 1
  ref = La_element
FEATURE [App::DocumentObjectGroupPython] G4_La  # scripted group (container) (typed FeaturePython)
  Dunit = g/cm3
  Dvalue = 6.154
  Group = -> [La_element003]
  conduct = 2
  density = 1
  expand = 3
  formula = La
  name = G4_La
  specific = 4
FEATURE [App::DocumentObjectGroupPython] Ce_element002  label="Ce_element : 1"  # scripted group (container) (typed FeaturePython)
  n = 1
  ref = Ce_element
FEATURE [App::DocumentObjectGroupPython] G4_Ce  # scripted group (container) (typed FeaturePython)
  Dunit = g/cm3
  Dvalue = 6.657
  Group = -> [Ce_element002]
  conduct = 2
  density = 1
  expand = 3
  formula = Ce
  name = G4_Ce
  specific = 4
FEATURE [App::DocumentObjectGroupPython] Pr_element001  label="Pr_element : 1"  # scripted group (container) (typed FeaturePython)
  n = 1
  ref = Pr_element
FEATURE [App::DocumentObjectGroupPython] G4_Pr  # scripted group (container) (typed FeaturePython)
  Dunit = g/cm3
  Dvalue = 6.71
  Group = -> [Pr_element001]
  conduct = 2
  density = 1
  expand = 3
  formula = Pr
  name = G4_Pr
  specific = 4
FEATURE [App::DocumentObjectGroupPython] Nd_element001  label="Nd_element : 1"  # scripted group (container) (typed FeaturePython)
  n = 1
  ref = Nd_element
FEATURE [App::DocumentObjectGroupPython] G4_Nd  # scripted group (container) (typed FeaturePython)
  Dunit = g/cm3
  Dvalue = 6.9
  Group = -> [Nd_element001]
  conduct = 2
  density = 1
  expand = 3
  formula = Nd
  name = G4_Nd
  specific = 4
FEATURE [App::DocumentObjectGroupPython] Pm_element001  label="Pm_element : 1"  # scripted group (container) (typed FeaturePython)
  n = 1
  ref = Pm_element
FEATURE [App::DocumentObjectGroupPython] G4_Pm  # scripted group (container) (typed FeaturePython)
  Dunit = g/cm3
  Dvalue = 7.22
  Group = -> [Pm_element001]
  conduct = 2
  density = 1
  expand = 3
  formula = Pm
  name = G4_Pm
  specific = 4
FEATURE [App::DocumentObjectGroupPython] Sm_element001  label="Sm_element : 1"  # scripted group (container) (typed FeaturePython)
  n = 1
  ref = Sm_element
FEATURE [App::DocumentObjectGroupPython] G4_Sm  # scripted group (container) (typed FeaturePython)
  Dunit = g/cm3
  Dvalue = 7.46
  Group = -> [Sm_element001]
  conduct = 2
  density = 1
  expand = 3
  formula = Sm
  name = G4_Sm
  specific = 4
FEATURE [App::DocumentObjectGroupPython] Eu_element001  label="Eu_element : 1"  # scripted group (container) (typed FeaturePython)
  n = 1
  ref = Eu_element
FEATURE [App::DocumentObjectGroupPython] G4_Eu  # scripted group (container) (typed FeaturePython)
  Dunit = g/cm3
  Dvalue = 5.243
  Group = -> [Eu_element001]
  conduct = 2
  density = 1
  expand = 3
  formula = Eu
  name = G4_Eu
  specific = 4
FEATURE [App::DocumentObjectGroupPython] Gd_element002  label="Gd_element : 1"  # scripted group (container) (typed FeaturePython)
  n = 1
  ref = Gd_element
FEATURE [App::DocumentObjectGroupPython] G4_Gd  # scripted group (container) (typed FeaturePython)
  Dunit = g/cm3
  Dvalue = 7.9004
  Group = -> [Gd_element002]
  conduct = 2
  density = 1
  expand = 3
  formula = Gd
  name = G4_Gd
  specific = 4
FEATURE [App::DocumentObjectGroupPython] Tb_element001  label="Tb_element : 1"  # scripted group (container) (typed FeaturePython)
  n = 1
  ref = Tb_element
FEATURE [App::DocumentObjectGroupPython] G4_Tb  # scripted group (container) (typed FeaturePython)
  Dunit = g/cm3
  Dvalue = 8.229
  Group = -> [Tb_element001]
  conduct = 2
  density = 1
  expand = 3
  formula = Tb
  name = G4_Tb
  specific = 4
FEATURE [App::DocumentObjectGroupPython] Dy_element001  label="Dy_element : 1"  # scripted group (container) (typed FeaturePython)
  n = 1
  ref = Dy_element
FEATURE [App::DocumentObjectGroupPython] G4_Dy  # scripted group (container) (typed FeaturePython)
  Dunit = g/cm3
  Dvalue = 8.55
  Group = -> [Dy_element001]
  conduct = 2
  density = 1
  expand = 3
  formula = Dy
  name = G4_Dy
  specific = 4
FEATURE [App::DocumentObjectGroupPython] Ho_element001  label="Ho_element : 1"  # scripted group (container) (typed FeaturePython)
  n = 1
  ref = Ho_element
FEATURE [App::DocumentObjectGroupPython] G4_Ho  # scripted group (container) (typed FeaturePython)
  Dunit = g/cm3
  Dvalue = 8.795
  Group = -> [Ho_element001]
  conduct = 2
  density = 1
  expand = 3
  formula = Ho
  name = G4_Ho
  specific = 4
FEATURE [App::DocumentObjectGroupPython] Er_element001  label="Er_element : 1"  # scripted group (container) (typed FeaturePython)
  n = 1
  ref = Er_element
FEATURE [App::DocumentObjectGroupPython] G4_Er  # scripted group (container) (typed FeaturePython)
  Dunit = g/cm3
  Dvalue = 9.066
  Group = -> [Er_element001]
  conduct = 2
  density = 1
  expand = 3
  formula = Er
  name = G4_Er
  specific = 4
FEATURE [App::DocumentObjectGroupPython] Tm_element001  label="Tm_element : 1"  # scripted group (container) (typed FeaturePython)
  n = 1
  ref = Tm_element
FEATURE [App::DocumentObjectGroupPython] G4_Tm  # scripted group (container) (typed FeaturePython)
  Dunit = g/cm3
  Dvalue = 9.321
  Group = -> [Tm_element001]
  conduct = 2
  density = 1
  expand = 3
  formula = Tm
  name = G4_Tm
  specific = 4
FEATURE [App::DocumentObjectGroupPython] Yb_element001  label="Yb_element : 1"  # scripted group (container) (typed FeaturePython)
  n = 1
  ref = Yb_element
FEATURE [App::DocumentObjectGroupPython] G4_Yb  # scripted group (container) (typed FeaturePython)
  Dunit = g/cm3
  Dvalue = 6.73
  Group = -> [Yb_element001]
  conduct = 2
  density = 1
  expand = 3
  formula = Yb
  name = G4_Yb
  specific = 4
FEATURE [App::DocumentObjectGroupPython] Lu_element001  label="Lu_element : 1"  # scripted group (container) (typed FeaturePython)
  n = 1
  ref = Lu_element
FEATURE [App::DocumentObjectGroupPython] G4_Lu  # scripted group (container) (typed FeaturePython)
  Dunit = g/cm3
  Dvalue = 9.84
  Group = -> [Lu_element001]
  conduct = 2
  density = 1
  expand = 3
  formula = Lu
  name = G4_Lu
  specific = 4
FEATURE [App::DocumentObjectGroupPython] Hf_element001  label="Hf_element : 1"  # scripted group (container) (typed FeaturePython)
  n = 1
  ref = Hf_element
FEATURE [App::DocumentObjectGroupPython] G4_Hf  # scripted group (container) (typed FeaturePython)
  Dunit = g/cm3
  Dvalue = 13.31
  Group = -> [Hf_element001]
  conduct = 2
  density = 1
  expand = 3
  formula = Hf
  name = G4_Hf
  specific = 4
FEATURE [App::DocumentObjectGroupPython] Ta_element001  label="Ta_element : 1"  # scripted group (container) (typed FeaturePython)
  n = 1
  ref = Ta_element
FEATURE [App::DocumentObjectGroupPython] G4_Ta  # scripted group (container) (typed FeaturePython)
  Dunit = g/cm3
  Dvalue = 16.654
  Group = -> [Ta_element001]
  conduct = 2
  density = 1
  expand = 3
  formula = Ta
  name = G4_Ta
  specific = 4
FEATURE [App::DocumentObjectGroupPython] W_element004  label="W_element : 004"  # scripted group (container) (typed FeaturePython)
  n = 1
  ref = W_element
FEATURE [App::DocumentObjectGroupPython] G4_W  # scripted group (container) (typed FeaturePython)
  Dunit = g/cm3
  Dvalue = 19.3
  Group = -> [W_element004]
  conduct = 2
  density = 1
  expand = 3
  formula = W
  name = G4_W
  specific = 4
FEATURE [App::DocumentObjectGroupPython] Re_element001  label="Re_element : 1"  # scripted group (container) (typed FeaturePython)
  n = 1
  ref = Re_element
FEATURE [App::DocumentObjectGroupPython] G4_Re  # scripted group (container) (typed FeaturePython)
  Dunit = g/cm3
  Dvalue = 21.02
  Group = -> [Re_element001]
  conduct = 2
  density = 1
  expand = 3
  formula = Re
  name = G4_Re
  specific = 4
FEATURE [App::DocumentObjectGroupPython] Os_element001  label="Os_element : 1"  # scripted group (container) (typed FeaturePython)
  n = 1
  ref = Os_element
FEATURE [App::DocumentObjectGroupPython] G4_Os  # scripted group (container) (typed FeaturePython)
  Dunit = g/cm3
  Dvalue = 22.57
  Group = -> [Os_element001]
  conduct = 2
  density = 1
  expand = 3
  formula = Os
  name = G4_Os
  specific = 4
FEATURE [App::DocumentObjectGroupPython] Ir_element001  label="Ir_element : 1"  # scripted group (container) (typed FeaturePython)
  n = 1
  ref = Ir_element
FEATURE [App::DocumentObjectGroupPython] G4_Ir  # scripted group (container) (typed FeaturePython)
  Dunit = g/cm3
  Dvalue = 22.42
  Group = -> [Ir_element001]
  conduct = 2
  density = 1
  expand = 3
  formula = Ir
  name = G4_Ir
  specific = 4
FEATURE [App::DocumentObjectGroupPython] Pt_element001  label="Pt_element : 1"  # scripted group (container) (typed FeaturePython)
  n = 1
  ref = Pt_element
FEATURE [App::DocumentObjectGroupPython] G4_Pt  # scripted group (container) (typed FeaturePython)
  Dunit = g/cm3
  Dvalue = 21.45
  Group = -> [Pt_element001]
  conduct = 2
  density = 1
  expand = 3
  formula = Pt
  name = G4_Pt
  specific = 4
FEATURE [App::DocumentObjectGroupPython] Au_element001  label="Au_element : 1"  # scripted group (container) (typed FeaturePython)
  n = 1
  ref = Au_element
FEATURE [App::DocumentObjectGroupPython] G4_Au  # scripted group (container) (typed FeaturePython)
  Dunit = g/cm3
  Dvalue = 19.32
  Group = -> [Au_element001]
  conduct = 2
  density = 1
  expand = 3
  formula = Au
  name = G4_Au
  specific = 4
FEATURE [App::DocumentObjectGroupPython] Hg_element002  label="Hg_element : 002"  # scripted group (container) (typed FeaturePython)
  n = 1
  ref = Hg_element
FEATURE [App::DocumentObjectGroupPython] G4_Hg  # scripted group (container) (typed FeaturePython)
  Dunit = g/cm3
  Dvalue = 13.546
  Group = -> [Hg_element002]
  conduct = 2
  density = 1
  expand = 3
  formula = Hg
  name = G4_Hg
  specific = 4
FEATURE [App::DocumentObjectGroupPython] Tl_element002  label="Tl_element : 002"  # scripted group (container) (typed FeaturePython)
  n = 1
  ref = Tl_element
FEATURE [App::DocumentObjectGroupPython] G4_Tl  # scripted group (container) (typed FeaturePython)
  Dunit = g/cm3
  Dvalue = 11.72
  Group = -> [Tl_element002]
  conduct = 2
  density = 1
  expand = 3
  formula = Tl
  name = G4_Tl
  specific = 4
FEATURE [App::DocumentObjectGroupPython] Pb_element003  label="Pb_element : 1"  # scripted group (container) (typed FeaturePython)
  n = 1
  ref = Pb_element
FEATURE [App::DocumentObjectGroupPython] G4_Pb  # scripted group (container) (typed FeaturePython)
  Dunit = g/cm3
  Dvalue = 11.35
  Group = -> [Pb_element003]
  conduct = 2
  density = 1
  expand = 3
  formula = Pb
  name = G4_Pb
  specific = 4
FEATURE [App::DocumentObjectGroupPython] Bi_element002  label="Bi_element : 1"  # scripted group (container) (typed FeaturePython)
  n = 1
  ref = Bi_element
FEATURE [App::DocumentObjectGroupPython] G4_Bi  # scripted group (container) (typed FeaturePython)
  Dunit = g/cm3
  Dvalue = 9.747
  Group = -> [Bi_element002]
  conduct = 2
  density = 1
  expand = 3
  formula = Bi
  name = G4_Bi
  specific = 4
FEATURE [App::DocumentObjectGroupPython] Po_element001  label="Po_element : 1"  # scripted group (container) (typed FeaturePython)
  n = 1
  ref = Po_element
FEATURE [App::DocumentObjectGroupPython] G4_Po  # scripted group (container) (typed FeaturePython)
  Dunit = g/cm3
  Dvalue = 9.32
  Group = -> [Po_element001]
  conduct = 2
  density = 1
  expand = 3
  formula = Po
  name = G4_Po
  specific = 4
FEATURE [App::DocumentObjectGroupPython] At_element001  label="At_element : 1"  # scripted group (container) (typed FeaturePython)
  n = 1
  ref = At_element
FEATURE [App::DocumentObjectGroupPython] G4_At  # scripted group (container) (typed FeaturePython)
  Dunit = g/cm3
  Dvalue = 9.32
  Group = -> [At_element001]
  conduct = 2
  density = 1
  expand = 3
  formula = At
  name = G4_At
  specific = 4
FEATURE [App::DocumentObjectGroupPython] Rn_element001  label="Rn_element : 1"  # scripted group (container) (typed FeaturePython)
  n = 1
  ref = Rn_element
FEATURE [App::DocumentObjectGroupPython] G4_Rn  # scripted group (container) (typed FeaturePython)
  Dunit = g/cm3
  Dvalue = 0.00900662
  Group = -> [Rn_element001]
  conduct = 2
  density = 1
  expand = 3
  formula = Rn
  name = G4_Rn
  specific = 4
FEATURE [App::DocumentObjectGroupPython] Fr_element001  label="Fr_element : 1"  # scripted group (container) (typed FeaturePython)
  n = 1
  ref = Fr_element
FEATURE [App::DocumentObjectGroupPython] G4_Fr  # scripted group (container) (typed FeaturePython)
  Dunit = g/cm3
  Dvalue = 1
  Group = -> [Fr_element001]
  conduct = 2
  density = 1
  expand = 3
  formula = Fr
  name = G4_Fr
  specific = 4
FEATURE [App::DocumentObjectGroupPython] Ra_element001  label="Ra_element : 1"  # scripted group (container) (typed FeaturePython)
  n = 1
  ref = Ra_element
FEATURE [App::DocumentObjectGroupPython] G4_Ra  # scripted group (container) (typed FeaturePython)
  Dunit = g/cm3
  Dvalue = 5
  Group = -> [Ra_element001]
  conduct = 2
  density = 1
  expand = 3
  formula = Ra
  name = G4_Ra
  specific = 4
FEATURE [App::DocumentObjectGroupPython] Ac_element001  label="Ac_element : 1"  # scripted group (container) (typed FeaturePython)
  n = 1
  ref = Ac_element
FEATURE [App::DocumentObjectGroupPython] G4_Ac  # scripted group (container) (typed FeaturePython)
  Dunit = g/cm3
  Dvalue = 10.07
  Group = -> [Ac_element001]
  conduct = 2
  density = 1
  expand = 3
  formula = Ac
  name = G4_Ac
  specific = 4
FEATURE [App::DocumentObjectGroupPython] Th_element001  label="Th_element : 1"  # scripted group (container) (typed FeaturePython)
  n = 1
  ref = Th_element
FEATURE [App::DocumentObjectGroupPython] G4_Th  # scripted group (container) (typed FeaturePython)
  Dunit = g/cm3
  Dvalue = 11.72
  Group = -> [Th_element001]
  conduct = 2
  density = 1
  expand = 3
  formula = Th
  name = G4_Th
  specific = 4
FEATURE [App::DocumentObjectGroupPython] Pa_element001  label="Pa_element : 1"  # scripted group (container) (typed FeaturePython)
  n = 1
  ref = Pa_element
FEATURE [App::DocumentObjectGroupPython] G4_Pa  # scripted group (container) (typed FeaturePython)
  Dunit = g/cm3
  Dvalue = 15.37
  Group = -> [Pa_element001]
  conduct = 2
  density = 1
  expand = 3
  formula = Pa
  name = G4_Pa
  specific = 4
FEATURE [App::DocumentObjectGroupPython] U_element004  label="U_element : 004"  # scripted group (container) (typed FeaturePython)
  n = 1
  ref = U_element
FEATURE [App::DocumentObjectGroupPython] G4_U  # scripted group (container) (typed FeaturePython)
  Dunit = g/cm3
  Dvalue = 18.95
  Group = -> [U_element004]
  conduct = 2
  density = 1
  expand = 3
  formula = U
  name = G4_U
  specific = 4
FEATURE [App::DocumentObjectGroupPython] Np_element001  label="Np_element : 1"  # scripted group (container) (typed FeaturePython)
  n = 1
  ref = Np_element
FEATURE [App::DocumentObjectGroupPython] G4_Np  # scripted group (container) (typed FeaturePython)
  Dunit = g/cm3
  Dvalue = 20.25
  Group = -> [Np_element001]
  conduct = 2
  density = 1
  expand = 3
  formula = Np
  name = G4_Np
  specific = 4
FEATURE [App::DocumentObjectGroupPython] Pu_element002  label="Pu_element : 002"  # scripted group (container) (typed FeaturePython)
  n = 1
  ref = Pu_element
FEATURE [App::DocumentObjectGroupPython] G4_Pu  # scripted group (container) (typed FeaturePython)
  Dunit = g/cm3
  Dvalue = 19.84
  Group = -> [Pu_element002]
  conduct = 2
  density = 1
  expand = 3
  formula = Pu
  name = G4_Pu
  specific = 4
FEATURE [App::DocumentObjectGroupPython] Am_element001  label="Am_element : 1"  # scripted group (container) (typed FeaturePython)
  n = 1
  ref = Am_element
FEATURE [App::DocumentObjectGroupPython] G4_Am  # scripted group (container) (typed FeaturePython)
  Dunit = g/cm3
  Dvalue = 13.67
  Group = -> [Am_element001]
  conduct = 2
  density = 1
  expand = 3
  formula = Am
  name = G4_Am
  specific = 4
FEATURE [App::DocumentObjectGroupPython] Cm_element001  label="Cm_element : 1"  # scripted group (container) (typed FeaturePython)
  n = 1
  ref = Cm_element
FEATURE [App::DocumentObjectGroupPython] G4_Cm  # scripted group (container) (typed FeaturePython)
  Dunit = g/cm3
  Dvalue = 13.51
  Group = -> [Cm_element001]
  conduct = 2
  density = 1
  expand = 3
  formula = Cm
  name = G4_Cm
  specific = 4
FEATURE [App::DocumentObjectGroupPython] Bk_element001  label="Bk_element : 1"  # scripted group (container) (typed FeaturePython)
  n = 1
  ref = Bk_element
FEATURE [App::DocumentObjectGroupPython] G4_Bk  # scripted group (container) (typed FeaturePython)
  Dunit = g/cm3
  Dvalue = 14
  Group = -> [Bk_element001]
  conduct = 2
  density = 1
  expand = 3
  formula = Bk
  name = G4_Bk
  specific = 4
FEATURE [App::DocumentObjectGroupPython] Cf_element001  label="Cf_element : 1"  # scripted group (container) (typed FeaturePython)
  n = 1
  ref = Cf_element
FEATURE [App::DocumentObjectGroupPython] G4_Cf  # scripted group (container) (typed FeaturePython)
  Dunit = g/cm3
  Dvalue = 10
  Group = -> [Cf_element001]
  conduct = 2
  density = 1
  expand = 3
  formula = Cf
  name = G4_Cf
  specific = 4
FEATURE [App::DocumentObjectGroupPython] Element  # scripted group (container) (typed FeaturePython)
  Group = -> [G4_H,G4_He,G4_Li,G4_Be,G4_B,G4_C,G4_N,G4_O,G4_F,G4_Ne,G4_Na,G4_Mg,G4_Al,G4_Si,G4_P,G4_S,G4_Cl,G4_Ar,G4_K,G4_Ca,G4_Sc,G4_Ti,G4_V,G4_Cr,G4_Mn,G4_Fe,G4_Co,G4_Ni,G4_Cu,G4_Zn,G4_Ga,G4_Ge,G4_As,G4_Se,G4_Br,G4_Kr,G4_Rb,G4_Sr,G4_Y,G4_Zr,G4_Nb,G4_Mo,G4_Tc,G4_Ru,G4_Rh,G4_Pd,G4_Ag,G4_Cd,G4_In,G4_Sn,G4_Sb,G4_Te,G4_I,G4_Xe,G4_Cs,G4_Ba,G4_La,G4_Ce,G4_Pr,G4_Nd,G4_Pm,G4_Sm,G4_Eu,G4_Gd,G4_Tb,G4_Dy,G4_Ho,G4_Er,+30 more]
FEATURE [App::DocumentObjectGroupPython] H_element114  label="H_element : 063"  # scripted group (container) (typed FeaturePython)
  n = 2
  ref = H_element
FEATURE [App::DocumentObjectGroupPython] G4_lH2  # scripted group (container) (typed FeaturePython)
  Dunit = g/cm3
  Dvalue = 0.0708
  Group = -> [H_element114]
  conduct = 2
  density = 1
  expand = 3
  formula = G4_lH2
  name = G4_lH2
  specific = 4
FEATURE [App::DocumentObjectGroupPython] N_element049  label="N_element : 022"  # scripted group (container) (typed FeaturePython)
  n = 2
  ref = N_element
FEATURE [App::DocumentObjectGroupPython] G4_lN2  # scripted group (container) (typed FeaturePython)
  Dunit = g/cm3
  Dvalue = 0.807
  Group = -> [N_element049]
  conduct = 2
  density = 1
  expand = 3
  formula = G4_lN2
  name = G4_lN2
  specific = 4
FEATURE [App::DocumentObjectGroupPython] O_element106  label="O_element : 060"  # scripted group (container) (typed FeaturePython)
  n = 2
  ref = O_element
FEATURE [App::DocumentObjectGroupPython] G4_lO2  # scripted group (container) (typed FeaturePython)
  Dunit = g/cm3
  Dvalue = 1.141
  Group = -> [O_element106]
  conduct = 2
  density = 1
  expand = 3
  formula = G4_lO2
  name = G4_lO2
  specific = 4
FEATURE [App::DocumentObjectGroupPython] Ar_element003  label="Ar_element : 002"  # scripted group (container) (typed FeaturePython)
  n = 1
  ref = Ar_element
FEATURE [App::DocumentObjectGroupPython] G4_lAr  # scripted group (container) (typed FeaturePython)
  Dunit = g/cm3
  Dvalue = 1.396
  Group = -> [Ar_element003]
  conduct = 2
  density = 1
  expand = 3
  formula = G4_lAr
  name = G4_lAr
  specific = 4
FEATURE [App::DocumentObjectGroupPython] Br_element008  label="Br_element : 005"  # scripted group (container) (typed FeaturePython)
  n = 1
  ref = Br_element
FEATURE [App::DocumentObjectGroupPython] G4_lBr  # scripted group (container) (typed FeaturePython)
  Dunit = g/cm3
  Dvalue = 3.1028
  Group = -> [Br_element008]
  conduct = 2
  density = 1
  expand = 3
  formula = G4_lBr
  name = G4_lBr
  specific = 4
FEATURE [App::DocumentObjectGroupPython] Kr_element002  label="Kr_element : 002"  # scripted group (container) (typed FeaturePython)
  n = 1
  ref = Kr_element
FEATURE [App::DocumentObjectGroupPython] G4_lKr  # scripted group (container) (typed FeaturePython)
  Dunit = g/cm3
  Dvalue = 2.418
  Group = -> [Kr_element002]
  conduct = 2
  density = 1
  expand = 3
  formula = G4_lKr
  name = G4_lKr
  specific = 4
FEATURE [App::DocumentObjectGroupPython] Xe_element002  label="Xe_element : 002"  # scripted group (container) (typed FeaturePython)
  n = 1
  ref = Xe_element
FEATURE [App::DocumentObjectGroupPython] G4_lXe  # scripted group (container) (typed FeaturePython)
  Dunit = g/cm3
  Dvalue = 2.953
  Group = -> [Xe_element002]
  conduct = 2
  density = 1
  expand = 3
  formula = G4_lXe
  name = G4_lXe
  specific = 4
FEATURE [App::DocumentObjectGroupPython] O_element107  label="O_element : 061"  # scripted group (container) (typed FeaturePython)
  n = 4
  ref = O_element
FEATURE [App::DocumentObjectGroupPython] Pb_element004  label="Pb_element : 002"  # scripted group (container) (typed FeaturePython)
  n = 1
  ref = Pb_element
FEATURE [App::DocumentObjectGroupPython] W_element005  label="W_element : 005"  # scripted group (container) (typed FeaturePython)
  n = 1
  ref = W_element
FEATURE [App::DocumentObjectGroupPython] G4_PbWO4  # scripted group (container) (typed FeaturePython)
  Dunit = g/cm3
  Dvalue = 8.28
  Group = -> [O_element107,Pb_element004,W_element005]
  conduct = 2
  density = 1
  expand = 3
  formula = G4_PbWO4
  name = G4_PbWO4
  specific = 4
FEATURE [App::DocumentObjectGroupPython] H_element115  label="H_element : 064"  # scripted group (container) (typed FeaturePython)
  n = 1
  ref = H_element
FEATURE [App::DocumentObjectGroupPython] G4_Galactic  # scripted group (container) (typed FeaturePython)
  Dunit = g/cm3
  Dvalue = 0
  Group = -> [H_element115]
  conduct = 2
  density = 1
  expand = 3
  formula = G4_Galactic
  name = G4_Galactic
  specific = 4
FEATURE [App::DocumentObjectGroupPython] C_element125  label="C_element : 071"  # scripted group (container) (typed FeaturePython)
  n = 1
  ref = C_element
FEATURE [App::DocumentObjectGroupPython] G4_GRAPHITE_POROUS  # scripted group (container) (typed FeaturePython)
  Dunit = g/cm3
  Dvalue = 1.7
  Group = -> [C_element125]
  conduct = 2
  density = 1
  expand = 3
  formula = G4_GRAPHITE_POROUS
  name = G4_GRAPHITE_POROUS
  specific = 4
FEATURE [App::DocumentObjectGroupPython] H_element116  label="H_element : 0.150"  # scripted group (container) (typed FeaturePython)
  n = 0.080538
FEATURE [App::DocumentObjectGroupPython] C_element126  label="C_element : 0.600"  # scripted group (container) (typed FeaturePython)
  n = 0.599848
FEATURE [App::DocumentObjectGroupPython] O_element108  label="O_element : 0.320"  # scripted group (container) (typed FeaturePython)
  n = 0.319614
FEATURE [App::DocumentObjectGroupPython] G4_LUCITE  # scripted group (container) (typed FeaturePython)
  Dunit = g/cm3
  Dvalue = 1.19
  Group = -> [H_element116,C_element126,O_element108]
  conduct = 2
  density = 1
  expand = 3
  formula = G4_LUCITE
  name = G4_LUCITE
  specific = 4
FEATURE [App::DocumentObjectGroupPython] Cu_element002  label="Cu_element : 62"  # scripted group (container) (typed FeaturePython)
  n = 62
  ref = Cu_element
FEATURE [App::DocumentObjectGroupPython] Zn_element002  label="Zn_element : 35"  # scripted group (container) (typed FeaturePython)
  n = 35
  ref = Zn_element
FEATURE [App::DocumentObjectGroupPython] Pb_element005  label="Pb_element : 3"  # scripted group (container) (typed FeaturePython)
  n = 3
  ref = Pb_element
FEATURE [App::DocumentObjectGroupPython] G4_BRASS  # scripted group (container) (typed FeaturePython)
  Dunit = g/cm3
  Dvalue = 8.52
  Group = -> [Cu_element002,Zn_element002,Pb_element005]
  conduct = 2
  density = 1
  expand = 3
  formula = G4_BRASS
  name = G4_BRASS
  specific = 4
FEATURE [App::DocumentObjectGroupPython] Cu_element003  label="Cu_element : 89"  # scripted group (container) (typed FeaturePython)
  n = 89
  ref = Cu_element
FEATURE [App::DocumentObjectGroupPython] Zn_element003  label="Zn_element : 9"  # scripted group (container) (typed FeaturePython)
  n = 9
  ref = Zn_element
FEATURE [App::DocumentObjectGroupPython] Pb_element006  label="Pb_element : 2"  # scripted group (container) (typed FeaturePython)
  n = 2
  ref = Pb_element
FEATURE [App::DocumentObjectGroupPython] G4_BRONZE  # scripted group (container) (typed FeaturePython)
  Dunit = g/cm3
  Dvalue = 8.82
  Group = -> [Cu_element003,Zn_element003,Pb_element006]
  conduct = 2
  density = 1
  expand = 3
  formula = G4_BRONZE
  name = G4_BRONZE
  specific = 4
FEATURE [App::DocumentObjectGroupPython] Fe_element008  label="Fe_element : 74"  # scripted group (container) (typed FeaturePython)
  n = 74
  ref = Fe_element
FEATURE [App::DocumentObjectGroupPython] Cr_element002  label="Cr_element : 18"  # scripted group (container) (typed FeaturePython)
  n = 18
  ref = Cr_element
FEATURE [App::DocumentObjectGroupPython] Ni_element002  label="Ni_element : 8"  # scripted group (container) (typed FeaturePython)
  n = 8
  ref = Ni_element
FEATURE [App::DocumentObjectGroupPython] G4_STAINLESS_STEEL  label="G4_STAINLESS-STEEL"  # scripted group (container) (typed FeaturePython)
  Dunit = g/cm3
  Dvalue = 8
  Group = -> [Fe_element008,Cr_element002,Ni_element002]
  conduct = 2
  density = 1
  expand = 3
  formula = G4_STAINLESS-STEEL
  name = G4_STAINLESS-STEEL
  specific = 4
FEATURE [App::DocumentObjectGroupPython] H_element117  label="H_element : 065"  # scripted group (container) (typed FeaturePython)
  n = 18
  ref = H_element
FEATURE [App::DocumentObjectGroupPython] C_element127  label="C_element : 072"  # scripted group (container) (typed FeaturePython)
  n = 12
  ref = C_element
FEATURE [App::DocumentObjectGroupPython] O_element109  label="O_element : 062"  # scripted group (container) (typed FeaturePython)
  n = 7
  ref = O_element
FEATURE [App::DocumentObjectGroupPython] G4_CR39  # scripted group (container) (typed FeaturePython)
  Dunit = g/cm3
  Dvalue = 1.32
  Group = -> [H_element117,C_element127,O_element109]
  conduct = 2
  density = 1
  expand = 3
  formula = G4_CR39
  name = G4_CR39
  specific = 4
FEATURE [App::DocumentObjectGroupPython] H_element118  label="H_element : 38"  # scripted group (container) (typed FeaturePython)
  n = 38
  ref = H_element
FEATURE [App::DocumentObjectGroupPython] C_element128  label="C_element : 073"  # scripted group (container) (typed FeaturePython)
  n = 18
  ref = C_element
FEATURE [App::DocumentObjectGroupPython] O_element110  label="O_element : 063"  # scripted group (container) (typed FeaturePython)
  n = 1
  ref = O_element
FEATURE [App::DocumentObjectGroupPython] G4_OCTADECANOL  # scripted group (container) (typed FeaturePython)
  Dunit = g/cm3
  Dvalue = 0.812
  Group = -> [H_element118,C_element128,O_element110]
  conduct = 2
  density = 1
  expand = 3
  formula = G4_OCTADECANOL
  name = G4_OCTADECANOL
  specific = 4
FEATURE [App::DocumentObjectGroupPython] HEP  # scripted group (container) (typed FeaturePython)
  Group = -> [G4_lH2,G4_lN2,G4_lO2,G4_lAr,G4_lBr,G4_lKr,G4_lXe,G4_PbWO4,G4_Galactic,G4_GRAPHITE_POROUS,G4_LUCITE,G4_BRASS,G4_BRONZE,G4_STAINLESS_STEEL,G4_CR39,G4_OCTADECANOL]
FEATURE [App::DocumentObjectGroupPython] C_element129  label="C_element : 074"  # scripted group (container) (typed FeaturePython)
  n = 14
  ref = C_element
FEATURE [App::DocumentObjectGroupPython] H_element119  label="H_element : 066"  # scripted group (container) (typed FeaturePython)
  n = 10
  ref = H_element
FEATURE [App::DocumentObjectGroupPython] O_element111  label="O_element : 064"  # scripted group (container) (typed FeaturePython)
  n = 2
  ref = O_element
FEATURE [App::DocumentObjectGroupPython] N_element050  label="N_element : 023"  # scripted group (container) (typed FeaturePython)
  n = 2
  ref = N_element
FEATURE [App::DocumentObjectGroupPython] G4_KEVLAR  # scripted group (container) (typed FeaturePython)
  Dunit = g/cm3
  Dvalue = 1.44
  Group = -> [C_element129,H_element119,O_element111,N_element050]
  conduct = 2
  density = 1
  expand = 3
  formula = G4_KEVLAR
  name = G4_KEVLAR
  specific = 4
FEATURE [App::DocumentObjectGroupPython] C_element130  label="C_element : 075"  # scripted group (container) (typed FeaturePython)
  n = 10
  ref = C_element
FEATURE [App::DocumentObjectGroupPython] H_element120  label="H_element : 067"  # scripted group (container) (typed FeaturePython)
  n = 8
  ref = H_element
FEATURE [App::DocumentObjectGroupPython] O_element112  label="O_element : 065"  # scripted group (container) (typed FeaturePython)
  n = 4
  ref = O_element
FEATURE [App::DocumentObjectGroupPython] G4_DACRON  # scripted group (container) (typed FeaturePython)
  Dunit = g/cm3
  Dvalue = 1.4
  Group = -> [C_element130,H_element120,O_element112]
  conduct = 2
  density = 1
  expand = 3
  formula = G4_DACRON
  name = G4_DACRON
  specific = 4
FEATURE [App::DocumentObjectGroupPython] C_element131  label="C_element : 076"  # scripted group (container) (typed FeaturePython)
  n = 4
  ref = C_element
FEATURE [App::DocumentObjectGroupPython] H_element121  label="H_element : 068"  # scripted group (container) (typed FeaturePython)
  n = 5
  ref = H_element
FEATURE [App::DocumentObjectGroupPython] Cl_element030  label="Cl_element : 016"  # scripted group (container) (typed FeaturePython)
  n = 1
  ref = Cl_element
FEATURE [App::DocumentObjectGroupPython] G4_NEOPRENE  # scripted group (container) (typed FeaturePython)
  Dunit = g/cm3
  Dvalue = 1.23
  Group = -> [C_element131,H_element121,Cl_element030]
  conduct = 2
  density = 1
  expand = 3
  formula = G4_NEOPRENE
  name = G4_NEOPRENE
  specific = 4
FEATURE [App::DocumentObjectGroupPython] Space  # scripted group (container) (typed FeaturePython)
  Group = -> [G4_KEVLAR,G4_DACRON,G4_NEOPRENE]
FEATURE [App::DocumentObjectGroupPython] H_element122  label="H_element : 069"  # scripted group (container) (typed FeaturePython)
  n = 5
  ref = H_element
FEATURE [App::DocumentObjectGroupPython] C_element132  label="C_element : 077"  # scripted group (container) (typed FeaturePython)
  n = 4
  ref = C_element
FEATURE [App::DocumentObjectGroupPython] N_element051  label="N_element : 3"  # scripted group (container) (typed FeaturePython)
  n = 3
  ref = N_element
FEATURE [App::DocumentObjectGroupPython] O_element113  label="O_element : 066"  # scripted group (container) (typed FeaturePython)
  n = 1
  ref = O_element
FEATURE [App::DocumentObjectGroupPython] G4_CYTOSINE  # scripted group (container) (typed FeaturePython)
  Dunit = g/cm3
  Dvalue = 1.55
  Group = -> [H_element122,C_element132,N_element051,O_element113]
  conduct = 2
  density = 1
  expand = 3
  formula = G4_CYTOSINE
  name = G4_CYTOSINE
  specific = 4
FEATURE [App::DocumentObjectGroupPython] H_element123  label="H_element : 070"  # scripted group (container) (typed FeaturePython)
  n = 6
  ref = H_element
FEATURE [App::DocumentObjectGroupPython] C_element133  label="C_element : 078"  # scripted group (container) (typed FeaturePython)
  n = 5
  ref = C_element
FEATURE [App::DocumentObjectGroupPython] N_element052  label="N_element : 024"  # scripted group (container) (typed FeaturePython)
  n = 2
  ref = N_element
FEATURE [App::DocumentObjectGroupPython] O_element114  label="O_element : 067"  # scripted group (container) (typed FeaturePython)
  n = 2
  ref = O_element
FEATURE [App::DocumentObjectGroupPython] G4_THYMINE  # scripted group (container) (typed FeaturePython)
  Dunit = g/cm3
  Dvalue = 1.23
  Group = -> [H_element123,C_element133,N_element052,O_element114]
  conduct = 2
  density = 1
  expand = 3
  formula = G4_THYMINE
  name = G4_THYMINE
  specific = 4
FEATURE [App::DocumentObjectGroupPython] H_element124  label="H_element : 071"  # scripted group (container) (typed FeaturePython)
  n = 4
  ref = H_element
FEATURE [App::DocumentObjectGroupPython] C_element134  label="C_element : 079"  # scripted group (container) (typed FeaturePython)
  n = 4
  ref = C_element
FEATURE [App::DocumentObjectGroupPython] N_element053  label="N_element : 025"  # scripted group (container) (typed FeaturePython)
  n = 2
  ref = N_element
FEATURE [App::DocumentObjectGroupPython] O_element115  label="O_element : 068"  # scripted group (container) (typed FeaturePython)
  n = 2
  ref = O_element
FEATURE [App::DocumentObjectGroupPython] G4_URACIL  # scripted group (container) (typed FeaturePython)
  Dunit = g/cm3
  Dvalue = 1.32
  Group = -> [H_element124,C_element134,N_element053,O_element115]
  conduct = 2
  density = 1
  expand = 3
  formula = G4_URACIL
  name = G4_URACIL
  specific = 4
FEATURE [App::DocumentObjectGroupPython] H_element125  label="H_element : 072"  # scripted group (container) (typed FeaturePython)
  n = 4
  ref = H_element
FEATURE [App::DocumentObjectGroupPython] C_element135  label="C_element : 080"  # scripted group (container) (typed FeaturePython)
  n = 5
  ref = C_element
FEATURE [App::DocumentObjectGroupPython] N_element054  label="N_element : 026"  # scripted group (container) (typed FeaturePython)
  n = 5
  ref = N_element
FEATURE [App::DocumentObjectGroupPython] G4_DNA_ADENINE  # scripted group (container) (typed FeaturePython)
  Dunit = g/cm3
  Dvalue = 1
  Group = -> [H_element125,C_element135,N_element054]
  conduct = 2
  density = 1
  expand = 3
  formula = G4_DNA_ADENINE
  name = G4_DNA_ADENINE
  specific = 4
FEATURE [App::DocumentObjectGroupPython] H_element126  label="H_element : 073"  # scripted group (container) (typed FeaturePython)
  n = 4
  ref = H_element
FEATURE [App::DocumentObjectGroupPython] C_element136  label="C_element : 081"  # scripted group (container) (typed FeaturePython)
  n = 5
  ref = C_element
FEATURE [App::DocumentObjectGroupPython] N_element055  label="N_element : 027"  # scripted group (container) (typed FeaturePython)
  n = 5
  ref = N_element
FEATURE [App::DocumentObjectGroupPython] O_element116  label="O_element : 069"  # scripted group (container) (typed FeaturePython)
  n = 1
  ref = O_element
FEATURE [App::DocumentObjectGroupPython] G4_DNA_GUANINE  # scripted group (container) (typed FeaturePython)
  Dunit = g/cm3
  Dvalue = 1
  Group = -> [H_element126,C_element136,N_element055,O_element116]
  conduct = 2
  density = 1
  expand = 3
  formula = G4_DNA_GUANINE
  name = G4_DNA_GUANINE
  specific = 4
FEATURE [App::DocumentObjectGroupPython] H_element127  label="H_element : 074"  # scripted group (container) (typed FeaturePython)
  n = 4
  ref = H_element
FEATURE [App::DocumentObjectGroupPython] C_element137  label="C_element : 082"  # scripted group (container) (typed FeaturePython)
  n = 4
  ref = C_element
FEATURE [App::DocumentObjectGroupPython] N_element056  label="N_element : 028"  # scripted group (container) (typed FeaturePython)
  n = 3
  ref = N_element
FEATURE [App::DocumentObjectGroupPython] O_element117  label="O_element : 070"  # scripted group (container) (typed FeaturePython)
  n = 1
  ref = O_element
FEATURE [App::DocumentObjectGroupPython] G4_DNA_CYTOSINE  # scripted group (container) (typed FeaturePython)
  Dunit = g/cm3
  Dvalue = 1
  Group = -> [H_element127,C_element137,N_element056,O_element117]
  conduct = 2
  density = 1
  expand = 3
  formula = G4_DNA_CYTOSINE
  name = G4_DNA_CYTOSINE
  specific = 4
FEATURE [App::DocumentObjectGroupPython] H_element128  label="H_element : 075"  # scripted group (container) (typed FeaturePython)
  n = 5
  ref = H_element
FEATURE [App::DocumentObjectGroupPython] C_element138  label="C_element : 083"  # scripted group (container) (typed FeaturePython)
  n = 5
  ref = C_element
FEATURE [App::DocumentObjectGroupPython] N_element057  label="N_element : 029"  # scripted group (container) (typed FeaturePython)
  n = 2
  ref = N_element
FEATURE [App::DocumentObjectGroupPython] O_element118  label="O_element : 071"  # scripted group (container) (typed FeaturePython)
  n = 2
  ref = O_element
FEATURE [App::DocumentObjectGroupPython] G4_DNA_THYMINE  # scripted group (container) (typed FeaturePython)
  Dunit = g/cm3
  Dvalue = 1
  Group = -> [H_element128,C_element138,N_element057,O_element118]
  conduct = 2
  density = 1
  expand = 3
  formula = G4_DNA_THYMINE
  name = G4_DNA_THYMINE
  specific = 4
FEATURE [App::DocumentObjectGroupPython] H_element129  label="H_element : 076"  # scripted group (container) (typed FeaturePython)
  n = 3
  ref = H_element
FEATURE [App::DocumentObjectGroupPython] C_element139  label="C_element : 084"  # scripted group (container) (typed FeaturePython)
  n = 4
  ref = C_element
FEATURE [App::DocumentObjectGroupPython] N_element058  label="N_element : 030"  # scripted group (container) (typed FeaturePython)
  n = 2
  ref = N_element
FEATURE [App::DocumentObjectGroupPython] O_element119  label="O_element : 072"  # scripted group (container) (typed FeaturePython)
  n = 2
  ref = O_element
FEATURE [App::DocumentObjectGroupPython] G4_DNA_URACIL  # scripted group (container) (typed FeaturePython)
  Dunit = g/cm3
  Dvalue = 1
  Group = -> [H_element129,C_element139,N_element058,O_element119]
  conduct = 2
  density = 1
  expand = 3
  formula = G4_DNA_URACIL
  name = G4_DNA_URACIL
  specific = 4
FEATURE [App::DocumentObjectGroupPython] H_element130  label="H_element : 077"  # scripted group (container) (typed FeaturePython)
  n = 10
  ref = H_element
FEATURE [App::DocumentObjectGroupPython] C_element140  label="C_element : 085"  # scripted group (container) (typed FeaturePython)
  n = 10
  ref = C_element
FEATURE [App::DocumentObjectGroupPython] N_element059  label="N_element : 031"  # scripted group (container) (typed FeaturePython)
  n = 5
  ref = N_element
FEATURE [App::DocumentObjectGroupPython] O_element120  label="O_element : 073"  # scripted group (container) (typed FeaturePython)
  n = 4
  ref = O_element
FEATURE [App::DocumentObjectGroupPython] G4_DNA_ADENOSINE  # scripted group (container) (typed FeaturePython)
  Dunit = g/cm3
  Dvalue = 1
  Group = -> [H_element130,C_element140,N_element059,O_element120]
  conduct = 2
  density = 1
  expand = 3
  formula = G4_DNA_ADENOSINE
  name = G4_DNA_ADENOSINE
  specific = 4
FEATURE [App::DocumentObjectGroupPython] H_element131  label="H_element : 078"  # scripted group (container) (typed FeaturePython)
  n = 10
  ref = H_element
FEATURE [App::DocumentObjectGroupPython] C_element141  label="C_element : 086"  # scripted group (container) (typed FeaturePython)
  n = 10
  ref = C_element
FEATURE [App::DocumentObjectGroupPython] N_element060  label="N_element : 032"  # scripted group (container) (typed FeaturePython)
  n = 5
  ref = N_element
FEATURE [App::DocumentObjectGroupPython] O_element121  label="O_element : 074"  # scripted group (container) (typed FeaturePython)
  n = 5
  ref = O_element
FEATURE [App::DocumentObjectGroupPython] G4_DNA_GUANOSINE  # scripted group (container) (typed FeaturePython)
  Dunit = g/cm3
  Dvalue = 1
  Group = -> [H_element131,C_element141,N_element060,O_element121]
  conduct = 2
  density = 1
  expand = 3
  formula = G4_DNA_GUANOSINE
  name = G4_DNA_GUANOSINE
  specific = 4
FEATURE [App::DocumentObjectGroupPython] H_element132  label="H_element : 079"  # scripted group (container) (typed FeaturePython)
  n = 10
  ref = H_element
FEATURE [App::DocumentObjectGroupPython] C_element142  label="C_element : 087"  # scripted group (container) (typed FeaturePython)
  n = 9
  ref = C_element
FEATURE [App::DocumentObjectGroupPython] N_element061  label="N_element : 033"  # scripted group (container) (typed FeaturePython)
  n = 3
  ref = N_element
FEATURE [App::DocumentObjectGroupPython] O_element122  label="O_element : 075"  # scripted group (container) (typed FeaturePython)
  n = 5
  ref = O_element
FEATURE [App::DocumentObjectGroupPython] G4_DNA_CYTIDINE  # scripted group (container) (typed FeaturePython)
  Dunit = g/cm3
  Dvalue = 1
  Group = -> [H_element132,C_element142,N_element061,O_element122]
  conduct = 2
  density = 1
  expand = 3
  formula = G4_DNA_CYTIDINE
  name = G4_DNA_CYTIDINE
  specific = 4
FEATURE [App::DocumentObjectGroupPython] H_element133  label="H_element : 080"  # scripted group (container) (typed FeaturePython)
  n = 9
  ref = H_element
FEATURE [App::DocumentObjectGroupPython] C_element143  label="C_element : 088"  # scripted group (container) (typed FeaturePython)
  n = 9
  ref = C_element
FEATURE [App::DocumentObjectGroupPython] N_element062  label="N_element : 034"  # scripted group (container) (typed FeaturePython)
  n = 2
  ref = N_element
FEATURE [App::DocumentObjectGroupPython] O_element123  label="O_element : 076"  # scripted group (container) (typed FeaturePython)
  n = 6
  ref = O_element
FEATURE [App::DocumentObjectGroupPython] G4_DNA_URIDINE  # scripted group (container) (typed FeaturePython)
  Dunit = g/cm3
  Dvalue = 1
  Group = -> [H_element133,C_element143,N_element062,O_element123]
  conduct = 2
  density = 1
  expand = 3
  formula = G4_DNA_URIDINE
  name = G4_DNA_URIDINE
  specific = 4
FEATURE [App::DocumentObjectGroupPython] H_element134  label="H_element : 081"  # scripted group (container) (typed FeaturePython)
  n = 11
  ref = H_element
FEATURE [App::DocumentObjectGroupPython] C_element144  label="C_element : 089"  # scripted group (container) (typed FeaturePython)
  n = 10
  ref = C_element
FEATURE [App::DocumentObjectGroupPython] N_element063  label="N_element : 035"  # scripted group (container) (typed FeaturePython)
  n = 2
  ref = N_element
FEATURE [App::DocumentObjectGroupPython] O_element124  label="O_element : 077"  # scripted group (container) (typed FeaturePython)
  n = 6
  ref = O_element
FEATURE [App::DocumentObjectGroupPython] G4_DNA_METHYLURIDINE  # scripted group (container) (typed FeaturePython)
  Dunit = g/cm3
  Dvalue = 1
  Group = -> [H_element134,C_element144,N_element063,O_element124]
  conduct = 2
  density = 1
  expand = 3
  formula = G4_DNA_METHYLURIDINE
  name = G4_DNA_METHYLURIDINE
  specific = 4
FEATURE [App::DocumentObjectGroupPython] P_element014  label="P_element : 003"  # scripted group (container) (typed FeaturePython)
  n = 1
  ref = P_element
FEATURE [App::DocumentObjectGroupPython] O_element125  label="O_element : 078"  # scripted group (container) (typed FeaturePython)
  n = 3
  ref = O_element
FEATURE [App::DocumentObjectGroupPython] G4_DNA_MONOPHOSPHATE  # scripted group (container) (typed FeaturePython)
  Dunit = g/cm3
  Dvalue = 1
  Group = -> [P_element014,O_element125]
  conduct = 2
  density = 1
  expand = 3
  formula = G4_DNA_MONOPHOSPHATE
  name = G4_DNA_MONOPHOSPHATE
  specific = 4
FEATURE [App::DocumentObjectGroupPython] H_element135  label="H_element : 082"  # scripted group (container) (typed FeaturePython)
  n = 10
  ref = H_element
FEATURE [App::DocumentObjectGroupPython] C_element145  label="C_element : 090"  # scripted group (container) (typed FeaturePython)
  n = 10
  ref = C_element
FEATURE [App::DocumentObjectGroupPython] N_element064  label="N_element : 036"  # scripted group (container) (typed FeaturePython)
  n = 5
  ref = N_element
FEATURE [App::DocumentObjectGroupPython] O_element126  label="O_element : 079"  # scripted group (container) (typed FeaturePython)
  n = 7
  ref = O_element
FEATURE [App::DocumentObjectGroupPython] P_element015  label="P_element : 004"  # scripted group (container) (typed FeaturePython)
  n = 1
  ref = P_element
FEATURE [App::DocumentObjectGroupPython] G4_DNA_A  # scripted group (container) (typed FeaturePython)
  Dunit = g/cm3
  Dvalue = 1
  Group = -> [H_element135,C_element145,N_element064,O_element126,P_element015]
  conduct = 2
  density = 1
  expand = 3
  formula = G4_DNA_A
  name = G4_DNA_A
  specific = 4
FEATURE [App::DocumentObjectGroupPython] H_element136  label="H_element : 083"  # scripted group (container) (typed FeaturePython)
  n = 10
  ref = H_element
FEATURE [App::DocumentObjectGroupPython] C_element146  label="C_element : 091"  # scripted group (container) (typed FeaturePython)
  n = 10
  ref = C_element
FEATURE [App::DocumentObjectGroupPython] N_element065  label="N_element : 037"  # scripted group (container) (typed FeaturePython)
  n = 5
  ref = N_element
FEATURE [App::DocumentObjectGroupPython] O_element127  label="O_element : 8"  # scripted group (container) (typed FeaturePython)
  n = 8
  ref = O_element
FEATURE [App::DocumentObjectGroupPython] P_element016  label="P_element : 005"  # scripted group (container) (typed FeaturePython)
  n = 1
  ref = P_element
FEATURE [App::DocumentObjectGroupPython] G4_DNA_G  # scripted group (container) (typed FeaturePython)
  Dunit = g/cm3
  Dvalue = 1
  Group = -> [H_element136,C_element146,N_element065,O_element127,P_element016]
  conduct = 2
  density = 1
  expand = 3
  formula = G4_DNA_G
  name = G4_DNA_G
  specific = 4
FEATURE [App::DocumentObjectGroupPython] H_element137  label="H_element : 084"  # scripted group (container) (typed FeaturePython)
  n = 10
  ref = H_element
FEATURE [App::DocumentObjectGroupPython] C_element147  label="C_element : 092"  # scripted group (container) (typed FeaturePython)
  n = 9
  ref = C_element
FEATURE [App::DocumentObjectGroupPython] N_element066  label="N_element : 038"  # scripted group (container) (typed FeaturePython)
  n = 3
  ref = N_element
FEATURE [App::DocumentObjectGroupPython] O_element128  label="O_element : 080"  # scripted group (container) (typed FeaturePython)
  n = 8
  ref = O_element
FEATURE [App::DocumentObjectGroupPython] P_element017  label="P_element : 006"  # scripted group (container) (typed FeaturePython)
  n = 1
  ref = P_element
FEATURE [App::DocumentObjectGroupPython] G4_DNA_C  # scripted group (container) (typed FeaturePython)
  Dunit = g/cm3
  Dvalue = 1
  Group = -> [H_element137,C_element147,N_element066,O_element128,P_element017]
  conduct = 2
  density = 1
  expand = 3
  formula = G4_DNA_C
  name = G4_DNA_C
  specific = 4
FEATURE [App::DocumentObjectGroupPython] H_element138  label="H_element : 085"  # scripted group (container) (typed FeaturePython)
  n = 9
  ref = H_element
FEATURE [App::DocumentObjectGroupPython] C_element148  label="C_element : 093"  # scripted group (container) (typed FeaturePython)
  n = 9
  ref = C_element
FEATURE [App::DocumentObjectGroupPython] N_element067  label="N_element : 039"  # scripted group (container) (typed FeaturePython)
  n = 2
  ref = N_element
FEATURE [App::DocumentObjectGroupPython] O_element129  label="O_element : 9"  # scripted group (container) (typed FeaturePython)
  n = 9
  ref = O_element
FEATURE [App::DocumentObjectGroupPython] P_element018  label="P_element : 007"  # scripted group (container) (typed FeaturePython)
  n = 1
  ref = P_element
FEATURE [App::DocumentObjectGroupPython] G4_DNA_U  # scripted group (container) (typed FeaturePython)
  Dunit = g/cm3
  Dvalue = 1
  Group = -> [H_element138,C_element148,N_element067,O_element129,P_element018]
  conduct = 2
  density = 1
  expand = 3
  formula = G4_DNA_U
  name = G4_DNA_U
  specific = 4
FEATURE [App::DocumentObjectGroupPython] H_element139  label="H_element : 086"  # scripted group (container) (typed FeaturePython)
  n = 11
  ref = H_element
FEATURE [App::DocumentObjectGroupPython] C_element149  label="C_element : 094"  # scripted group (container) (typed FeaturePython)
  n = 10
  ref = C_element
FEATURE [App::DocumentObjectGroupPython] N_element068  label="N_element : 040"  # scripted group (container) (typed FeaturePython)
  n = 2
  ref = N_element
FEATURE [App::DocumentObjectGroupPython] O_element130  label="O_element : 081"  # scripted group (container) (typed FeaturePython)
  n = 9
  ref = O_element
FEATURE [App::DocumentObjectGroupPython] P_element019  label="P_element : 008"  # scripted group (container) (typed FeaturePython)
  n = 1
  ref = P_element
FEATURE [App::DocumentObjectGroupPython] G4_DNA_MU  # scripted group (container) (typed FeaturePython)
  Dunit = g/cm3
  Dvalue = 1
  Group = -> [H_element139,C_element149,N_element068,O_element130,P_element019]
  conduct = 2
  density = 1
  expand = 3
  formula = G4_DNA_MU
  name = G4_DNA_MU
  specific = 4
FEATURE [App::DocumentObjectGroupPython] BioChemical  # scripted group (container) (typed FeaturePython)
  Group = -> [G4_CYTOSINE,G4_THYMINE,G4_URACIL,G4_DNA_ADENINE,G4_DNA_GUANINE,G4_DNA_CYTOSINE,G4_DNA_THYMINE,G4_DNA_URACIL,G4_DNA_ADENOSINE,G4_DNA_GUANOSINE,G4_DNA_CYTIDINE,G4_DNA_URIDINE,G4_DNA_METHYLURIDINE,G4_DNA_MONOPHOSPHATE,G4_DNA_A,G4_DNA_G,G4_DNA_C,G4_DNA_U,G4_DNA_MU]
FEATURE [App::DocumentObjectGroupPython] G4Materials  # scripted group (container) (typed FeaturePython)
  Group = -> [NIST,Element,HEP,Space,BioChemical]
  version = 1
FEATURE [App::DocumentObjectGroupPython] Geant4  # scripted group (container) (typed FeaturePython)
  Group = -> [G4Isotopes,G4Elements,G4Materials]
FEATURE [App::DocumentObjectGroupPython] Materials  # scripted group (container) (typed FeaturePython)
  Group = -> [Geant4]
FEATURE [Part::FeaturePython] GDMLBox_WorldBox  # WARN: FeaturePython — macro-defined, semantics opaque (R4)
  lunit = 2
  material = 5
  x = 100
  y = 100
  z = 100
FEATURE [Part::Box] Box001  label="Cube001"
  AttacherType = Attacher::AttachEngine3D
  Height = 10
  Length = 10
  Width = 10
FEATURE [Part::Fillet] Fillet
  Base = -> Box001
  Edges = 12 edges r=1: [Edge1,Edge2,Edge3,Edge4,Edge5,Edge6,Edge7,Edge8,Edge9,Edge10,Edge11,Edge12]
  Placement = pos=(0,0,-7) rot=(0,0,1;0rad)
FEATURE [App::Part] Part  label="Part_fillet"
  Group = -> [Box001,Fillet]
  Origin = -> Origin001
  Placement = pos=(-14,0,15) rot=(0,0,1;0rad)
FEATURE [App::Part] worldVOL
  Group = -> [GDMLBox_WorldBox,Part]
  Origin = -> Origin
